FCSTD DOCUMENT  (FreeCAD 1.0R39109 (Git))
Label: solar-strandbeest-v9
License: All rights reserved
LicenseURL: http://en.wikipedia.org/wiki/All_rights_reserved
objects: Sketcher::SketchObject×26, Spreadsheet::Sheet×2, PartDesign::Body×1, App::DocumentObjectGroup×1
note: 53 computed .brp shape members not serialized (recipe doc carries the construction recipe); baked Part::Feature solids carry a one-line shape summary decoded from their .brp

FEATURE [Sketcher::SketchObject] Sketch063  label="construction"
  ArcFitTolerance = 1e-06
  AttachmentSupport = -> [XY_Plane005]
  FullyConstrained = true
  MakeInternals = false
  MapMode = 5
  expr: Constraints[110] = <<v8-Dimensions>>.aGearDistance
  expr: Constraints[115] = <<v8-Dimensions>>.tabHeight
  expr: Constraints[118] = <<v8-Dimensions>>.tabDistanceCut
  expr: Constraints[121] = <<v8-Dimensions>>.solarPanelDepthCut
  expr: Constraints[13] = <<v8-Dimensions>>.aLowerSupportDrop
  expr: Constraints[155] = <<v8-Dimensions>>.aMotorShaftDiameter
  expr: Constraints[186] = <<v8-Dimensions>>.tabWidthCut
  expr: Constraints[187] = <<v8-Dimensions>>.tabHeightCut
  expr: Constraints[189] = <<v8-Dimensions>>.solarPanelWidthCut
  expr: Constraints[18] = 8 mm
  expr: Constraints[198] = <<v8-Dimensions>>.solarSideWidthCut
  expr: Constraints[207] = <<v8-Dimensions>>.jBendPoint
  expr: Constraints[208] = <<v8-Dimensions>>.jBendPoint
  expr: Constraints[209] = <<v8-Dimensions>>.jBendWidth
  expr: Constraints[210] = <<v8-Dimensions>>.jBendOffset
  expr: Constraints[213] = <<v8-Dimensions>>.jBendOffset
  expr: Constraints[215] = <<v8-Dimensions>>.kBendPoint
  expr: Constraints[216] = <<v8-Dimensions>>.kBendWidth
  expr: Constraints[218] = <<v8-Dimensions>>.kBendPoint
  expr: Constraints[219] = <<v8-Dimensions>>.kBendOffset
  expr: Constraints[222] = <<v8-Dimensions>>.eBendWidth
  expr: Constraints[223] = <<v8-Dimensions>>.eBendOffset
  expr: Constraints[225] = <<v8-Dimensions>>.dBendWidth
  expr: Constraints[226] = <<v8-Dimensions>>.dBendOffset
  expr: Constraints[228] = <<v8-Dimensions>>.bBendWidth
  expr: Constraints[229] = <<v8-Dimensions>>.bBendOffset
  expr: Constraints[230] = <<v8-Dimensions>>.kBendOffset
  expr: Constraints[231] = <<v8-Dimensions>>.bdeJunctionEdge
  expr: Constraints[232] = <<v8-Dimensions>>.frame4mmCut
  expr: Constraints[233] = <<v8-Dimensions>>.frame4mmEdge
  expr: Constraints[239] = <<v8-Dimensions>>.fBendWidth
  expr: Constraints[240] = <<v8-Dimensions>>.fBendOffset
  expr: Constraints[241] = <<v8-Dimensions>>.cBendWidth
  expr: Constraints[242] = <<v8-Dimensions>>.cBendOffset
  expr: Constraints[243] = <<v8-Dimensions>>.gBendWidth
  expr: Constraints[244] = <<v8-Dimensions>>.gBendOffset
  expr: Constraints[245] = <<v8-Dimensions>>.hBendWidth
  expr: Constraints[246] = <<v8-Dimensions>>.hBendOffset
  expr: Constraints[247] = <<v8-Dimensions>>.iBendWidth
  expr: Constraints[248] = <<v8-Dimensions>>.iBendOffset
  expr: Constraints[249] = <<v8-Dimensions>>.aMotorToTabCenterDistance
  expr: Constraints[258] = <<v8-Dimensions>>.tabHeightCut
  expr: Constraints[259] = <<v8-Dimensions>>.tabWidthCut
  expr: Constraints[269] = <<v8-Dimensions>>.tabHeightCut
  expr: Constraints[270] = <<v8-Dimensions>>.tabWidthCut
  expr: Constraints[272] = <<v8-Dimensions>>.solarTabWidthCut
  expr: Constraints[95] = <<v8-Dimensions>>.ghiFootRadius
  sketch-geometry (114):
    g0: Circle CenterX=0 CenterY=0 CenterZ=0 NormalX=0 NormalY=0 NormalZ=1 AngleXU=0 Radius=5
    g1: Circle CenterX=0 CenterY=0 CenterZ=0 NormalX=0 NormalY=0 NormalZ=1 AngleXU=0 Radius=3
    g2: LineSegment StartX=0 StartY=0 StartZ=0 EndX=0 EndY=-15.6 EndZ=0
    g3: LineSegment StartX=0 StartY=-15.6 StartZ=0 EndX=-76 EndY=-15.6 EndZ=0
    g4: LineSegment StartX=0 StartY=-15.6 StartZ=0 EndX=76 EndY=-15.6 EndZ=0
    g5: LineSegment StartX=0 StartY=0 StartZ=0 EndX=0 EndY=-70 EndZ=0
    g6: Circle CenterX=-76 CenterY=-15.6 CenterZ=0 NormalX=0 NormalY=0 NormalZ=1 AngleXU=0 Radius=2
    g7: Circle CenterX=-76 CenterY=-15.6 CenterZ=0 NormalX=0 NormalY=0 NormalZ=1 AngleXU=0 Radius=4
    g8: Circle CenterX=76 CenterY=-15.6 CenterZ=0 NormalX=0 NormalY=0 NormalZ=1 AngleXU=0 Radius=2
    g9: Circle CenterX=76 CenterY=-15.6 CenterZ=0 NormalX=0 NormalY=0 NormalZ=1 AngleXU=0 Radius=4
    g10: Circle CenterX=0 CenterY=-70 CenterZ=0 NormalX=0 NormalY=0 NormalZ=1 AngleXU=0 Radius=2
    g11: Circle CenterX=0 CenterY=-70 CenterZ=0 NormalX=0 NormalY=0 NormalZ=1 AngleXU=0 Radius=1.92
    g12: LineSegment StartX=0 StartY=0 StartZ=0 EndX=-25.7172 EndY=15.4475 EndZ=0
    g13: Circle CenterX=-25.7172 CenterY=15.4475 CenterZ=0 NormalX=0 NormalY=0 NormalZ=1 AngleXU=0 Radius=3
    g14: Circle CenterX=-25.7172 CenterY=15.4475 CenterZ=0 NormalX=0 NormalY=0 NormalZ=1 AngleXU=0 Radius=5
    g15: LineSegment StartX=-25.7172 StartY=15.4475 StartZ=0 EndX=-83.9611 EndY=-93.7958 EndZ=0
    g16: LineSegment StartX=-83.9611 StartY=-93.7958 StartZ=0 EndX=-23.6866 EndY=-171.068 EndZ=0
    g17: LineSegment StartX=-23.6866 StartY=-171.068 StartZ=0 EndX=-148.246 EndY=-129.223 EndZ=0
    g18: LineSegment StartX=-148.246 StartY=-129.223 StartZ=0 EndX=-83.9611 EndY=-93.7958 EndZ=0
    g19: LineSegment StartX=-148.246 StartY=-129.223 StartZ=0 EndX=-148.246 EndY=-50.4227 EndZ=0
    g20: LineSegment StartX=-148.246 StartY=-50.4227 StartZ=0 EndX=-76 EndY=-15.6 EndZ=0
    g21: LineSegment StartX=-76 StartY=-15.6 StartZ=0 EndX=-83.9611 EndY=-93.7958 EndZ=0
    g22: LineSegment StartX=-148.246 StartY=-50.4227 StartZ=0 EndX=-116.828 EndY=56.6638 EndZ=0
    g23: LineSegment StartX=-116.828 StartY=56.6638 StartZ=0 EndX=-76 EndY=-15.6 EndZ=0
    g24: LineSegment StartX=-116.828 StartY=56.6638 StartZ=0 EndX=-25.7172 EndY=15.4475 EndZ=0
    g25: LineSegment StartX=-25.7172 StartY=15.4475 StartZ=0 EndX=60.5893 EndY=65.9568 EndZ=0
    g26: LineSegment StartX=60.5893 StartY=65.9568 StartZ=0 EndX=76 EndY=-15.6 EndZ=0
    g27: LineSegment StartX=76 StartY=-15.6 StartZ=0 EndX=153.669 EndY=4.38827 EndZ=0
    g28: LineSegment StartX=153.669 StartY=4.38827 StartZ=0 EndX=60.5893 EndY=65.9568 EndZ=0
    g29: LineSegment StartX=153.669 StartY=4.38827 StartZ=0 EndX=112.83 EndY=-63.0032 EndZ=0
    g30: LineSegment StartX=76 StartY=-15.6 StartZ=0 EndX=43.5253 EndY=-87.1776 EndZ=0
    g31: LineSegment StartX=43.5253 StartY=-87.1776 StartZ=0 EndX=112.83 EndY=-63.0032 EndZ=0
    g32: LineSegment StartX=112.83 StartY=-63.0032 StartZ=0 EndX=60.7671 EndY=-183.649 EndZ=0
    g33: LineSegment StartX=60.7671 StartY=-183.649 StartZ=0 EndX=43.5253 EndY=-87.1776 EndZ=0
    g34: Circle CenterX=-116.828 CenterY=56.6638 CenterZ=0 NormalX=0 NormalY=0 NormalZ=1 AngleXU=0 Radius=1.5
    g35: Circle CenterX=-148.246 CenterY=-50.4227 CenterZ=0 NormalX=0 NormalY=0 NormalZ=1 AngleXU=0 Radius=1.1e-15
    g36: Circle CenterX=-148.246 CenterY=-50.4227 CenterZ=0 NormalX=0 NormalY=0 NormalZ=1 AngleXU=0 Radius=1.5
    g37: Circle CenterX=-148.246 CenterY=-129.223 CenterZ=0 NormalX=0 NormalY=0 NormalZ=1 AngleXU=0 Radius=1.6e-15
    g38: Circle CenterX=-148.246 CenterY=-129.223 CenterZ=0 NormalX=0 NormalY=0 NormalZ=1 AngleXU=0 Radius=1.5
    g39: Circle CenterX=-83.9611 CenterY=-93.7958 CenterZ=0 NormalX=0 NormalY=0 NormalZ=1 AngleXU=0 Radius=1.5
    g40: LineSegment StartX=-23.6866 StartY=-171.068 StartZ=0 EndX=-24.9107 EndY=-170.201 EndZ=0
    g41: Circle CenterX=-24.9107 CenterY=-170.201 CenterZ=0 NormalX=0 NormalY=0 NormalZ=1 AngleXU=0 Radius=1.5
    g42: LineSegment StartX=60.7671 StartY=-183.649 StartZ=0 EndX=60.9396 EndY=-182.159 EndZ=0
    g43: LineSegment StartX=-25.7172 StartY=15.4475 StartZ=0 EndX=43.5253 EndY=-87.1776 EndZ=0
    g44: Circle CenterX=60.5893 CenterY=65.9568 CenterZ=0 NormalX=0 NormalY=0 NormalZ=1 AngleXU=0 Radius=1.5
    g45: Circle CenterX=153.669 CenterY=4.38827 CenterZ=0 NormalX=0 NormalY=0 NormalZ=1 AngleXU=0 Radius=1.5
    g46: Circle CenterX=112.83 CenterY=-63.0032 CenterZ=0 NormalX=0 NormalY=0 NormalZ=1 AngleXU=0 Radius=7e-16
    g47: Circle CenterX=43.5253 CenterY=-87.1776 CenterZ=0 NormalX=0 NormalY=0 NormalZ=1 AngleXU=0 Radius=1.5
    g48: Circle CenterX=112.83 CenterY=-63.0032 CenterZ=0 NormalX=0 NormalY=0 NormalZ=1 AngleXU=0 Radius=1.5
    g49: Circle CenterX=60.9396 CenterY=-182.159 CenterZ=0 NormalX=0 NormalY=0 NormalZ=1 AngleXU=0 Radius=1.5
    g50: LineSegment StartX=0 StartY=0 StartZ=0 EndX=0 EndY=66 EndZ=0
    g51: LineSegment StartX=0 StartY=66 StartZ=0 EndX=0 EndY=75 EndZ=0
    g52: LineSegment StartX=0 StartY=75 StartZ=0 EndX=0 EndY=78 EndZ=0
    g53: LineSegment StartX=0 StartY=78 StartZ=0 EndX=0 EndY=82.16 EndZ=0
    g54: LineSegment StartX=0 StartY=82.16 StartZ=0 EndX=0 EndY=84.82 EndZ=0
    g55: Circle CenterX=-116.828 CenterY=56.6638 CenterZ=0 NormalX=0 NormalY=0 NormalZ=1 AngleXU=0 Radius=4
    g56: Circle CenterX=60.5893 CenterY=65.9568 CenterZ=0 NormalX=0 NormalY=0 NormalZ=1 AngleXU=0 Radius=4
    g57: Circle CenterX=153.669 CenterY=4.38827 CenterZ=0 NormalX=0 NormalY=0 NormalZ=1 AngleXU=0 Radius=4
    g58: Circle CenterX=112.83 CenterY=-63.0032 CenterZ=0 NormalX=0 NormalY=0 NormalZ=1 AngleXU=0 Radius=4
    g59: Circle CenterX=43.5253 CenterY=-87.1776 CenterZ=0 NormalX=0 NormalY=0 NormalZ=1 AngleXU=0 Radius=4
    g60: Circle CenterX=-148.246 CenterY=-50.4227 CenterZ=0 NormalX=0 NormalY=0 NormalZ=1 AngleXU=0 Radius=4
    g61: Circle CenterX=-83.9611 CenterY=-93.7958 CenterZ=0 NormalX=0 NormalY=0 NormalZ=1 AngleXU=0 Radius=4
    g62: Circle CenterX=-148.246 CenterY=-129.223 CenterZ=0 NormalX=0 NormalY=0 NormalZ=1 AngleXU=0 Radius=4
    g63: Circle CenterX=-25.7172 CenterY=15.4475 CenterZ=0 NormalX=0 NormalY=0 NormalZ=1 AngleXU=0 Radius=7.5
    g64: Circle CenterX=0 CenterY=0 CenterZ=0 NormalX=0 NormalY=0 NormalZ=1 AngleXU=0 Radius=7.5
    g65: Circle CenterX=-76 CenterY=-15.6 CenterZ=0 NormalX=0 NormalY=0 NormalZ=1 AngleXU=0 Radius=7.08
    g66: Circle CenterX=76 CenterY=-15.6 CenterZ=0 NormalX=0 NormalY=0 NormalZ=1 AngleXU=0 Radius=7.5
    g67: LineSegment StartX=-10.7989 StartY=11.1527 StartZ=0 EndX=-14.9183 EndY=4.29478 EndZ=0
    g68: Circle CenterX=0 CenterY=66 CenterZ=0 NormalX=0 NormalY=0 NormalZ=1 AngleXU=0 Radius=1.5
    g69: LineSegment StartX=-6 StartY=61 StartZ=0 EndX=6 EndY=61 EndZ=0
    g70: LineSegment StartX=6 StartY=61 StartZ=0 EndX=6 EndY=71 EndZ=0
    g71: LineSegment StartX=6 StartY=71 StartZ=0 EndX=-6 EndY=71 EndZ=0
    g72: LineSegment StartX=-6 StartY=71 StartZ=0 EndX=-6 EndY=61 EndZ=0
    g73: GeomPoint [constr] X=0 Y=66 Z=0
    g74: LineSegment StartX=20.6971 StartY=25.2307 StartZ=0 EndX=22.7175 EndY=21.7784 EndZ=0
    g75: Circle CenterX=0 CenterY=-70 CenterZ=0 NormalX=0 NormalY=0 NormalZ=1 AngleXU=0 Radius=4.08
    g76: ArcOfCircle CenterX=0 CenterY=66 CenterZ=0 NormalX=0 NormalY=0 NormalZ=1 AngleXU=0 Radius=6 StartAngle=2.15648 EndAngle=4.1267
    g77: ArcOfCircle CenterX=0 CenterY=66 CenterZ=0 NormalX=0 NormalY=0 NormalZ=1 AngleXU=0 Radius=6 StartAngle=5.29807 EndAngle=7.2683
    g78: LineSegment StartX=-2.92 StartY=75.08 StartZ=0 EndX=2.92 EndY=75.08 EndZ=0
    g79: LineSegment StartX=2.92 StartY=75.08 StartZ=0 EndX=2.92 EndY=77.92 EndZ=0
    g80: LineSegment StartX=2.92 StartY=77.92 StartZ=0 EndX=-2.92 EndY=77.92 EndZ=0
    g81: LineSegment StartX=-2.92 StartY=77.92 StartZ=0 EndX=-2.92 EndY=75.08 EndZ=0
    g82: GeomPoint X=0 Y=76.5 Z=0
    g83: LineSegment StartX=29.92 StartY=82.16 StartZ=0 EndX=-29.92 EndY=82.16 EndZ=0
    g84: LineSegment StartX=-29.92 StartY=82.16 StartZ=0 EndX=-29.92 EndY=84.66 EndZ=0
    g85: LineSegment StartX=29.92 StartY=82.16 StartZ=0 EndX=29.92 EndY=84.66 EndZ=0
    g86: LineSegment StartX=-29.92 StartY=84.66 StartZ=0 EndX=-34.08 EndY=84.66 EndZ=0
    g87: LineSegment StartX=29.92 StartY=84.66 StartZ=0 EndX=34.08 EndY=84.66 EndZ=0
    g88: LineSegment StartX=-72.8996 StartY=20.3282 StartZ=0 EndX=-74.5483 EndY=16.6837 EndZ=0
    g89: LineSegment StartX=-38.3567 StartY=-40.1425 StartZ=0 EndX=-34.827 EndY=-42.0244 EndZ=0
    g90: LineSegment StartX=17.4792 StartY=-21.7556 StartZ=0 EndX=14.1634 EndY=-23.9928 EndZ=0
    g91: LineSegment StartX=-124.86 StartY=0.868425 StartZ=0 EndX=-121.022 EndY=-0.257645 EndZ=0
    g92: LineSegment StartX=-120.373 StartY=-15.8958 StartZ=0 EndX=-118.202 EndY=-20.3999 EndZ=0
    g93: LineSegment StartX=-105.121 StartY=15.6128 StartZ=0 EndX=-109.474 EndY=13.1533 EndZ=0
    g94: LineSegment StartX=-140.246 StartY=-89.8227 StartZ=0 EndX=-135.246 EndY=-89.8227 EndZ=0
    g95: LineSegment StartX=-87.9394 StartY=-53.8876 StartZ=0 EndX=-92.9137 EndY=-53.3812 EndZ=0
    g96: LineSegment StartX=-112.242 StartY=-118.516 StartZ=0 EndX=-109.829 EndY=-122.895 EndZ=0
    g97: LineSegment StartX=-62.1774 StartY=-137.982 StartZ=0 EndX=-66.1336 EndY=-141.039 EndZ=0
    g98: LineSegment StartX=-83.4932 StartY=-140.427 StartZ=0 EndX=-81.9167 EndY=-135.682 EndZ=0
    g99: LineSegment StartX=19.08 StartY=77.92 StartZ=0 EndX=19.08 EndY=72.08 EndZ=0
    g100: LineSegment StartX=19.08 StartY=72.08 StartZ=0 EndX=21.92 EndY=72.08 EndZ=0
    g101: LineSegment StartX=21.92 StartY=72.08 StartZ=0 EndX=21.92 EndY=77.92 EndZ=0
    g102: LineSegment StartX=21.92 StartY=77.92 StartZ=0 EndX=19.08 EndY=77.92 EndZ=0
    g103: LineSegment StartX=-21.92 StartY=77.92 StartZ=0 EndX=-21.92 EndY=72.08 EndZ=0
    g104: LineSegment StartX=-21.92 StartY=72.08 StartZ=0 EndX=-19.08 EndY=72.08 EndZ=0
    g105: LineSegment StartX=-19.08 StartY=72.08 StartZ=0 EndX=-19.08 EndY=77.92 EndZ=0
    g106: LineSegment StartX=-19.08 StartY=77.92 StartZ=0 EndX=-21.92 EndY=77.92 EndZ=0
    g107: GeomPoint X=-20.5 Y=75 Z=0
    g108: GeomPoint X=20.5 Y=75 Z=0
    g109: GeomPoint X=0 Y=75 Z=0
    g110: GeomPoint X=0 Y=82.16 Z=0
    g111: GeomPoint X=58.84 Y=-15.6 Z=0
    g112: GeomPoint X=-58.84 Y=-15.6 Z=0
    g113: GeomPoint [constr] X=-58.84 Y=-15.6 Z=0
  constraints (283):
    c: Diameter(g0) = 10  'mDiameterCut'
    c: Coincident(g0,g-1)
    c: Diameter(g1) = 6
    c: Coincident(g1,g0)
    c: Distance(g2) = 15.6
    c: Coincident(g2,g0)
    c: PointOnObject(g2,g-2)
    c: Distance(g3) = 76
    c: Coincident(g3,g2)
    c: Horizontal(g3)
    c: Distance(g4) = 76
    c: Coincident(g4,g2)
    c: Horizontal(g4)
    c: Distance(g5) = 70
    c: Coincident(g5,g0)
    c: PointOnObject(g5,g-2)
    c: Diameter(g6) = 4
    c: Coincident(g6,g3)
    c: Diameter(g7) = 8
    c: Coincident(g7,g3)
    c: Coincident(g8,g4)
    c: Coincident(g9,g4)
    c: Equal(g7,g9)
    c: Equal(g8,g6)
    c: Coincident(g10,g5)
    c: Coincident(g11,g5)
    c: Equal(g6,g10)
    c: Distance(g12) = 30
    c: Coincident(g12,g0)
    c: Coincident(g13,g12)
    c: Coincident(g14,g12)
    c: Equal(g1,g13)
    c: Equal(g0,g14)
    c: Distance(g15) = 123.8
    c: Coincident(g15,g12)
    c: Distance(g16) = 98
    c: Coincident(g16,g15)
    c: Distance(g17) = 131.4
    c: Coincident(g17,g16)
    c: Coincident(g18,g17)
    c: Coincident(g18,g15)
    c: Distance(g18) = 73.4
    c: Distance(g19) = 78.8
    c: Coincident(g19,g17)
    c: Vertical(g19)
    c: Distance(g20) = 80.2
    c: Coincident(g20,g19)
    c: Distance(g21) = 78.6
    c: Coincident(g21,g20)
    c: Coincident(g21,g15)
    c: Distance(g22) = 111.6
    c: Coincident(g22,g19)
    c: Distance(g23) = 83
    c: Coincident(g23,g22)
    c: Coincident(g23,g20)
    c: Distance(g24) = 100
    c: Coincident(g24,g22)
    c: Coincident(g24,g12)
    c: Distance(g25) = 100
    c: Coincident(g25,g12)
    c: Distance(g26) = 83
    c: Coincident(g26,g25)
    c: Distance(g27) = 80.2
    c: Coincident(g27,g26)
    c: Distance(g28) = 111.6
    c: Coincident(g28,g27)
    c: Coincident(g28,g25)
    c: Distance(g29) = 78.8
    c: Coincident(g29,g27)
    c: Distance(g30) = 78.6
    c: Coincident(g30,g26)
    c: Distance(g31) = 73.4
    c: Coincident(g31,g29)
    c: Distance(g32) = 131.4
    c: Coincident(g32,g29)
    c: Distance(g33) = 98
    c: Coincident(g33,g32)
    c: Coincident(g20,g3)
    c: Coincident(g26,g4)
    c: Coincident(g33,g31)
    c: Coincident(g33,g30)
    c: Diameter(g34) = 3
    c: Coincident(g34,g22)
    c: Coincident(g35,g19)
    c: Tangent(g35,g20)
    c: Diameter(g36) = 3
    c: Coincident(g36,g19)
    c: Coincident(g37,g17)
    c: Tangent(g37,g17)
    c: Diameter(g38) = 3
    c: Coincident(g38,g17)
    c: Diameter(g39) = 3
    c: Coincident(g39,g15)
    c: Coincident(g40,g16)
    c: Angle(g16,g40) = 0.292124
    c: Distance(g40) = 1.5
    c: Coincident(g41,g40)
    c: PointOnObject(g16,g41)
    c: Coincident(g42,g32)
    c: Angle(g42,g33) = 0.292124
    c: Distance(g43) = 123.8
    c: Coincident(g43,g12)
    c: Coincident(g43,g30)
    c: Coincident(g44,g25)
    c: Coincident(g45,g27)
    c: Coincident(g46,g29)
    c: Tangent(g46,g29)
    c: Coincident(g47,g30)
    c: Coincident(g48,g29)
    c: Coincident(g49,g42)
    c: Distance(g50) = 66
    c: Coincident(g50,g0)
    c: PointOnObject(g50,g-2)
    c: Coincident(g51,g50)
    c: PointOnObject(g51,g-2)
    c: Distance(g52) = 3
    c: Coincident(g52,g51)
    c: PointOnObject(g52,g-2)
    c: Distance(g53) = 4.16
    c: Coincident(g53,g52)
    c: PointOnObject(g53,g-2)
    c: Distance(g54) = 2.66
    c: Coincident(g54,g53)
    c: PointOnObject(g54,g-2)
    c: Equal(g34,g44)
    c: Equal(g45,g36)
    c: Equal(g48,g36)
    c: Equal(g47,g39)
    c: Equal(g49,g41)
    c: Equal(g42,g40)
    c: Diameter(g55) = 8
    c: Coincident(g55,g22)
    c: Coincident(g56,g25)
    c: Equal(g56,g55)
    c: Coincident(g57,g27)
    c: Coincident(g58,g29)
    c: Coincident(g59,g30)
    c: Coincident(g60,g19)
    c: Coincident(g61,g15)
    c: Coincident(g62,g17)
    c: Equal(g55,g60)
    c: Equal(g55,g62)
    c: Equal(g55,g61)
    c: Equal(g57,g55)
    c: Equal(g58,g55)
    c: Equal(g59,g55)
    c: Diameter(g63) = 15  'mDiameterEdge'
    c: Coincident(g63,g12)
    c: Coincident(g64,g0)
    c: Equal(g63,g64)
    c: Coincident(g65,g3)
    c: Coincident(g66,g4)
    c: Equal(g66,g63)
    c: Symmetric(g67,g67,g12)
    c: Distance(g67,g67) = 8
    c: Diameter(g68) = 3
    c: Coincident(g68,g50)
    c: Coincident(g69,g70)
    c: Coincident(g70,g71)
    c: Coincident(g71,g72)
    c: Coincident(g72,g69)
    c: Horizontal(g69)
    c: Horizontal(g71)
    c: Vertical(g70)
    c: Vertical(g72)
    c: Symmetric(g71,g69,g73)
    c: Distance(g70,g72) = 12
    c: Distance(g69,g71) = 10
    c: Coincident(g73,g50)
    c: Coincident(g75,g5)
    c: Radius(g76) = 6
    c: Coincident(g76,g50)
    c: PointOnObject(g76,g71)
    c: PointOnObject(g76,g69)
    c: Coincident(g77,g50)
    c: PointOnObject(g77,g71)
    c: PointOnObject(g77,g69)
    c: Coincident(g78,g79)
    c: Coincident(g79,g80)
    c: Coincident(g80,g81)
    c: Coincident(g81,g78)
    c: Horizontal(g78)
    c: Horizontal(g80)
    c: Vertical(g79)
    c: Vertical(g81)
    c: Symmetric(g80,g78,g82)
    c: Distance(g79,g81) = 5.84
    c: Distance(g78,g80) = 2.84
    c: Symmetric(g52,g52,g82)
    c: Distance(g83) = 59.84
    c: Symmetric(g83,g83,g-2)
    c: PointOnObject(g53,g83)
    c: Distance(g84) = 2.5
    c: Coincident(g84,g83)
    c: Vertical(g84)
    c: Coincident(g85,g83)
    c: Vertical(g85)
    c: Equal(g85,g84)
    c: Distance(g86) = 4.16
    c: Coincident(g86,g84)
    c: Horizontal(g86)
    c: Coincident(g87,g85)
    c: Horizontal(g87)
    c: Equal(g87,g86)
    c: Perpendicular(g24,g88)
    c: Perpendicular(g25,g74)
    c: Equal(g74,g88)
    c: Distance(g12,g88) = 45
    c: Distance(g12,g74) = 45
    c: Distance(g88) = 4
    c: Distance(g74,g25) = 15
    c: Radius(g77) = 6
    c: Distance(g0,g67) = 15
    c: Distance(g88,g24) = 15
    c: Perpendicular(g15,g89)
    c: Distance(g12,g89) = 55
    c: Distance(g89) = 4
    c: Perpendicular(g43,g90)
    c: Distance(g12,g90) = 55
    c: Distance(g90,g43) = 15
    c: Equal(g89,g90)
    c: Symmetric(g22,g19,g91)
    c: Distance(g91) = 4
    c: Distance(g91,g22) = 8
    c: Symmetric(g19,g3,g92)
    c: Distance(g92) = 5
    c: Distance(g92,g20) = 14
    c: Symmetric(g22,g3,g93)
    c: Distance(g93) = 5
    c: Distance(g93,g23) = 10
    c: Distance(g89,g15) = 15
    c: Diameter(g65) = 14.16
    c: Diameter(g11) = 3.84
    c: Diameter(g75) = 8.16
    c: Symmetric(g19,g17,g94)
    c: Symmetric(g3,g15,g95)
    c: Symmetric(g15,g17,g96)
    c: Symmetric(g15,g40,g97)
    c: Symmetric(g17,g40,g98)
    c: Distance(g94) = 5
    c: Distance(g94,g19) = 8
    c: Distance(g95) = 5
    c: Distance(g95,g21) = 8
    c: Distance(g96) = 5
    c: Distance(g96,g18) = 8
    c: Distance(g98) = 5
    c: Distance(g98,g17) = 10
    c: Distance(g97) = 5
    c: Distance(g97,g16) = 10
    c: Distance(g82,g50) = 10.5
    c: Coincident(g99,g100)
    c: Coincident(g100,g101)
    c: Coincident(g101,g102)
    c: Coincident(g102,g99)
    c: Vertical(g99)
    c: Vertical(g101)
    c: Horizontal(g100)
    c: Horizontal(g102)
    c: Distance(g99,g101) = 2.84
    c: Distance(g100,g102) = 5.84
    c: Horizontal(g79,g99)
    c: Coincident(g103,g104)
    c: Coincident(g104,g105)
    c: Coincident(g105,g106)
    c: Coincident(g106,g103)
    c: Vertical(g103)
    c: Vertical(g105)
    c: Horizontal(g104)
    c: Horizontal(g106)
    c: Distance(g103,g105) = 2.84
    c: Distance(g104,g106) = 5.84
    c: Symmetric(g105,g99,g53)
    c: DistanceX(g105,g99) = 38.16
    c: Symmetric(g105,g103,g107)
    c: Symmetric(g101,g99,g108)
    c: PointOnObject(g109,g51)
    c: Horizontal(g107,g109)
    c: PointOnObject(g110,g54)
    c: PointOnObject(g110,g83)
    c: PointOnObject(g111,g4)
    c: Symmetric(g111,g112,g2)
    c: Distance(g3,g112) = 17.16
    c: Coincident(g113,g112)
FEATURE [Sketcher::SketchObject] Sketch064  label="v8-m"
  ArcFitTolerance = 1e-06
  AttachmentSupport = -> [XY_Plane005]
  ExternalGeometry = -> [Sketch063]
  FullyConstrained = true
  MakeInternals = false
  MapMode = 5
  expr: Constraints[1] = <<v8-Dimensions>>.mDiameterCut
  expr: Constraints[25] = <<v8-Dimensions>>.mMidWidth
  expr: Constraints[3] = <<v8-Dimensions>>.mDiameterCut
  expr: Constraints[5] = <<v8-Dimensions>>.mDiameterEdge
  expr: Constraints[7] = <<v8-Dimensions>>.mDiameterEdge
  sketch-geometry (16):
    g0: Circle CenterX=-25.7172 CenterY=15.4475 CenterZ=0 NormalX=0 NormalY=0 NormalZ=1 AngleXU=0 Radius=2.92
    g1: Circle CenterX=0 CenterY=0 CenterZ=0 NormalX=0 NormalY=0 NormalZ=1 AngleXU=0 Radius=2.92
    g2: ArcOfCircle CenterX=-25.7172 CenterY=15.4475 CenterZ=0 NormalX=0 NormalY=0 NormalZ=1 AngleXU=0 Radius=7.58 StartAngle=0.673216 EndAngle=4.52815
    g3: ArcOfCircle CenterX=0 CenterY=0 CenterZ=0 NormalX=0 NormalY=0 NormalZ=1 AngleXU=0 Radius=7.58 StartAngle=3.81481 EndAngle=7.66974
    g4: Circle [constr] CenterX=-19.791 CenterY=20.1736 CenterZ=0 NormalX=0 NormalY=0 NormalZ=1 AngleXU=0 Radius=1
    g5: Circle [constr] CenterX=-11.5713 CenterY=9.86684 CenterZ=0 NormalX=0 NormalY=0 NormalZ=1 AngleXU=0 Radius=1
    g6: Circle [constr] CenterX=1.38865 CenterY=7.45171 CenterZ=0 NormalX=0 NormalY=0 NormalZ=1 AngleXU=0 Radius=1
    g7: BSplineCurve PolesCount=3 KnotsCount=2 Degree=2 IsPeriodic=0
    g8: GeomPoint [constr] X=-19.791 Y=20.1736 Z=0
    g9: GeomPoint [constr] X=1.38865 Y=7.45171 Z=0
    g10: Circle [constr] CenterX=-27.1059 CenterY=7.99577 CenterZ=0 NormalX=0 NormalY=0 NormalZ=1 AngleXU=0 Radius=1
    g11: Circle [constr] CenterX=-14.1459 CenterY=5.58064 CenterZ=0 NormalX=0 NormalY=0 NormalZ=1 AngleXU=0 Radius=1
    g12: Circle [constr] CenterX=-5.9262 CenterY=-4.72616 CenterZ=0 NormalX=0 NormalY=0 NormalZ=1 AngleXU=0 Radius=1
    g13: BSplineCurve PolesCount=3 KnotsCount=2 Degree=2 IsPeriodic=0
    g14: GeomPoint [constr] X=-27.1059 Y=7.99577 Z=0
    g15: GeomPoint [constr] X=-5.9262 Y=-4.72616 Z=0
  constraints (31):
    c: Coincident(g0,g-12)
    c: Diameter(g0) = 5.84
    c: Coincident(g1,g-1)
    c: Diameter(g1) = 5.84
    c: Coincident(g2,g0)
    c: Diameter(g2) = 15.16
    c: Coincident(g3,g1)
    c: Diameter(g3) = 15.16
    c: Weight(g4) = 1
    c: Equal(g4,g5)
    c: Equal(g4,g6)
    c: InternalAlignment(g4,g7)
    c: InternalAlignment(g5,g7)
    c: InternalAlignment(g6,g7)
    c: InternalAlignment(g8,g7)
    c: InternalAlignment(g9,g7)
    c: PointOnObject(g5,g-8)
    c: Weight(g10) = 1
    c: Equal(g10,g11)
    c: Equal(g10,g12)
    c: InternalAlignment(g10,g13)
    c: InternalAlignment(g11,g13)
    c: InternalAlignment(g12,g13)
    c: InternalAlignment(g14,g13)
    c: InternalAlignment(g15,g13)
    c: Distance(g5,g11) = 5
    c: Tangent(g7,g2) = 1.5708
    c: Tangent(g13,g2) = -1.5708
    c: Tangent(g13,g3) = -1.5708
    c: Tangent(g7,g3) = 1.5708
    c: Symmetric(g5,g11,g-9)
FEATURE [Sketcher::SketchObject] Sketch065  label="v8-j"
  ArcFitTolerance = 1e-06
  AttachmentSupport = -> [XY_Plane005]
  ExternalGeometry = -> [Sketch063]
  FullyConstrained = true
  MakeInternals = false
  MapMode = 5
  expr: Constraints[1] = <<v8-Dimensions>>.jDiameterCut
  expr: Constraints[3] = <<v8-Dimensions>>.jBearingCut
  expr: Constraints[5] = <<v8-Dimensions>>.jDiameterEdge
  expr: Constraints[7] = <<v8-Dimensions>>.mDiameterEdge
  sketch-geometry (16):
    g0: Circle CenterX=-116.828 CenterY=56.6638 CenterZ=0 NormalX=0 NormalY=0 NormalZ=1 AngleXU=0 Radius=1.5
    g1: Circle CenterX=-25.7172 CenterY=15.4475 CenterZ=0 NormalX=0 NormalY=0 NormalZ=1 AngleXU=0 Radius=4.92
    g2: ArcOfCircle CenterX=-116.828 CenterY=56.6638 CenterZ=0 NormalX=0 NormalY=0 NormalZ=1 AngleXU=0 Radius=4.08 StartAngle=0.808088 EndAngle=4.02512
    g3: ArcOfCircle CenterX=-25.7172 CenterY=15.4475 CenterZ=0 NormalX=0 NormalY=0 NormalZ=1 AngleXU=0 Radius=7.58 StartAngle=4.53127 EndAngle=7.91139
    g4: Circle [constr] CenterX=-114.009 CenterY=59.6135 CenterZ=0 NormalX=0 NormalY=0 NormalZ=1 AngleXU=0 Radius=1
    g5: Circle [constr] CenterX=-72.8996 CenterY=20.3282 CenterZ=0 NormalX=0 NormalY=0 NormalZ=1 AngleXU=0 Radius=1
    g6: Circle [constr] CenterX=-26.1522 CenterY=23.015 CenterZ=0 NormalX=0 NormalY=0 NormalZ=1 AngleXU=0 Radius=1
    g7: BSplineCurve PolesCount=3 KnotsCount=2 Degree=2 IsPeriodic=0
    g8: GeomPoint [constr] X=-114.009 Y=59.6135 Z=0
    g9: GeomPoint [constr] X=-26.1522 Y=23.015 Z=0
    g10: Circle [constr] CenterX=-119.417 CenterY=53.51 CenterZ=0 NormalX=0 NormalY=0 NormalZ=1 AngleXU=0 Radius=1
    g11: Circle [constr] CenterX=-74.5483 CenterY=16.6837 CenterZ=0 NormalX=0 NormalY=0 NormalZ=1 AngleXU=0 Radius=1
    g12: Circle [constr] CenterX=-27.0826 CenterY=7.99148 CenterZ=0 NormalX=0 NormalY=0 NormalZ=1 AngleXU=0 Radius=1
    g13: BSplineCurve PolesCount=3 KnotsCount=2 Degree=2 IsPeriodic=0
    g14: GeomPoint [constr] X=-119.417 Y=53.51 Z=0
    g15: GeomPoint [constr] X=-27.0826 Y=7.99148 Z=0
  constraints (30):
    c: Coincident(g0,g-3)
    c: Diameter(g0) = 3
    c: Coincident(g1,g-4)
    c: Diameter(g1) = 9.84
    c: Coincident(g2,g0)
    c: Diameter(g2) = 8.16
    c: Coincident(g3,g1)
    c: Diameter(g3) = 15.16
    c: Weight(g4) = 1
    c: Equal(g4,g5)
    c: Equal(g4,g6)
    c: InternalAlignment(g4,g7)
    c: InternalAlignment(g5,g7)
    c: InternalAlignment(g6,g7)
    c: InternalAlignment(g8,g7)
    c: InternalAlignment(g9,g7)
    c: Coincident(g5,g-7)
    c: Weight(g10) = 1
    c: Equal(g10,g11)
    c: Equal(g10,g12)
    c: InternalAlignment(g10,g13)
    c: InternalAlignment(g11,g13)
    c: InternalAlignment(g12,g13)
    c: InternalAlignment(g14,g13)
    c: InternalAlignment(g15,g13)
    c: Coincident(g11,g-7)
    c: Tangent(g7,g2) = 1.5708
    c: Tangent(g13,g2) = -1.5708
    c: Tangent(g7,g3) = 1.5708
    c: Tangent(g13,g3) = -1.5708
FEATURE [Sketcher::SketchObject] Sketch066  label="v8-k"
  ArcFitTolerance = 1e-06
  AttachmentSupport = -> [XY_Plane005]
  ExternalGeometry = -> [Sketch063]
  FullyConstrained = true
  MakeInternals = false
  MapMode = 5
  expr: Constraints[1] = <<v8-Dimensions>>.jBearingCut
  expr: Constraints[27] = <<v8-Dimensions>>.kDiameterEdge
  expr: Constraints[29] = <<v8-Dimensions>>.kDiameterCut
  expr: Constraints[3] = <<v8-Dimensions>>.mDiameterEdge
  sketch-geometry (16):
    g0: Circle CenterX=-25.7172 CenterY=15.4475 CenterZ=0 NormalX=0 NormalY=0 NormalZ=1 AngleXU=0 Radius=4.92
    g1: ArcOfCircle CenterX=-25.7172 CenterY=15.4475 CenterZ=0 NormalX=0 NormalY=0 NormalZ=1 AngleXU=0 Radius=7.58 StartAngle=5.99535 EndAngle=9.33457
    g2: ArcOfCircle CenterX=-83.9611 CenterY=-93.7958 CenterZ=0 NormalX=0 NormalY=0 NormalZ=1 AngleXU=0 Radius=4.08 StartAngle=2.37913 EndAngle=5.58111
    g3: Circle [constr] CenterX=-33.2664 CenterY=16.1304 CenterZ=0 NormalX=0 NormalY=0 NormalZ=1 AngleXU=0 Radius=1
    g4: Circle [constr] CenterX=-38.3567 CenterY=-40.1425 CenterZ=0 NormalX=0 NormalY=0 NormalZ=1 AngleXU=0 Radius=1
    g5: Circle [constr] CenterX=-86.9115 CenterY=-90.9777 CenterZ=0 NormalX=0 NormalY=0 NormalZ=1 AngleXU=0 Radius=1
    g6: BSplineCurve PolesCount=3 KnotsCount=2 Degree=2 IsPeriodic=0
    g7: GeomPoint [constr] X=-33.2664 Y=16.1304 Z=0
    g8: GeomPoint [constr] X=-86.9115 Y=-90.9777 Z=0
    g9: Circle [constr] CenterX=-80.846 CenterY=-96.4307 CenterZ=0 NormalX=0 NormalY=0 NormalZ=1 AngleXU=0 Radius=1
    g10: Circle [constr] CenterX=-34.827 CenterY=-42.0244 CenterZ=0 NormalX=0 NormalY=0 NormalZ=1 AngleXU=0 Radius=1
    g11: Circle [constr] CenterX=-18.4491 CenterY=13.2957 CenterZ=0 NormalX=0 NormalY=0 NormalZ=1 AngleXU=0 Radius=1
    g12: BSplineCurve PolesCount=3 KnotsCount=2 Degree=2 IsPeriodic=0
    g13: GeomPoint [constr] X=-80.846 Y=-96.4307 Z=0
    g14: GeomPoint [constr] X=-18.4491 Y=13.2957 Z=0
    g15: Circle CenterX=-83.9611 CenterY=-93.7958 CenterZ=0 NormalX=0 NormalY=0 NormalZ=1 AngleXU=0 Radius=1.5
  constraints (30):
    c: Coincident(g0,g-3)
    c: Diameter(g0) = 9.84
    c: Coincident(g1,g0)
    c: Diameter(g1) = 15.16
    c: Coincident(g2,g-3)
    c: Weight(g3) = 1
    c: Equal(g3,g4)
    c: Equal(g3,g5)
    c: InternalAlignment(g3,g6)
    c: InternalAlignment(g4,g6)
    c: InternalAlignment(g5,g6)
    c: InternalAlignment(g7,g6)
    c: InternalAlignment(g8,g6)
    c: Coincident(g4,g-4)
    c: Weight(g9) = 1
    c: Equal(g9,g10)
    c: Equal(g9,g11)
    c: InternalAlignment(g9,g12)
    c: InternalAlignment(g10,g12)
    c: InternalAlignment(g11,g12)
    c: InternalAlignment(g13,g12)
    c: InternalAlignment(g14,g12)
    c: Coincident(g10,g-4)
    c: Tangent(g6,g1) = -1.5708
    c: Tangent(g12,g1) = -1.5708
    c: Tangent(g12,g2) = -1.5708
    c: Tangent(g6,g2) = -1.5708
    c: Diameter(g2) = 8.16
    c: Coincident(g15,g2)
    c: Diameter(g15) = 3
FEATURE [Sketcher::SketchObject] Sketch067  label="v8-bde"
  ArcFitTolerance = 1e-06
  AttachmentSupport = -> [XY_Plane005]
  ExternalGeometry = -> [Sketch063]
  FullyConstrained = true
  MakeInternals = false
  MapMode = 5
  expr: Constraints[106] = <<v8-Dimensions>>.bdeJunctionCut
  expr: Constraints[108] = <<v8-Dimensions>>.bdeDiameterCut
  expr: Constraints[110] = <<v8-Dimensions>>.bdeDiameterCut
  expr: Constraints[115] = <<v8-Dimensions>>.bdeJunctionEdge
  expr: Constraints[71] = <<v8-Dimensions>>.bdeDiameterEdge
  expr: Constraints[72] = <<v8-Dimensions>>.bdeDiameterEdge
  sketch-geometry (63):
    g0: Circle [constr] CenterX=-77.1762 CenterY=-8.61839 CenterZ=0 NormalX=0 NormalY=0 NormalZ=1 AngleXU=0 Radius=1
    g1: Circle [constr] CenterX=-120.373 CenterY=-15.8958 CenterZ=0 NormalX=0 NormalY=0 NormalZ=1 AngleXU=0 Radius=1
    g2: Circle [constr] CenterX=-151.119 CenterY=-47.6398 CenterZ=0 NormalX=0 NormalY=0 NormalZ=1 AngleXU=0 Radius=1
    g3: BSplineCurve [constr] PolesCount=3 KnotsCount=2 Degree=2 IsPeriodic=0
    g4: GeomPoint [constr] X=-77.1762 Y=-8.61839 Z=0
    g5: GeomPoint [constr] X=-151.119 Y=-47.6398 Z=0
    g6: Circle [constr] CenterX=-144.605 CenterY=-52.0795 CenterZ=0 NormalX=0 NormalY=0 NormalZ=1 AngleXU=0 Radius=1
    g7: Circle [constr] CenterX=-121.022 CenterY=-0.257645 CenterZ=0 NormalX=0 NormalY=0 NormalZ=1 AngleXU=0 Radius=1
    g8: Circle [constr] CenterX=-112.869 CenterY=56.091 CenterZ=0 NormalX=0 NormalY=0 NormalZ=1 AngleXU=0 Radius=1
    g9: BSplineCurve [constr] PolesCount=3 KnotsCount=2 Degree=2 IsPeriodic=0
    g10: GeomPoint [constr] X=-144.605 Y=-52.0795 Z=0
    g11: GeomPoint [constr] X=-112.869 Y=56.091 Z=0
    g12: Circle [constr] CenterX=-81.4152 CenterY=-20.1609 CenterZ=0 NormalX=0 NormalY=0 NormalZ=1 AngleXU=0 Radius=1
    g13: Circle [constr] CenterX=-109.474 CenterY=13.1533 CenterZ=0 NormalX=0 NormalY=0 NormalZ=1 AngleXU=0 Radius=1
    g14: Circle [constr] CenterX=-120.696 CenterY=55.6424 CenterZ=0 NormalX=0 NormalY=0 NormalZ=1 AngleXU=0 Radius=1
    g15: BSplineCurve [constr] PolesCount=3 KnotsCount=2 Degree=2 IsPeriodic=0
    g16: GeomPoint [constr] X=-81.4152 Y=-20.1609 Z=0
    g17: GeomPoint [constr] X=-120.696 Y=55.6424 Z=0
    g18: GeomPoint X=-137.362 Y=-35.1519 Z=0
    g19: GeomPoint X=-115.652 Y=39.3447 Z=0
    g20: GeomPoint X=-88.6537 Y=-11.0397 Z=0
    g21: ArcOfCircle CenterX=-116.828 CenterY=56.6638 CenterZ=0 NormalX=0 NormalY=0 NormalZ=1 AngleXU=0 Radius=4.08 StartAngle=0.182098 EndAngle=3.07106
    g22: ArcOfCircle CenterX=-148.246 CenterY=-50.4227 CenterZ=0 NormalX=0 NormalY=0 NormalZ=1 AngleXU=0 Radius=4.08 StartAngle=2.64138 EndAngle=5.59364
    g23: Circle [constr] CenterX=-120.898 CenterY=56.9513 CenterZ=0 NormalX=0 NormalY=0 NormalZ=1 AngleXU=0 Radius=1
    g24: Circle [constr] CenterX=-124.86 CenterY=0.868425 CenterZ=0 NormalX=0 NormalY=0 NormalZ=1 AngleXU=0 Radius=1
    g25: Circle [constr] CenterX=-151.826 CenterY=-48.4658 CenterZ=0 NormalX=0 NormalY=0 NormalZ=1 AngleXU=0 Radius=1
    g26: BSplineCurve PolesCount=3 KnotsCount=2 Degree=2 IsPeriodic=0
    g27: GeomPoint [constr] X=-120.898 Y=56.9513 Z=0
    g28: GeomPoint [constr] X=-151.826 Y=-48.4658 Z=0
    g29: Circle [constr] CenterX=-112.816 CenterY=57.4027 CenterZ=0 NormalX=0 NormalY=0 NormalZ=1 AngleXU=0 Radius=1
    g30: Circle [constr] CenterX=-105.121 CenterY=15.6128 CenterZ=0 NormalX=0 NormalY=0 NormalZ=1 AngleXU=0 Radius=1
    g31: Circle [constr] CenterX=-71.6959 CenterY=-9.97849 CenterZ=0 NormalX=0 NormalY=0 NormalZ=1 AngleXU=0 Radius=1
    g32: BSplineCurve PolesCount=3 KnotsCount=2 Degree=2 IsPeriodic=0
    g33: GeomPoint [constr] X=-112.816 Y=57.4027 Z=0
    g34: GeomPoint [constr] X=-71.6959 Y=-9.97849 Z=0
    g35: Circle [constr] CenterX=-76.3837 CenterY=-22.6696 CenterZ=0 NormalX=0 NormalY=0 NormalZ=1 AngleXU=0 Radius=1
    g36: Circle [constr] CenterX=-118.202 CenterY=-20.3999 CenterZ=0 NormalX=0 NormalY=0 NormalZ=1 AngleXU=0 Radius=1
    g37: Circle [constr] CenterX=-145.098 CenterY=-53.0183 CenterZ=0 NormalX=0 NormalY=0 NormalZ=1 AngleXU=0 Radius=1
    g38: BSplineCurve PolesCount=3 KnotsCount=2 Degree=2 IsPeriodic=0
    g39: GeomPoint [constr] X=-76.3837 Y=-22.6696 Z=0
    g40: GeomPoint [constr] X=-145.098 Y=-53.0183 Z=0
    g41: Circle [constr] CenterX=-115.652 CenterY=39.3447 CenterZ=0 NormalX=0 NormalY=0 NormalZ=1 AngleXU=0 Radius=1
    g42: Circle [constr] CenterX=-121.022 CenterY=-0.257645 CenterZ=0 NormalX=0 NormalY=0 NormalZ=1 AngleXU=0 Radius=1
    g43: Circle [constr] CenterX=-137.362 CenterY=-35.1519 CenterZ=0 NormalX=0 NormalY=0 NormalZ=1 AngleXU=0 Radius=1
    g44: BSplineCurve PolesCount=3 KnotsCount=2 Degree=2 IsPeriodic=0
    g45: GeomPoint [constr] X=-115.652 Y=39.3447 Z=0
    g46: GeomPoint [constr] X=-137.362 Y=-35.1519 Z=0
    g47: Circle [constr] CenterX=-137.362 CenterY=-35.1519 CenterZ=0 NormalX=0 NormalY=0 NormalZ=1 AngleXU=0 Radius=1
    g48: Circle [constr] CenterX=-120.373 CenterY=-15.8958 CenterZ=0 NormalX=0 NormalY=0 NormalZ=1 AngleXU=0 Radius=1
    g49: Circle [constr] CenterX=-88.6537 CenterY=-11.0397 CenterZ=0 NormalX=0 NormalY=0 NormalZ=1 AngleXU=0 Radius=1
    g50: BSplineCurve PolesCount=3 KnotsCount=2 Degree=2 IsPeriodic=0
    g51: GeomPoint [constr] X=-137.362 Y=-35.1519 Z=0
    g52: GeomPoint [constr] X=-88.6537 Y=-11.0397 Z=0
    g53: Circle [constr] CenterX=-88.6537 CenterY=-11.0397 CenterZ=0 NormalX=0 NormalY=0 NormalZ=1 AngleXU=0 Radius=1
    g54: Circle [constr] CenterX=-109.474 CenterY=13.1533 CenterZ=0 NormalX=0 NormalY=0 NormalZ=1 AngleXU=0 Radius=1
    g55: Circle [constr] CenterX=-115.652 CenterY=39.3447 CenterZ=0 NormalX=0 NormalY=0 NormalZ=1 AngleXU=0 Radius=1
    g56: BSplineCurve PolesCount=3 KnotsCount=2 Degree=2 IsPeriodic=0
    g57: GeomPoint [constr] X=-88.6537 Y=-11.0397 Z=0
    g58: GeomPoint [constr] X=-115.652 Y=39.3447 Z=0
    g59: Circle CenterX=-76 CenterY=-15.6 CenterZ=0 NormalX=0 NormalY=0 NormalZ=1 AngleXU=0 Radius=3.92
    g60: Circle CenterX=-116.828 CenterY=56.6638 CenterZ=0 NormalX=0 NormalY=0 NormalZ=1 AngleXU=0 Radius=1.5
    g61: Circle CenterX=-148.246 CenterY=-50.4227 CenterZ=0 NormalX=0 NormalY=0 NormalZ=1 AngleXU=0 Radius=1.5
    g62: ArcOfCircle CenterX=-76 CenterY=-15.6 CenterZ=0 NormalX=0 NormalY=0 NormalZ=1 AngleXU=0 Radius=7.08 StartAngle=4.65817 EndAngle=7.20054
  constraints (117):
    c: Weight(g0) = 1
    c: Equal(g0,g1)
    c: Equal(g0,g2)
    c: InternalAlignment(g0,g3)
    c: InternalAlignment(g1,g3)
    c: InternalAlignment(g2,g3)
    c: InternalAlignment(g4,g3)
    c: InternalAlignment(g5,g3)
    c: Coincident(g1,g-7)
    c: Weight(g6) = 1
    c: Equal(g6,g7)
    c: Equal(g6,g8)
    c: InternalAlignment(g6,g9)
    c: InternalAlignment(g7,g9)
    c: InternalAlignment(g8,g9)
    c: InternalAlignment(g10,g9)
    c: InternalAlignment(g11,g9)
    c: Coincident(g7,g-3)
    c: Weight(g12) = 1
    c: Equal(g12,g13)
    c: Equal(g12,g14)
    c: InternalAlignment(g12,g15)
    c: InternalAlignment(g13,g15)
    c: InternalAlignment(g14,g15)
    c: InternalAlignment(g16,g15)
    c: InternalAlignment(g17,g15)
    c: Coincident(g13,g-8)
    c: Tangent(g15,g-4) = 1.5708
    c: Tangent(g9,g-4) = -1.5708
    c: Tangent(g15,g-5) = 1.5708
    c: Tangent(g3,g-6) = -1.5708
    c: Tangent(g9,g-6) = -1.5708
    c: PointOnObject(g18,g9)
    c: PointOnObject(g18,g3)
    c: PointOnObject(g19,g9)
    c: PointOnObject(g19,g15)
    c: PointOnObject(g20,g15)
    c: PointOnObject(g20,g3)
    c: Coincident(g21,g-4)
    c: Coincident(g22,g-6)
    c: Weight(g23) = 1
    c: Equal(g23,g24)
    c: Equal(g23,g25)
    c: InternalAlignment(g23,g26)
    c: InternalAlignment(g24,g26)
    c: InternalAlignment(g25,g26)
    c: InternalAlignment(g27,g26)
    c: InternalAlignment(g28,g26)
    c: Coincident(g24,g-3)
    c: Tangent(g26,g22) = -1.5708
    c: Tangent(g26,g21) = -1.5708
    c: Weight(g29) = 1
    c: Equal(g29,g30)
    c: Equal(g29,g31)
    c: InternalAlignment(g29,g32)
    c: InternalAlignment(g30,g32)
    c: InternalAlignment(g31,g32)
    c: InternalAlignment(g33,g32)
    c: InternalAlignment(g34,g32)
    c: Coincident(g30,g-8)
    c: Weight(g35) = 1
    c: Equal(g35,g36)
    c: Equal(g35,g37)
    c: InternalAlignment(g35,g38)
    c: InternalAlignment(g36,g38)
    c: InternalAlignment(g37,g38)
    c: InternalAlignment(g39,g38)
    c: InternalAlignment(g40,g38)
    c: Coincident(g36,g-7)
    c: Tangent(g38,g22) = 1.5708
    c: Tangent(g32,g21) = 1.5708
    c: Diameter(g21) = 8.16
    c: Diameter(g22) = 8.16
    c: Weight(g41) = 1
    c: Equal(g41,g42)
    c: Equal(g41,g43)
    c: InternalAlignment(g41,g44)
    c: InternalAlignment(g42,g44)
    c: InternalAlignment(g43,g44)
    c: InternalAlignment(g45,g44)
    c: InternalAlignment(g46,g44)
    c: Coincident(g41,g19)
    c: Coincident(g43,g18)
    c: Coincident(g42,g7)
    c: Weight(g47) = 1
    c: Equal(g47,g48)
    c: Equal(g47,g49)
    c: InternalAlignment(g47,g50)
    c: InternalAlignment(g48,g50)
    c: InternalAlignment(g49,g50)
    c: InternalAlignment(g51,g50)
    c: InternalAlignment(g52,g50)
    c: Coincident(g47,g44)
    c: Coincident(g48,g1)
    c: Coincident(g49,g20)
    c: Weight(g53) = 1
    c: Equal(g53,g54)
    c: Equal(g53,g55)
    c: InternalAlignment(g53,g56)
    c: InternalAlignment(g54,g56)
    c: InternalAlignment(g55,g56)
    c: InternalAlignment(g57,g56)
    c: InternalAlignment(g58,g56)
    c: Coincident(g53,g50)
    c: Coincident(g54,g13)
    c: Coincident(g55,g44)
    c: Diameter(g59) = 7.84
    c: Coincident(g60,g21)
    c: Diameter(g60) = 3
    c: Coincident(g61,g22)
    c: Diameter(g61) = 3
    c: Coincident(g62,g59)
    c: Tangent(g38,g62) = 1.5708
    c: Coincident(g59,g-5)
    c: Tangent(g32,g62) = 1.5708
    c: Diameter(g62) = 14.16
    c: Tangent(g3,g-5) = -1.5708
FEATURE [Sketcher::SketchObject] Sketch068  label="v8-f"
  ArcFitTolerance = 1e-06
  AttachmentSupport = -> [XY_Plane005]
  ExternalGeometry = -> [Sketch063]
  FullyConstrained = true
  MakeInternals = false
  MapMode = 5
  expr: Constraints[4] = <<v8-Dimensions>>.joint3mmCut
  expr: Constraints[5] = <<v8-Dimensions>>.joint3mmEdge
  expr: Constraints[6] = <<v8-Dimensions>>.joint3mmCut
  expr: Constraints[7] = <<v8-Dimensions>>.joint3mmEdge
  sketch-geometry (16):
    g0: Circle CenterX=-148.246 CenterY=-50.4227 CenterZ=0 NormalX=0 NormalY=0 NormalZ=1 AngleXU=0 Radius=1.5
    g1: ArcOfCircle CenterX=-148.246 CenterY=-50.4227 CenterZ=0 NormalX=0 NormalY=0 NormalZ=1 AngleXU=0 Radius=4.08 StartAngle=0.220204 EndAngle=3.44357
    g2: ArcOfCircle CenterX=-148.246 CenterY=-129.223 CenterZ=0 NormalX=0 NormalY=0 NormalZ=1 AngleXU=0 Radius=4.08 StartAngle=2.83961 EndAngle=6.06298
    g3: Circle CenterX=-148.246 CenterY=-129.223 CenterZ=0 NormalX=0 NormalY=0 NormalZ=1 AngleXU=0 Radius=1.5
    g4: Circle [constr] CenterX=-144.264 CenterY=-49.5315 CenterZ=0 NormalX=0 NormalY=0 NormalZ=1 AngleXU=0 Radius=1
    g5: Circle [constr] CenterX=-135.246 CenterY=-89.8227 CenterZ=0 NormalX=0 NormalY=0 NormalZ=1 AngleXU=0 Radius=1
    g6: Circle [constr] CenterX=-144.264 CenterY=-130.114 CenterZ=0 NormalX=0 NormalY=0 NormalZ=1 AngleXU=0 Radius=1
    g7: BSplineCurve PolesCount=3 KnotsCount=2 Degree=2 IsPeriodic=0
    g8: GeomPoint [constr] X=-144.264 Y=-49.5315 Z=0
    g9: GeomPoint [constr] X=-144.264 Y=-130.114 Z=0
    g10: Circle [constr] CenterX=-152.141 CenterY=-128.009 CenterZ=0 NormalX=0 NormalY=0 NormalZ=1 AngleXU=0 Radius=1
    g11: Circle [constr] CenterX=-140.246 CenterY=-89.8227 CenterZ=0 NormalX=0 NormalY=0 NormalZ=1 AngleXU=0 Radius=1
    g12: Circle [constr] CenterX=-152.141 CenterY=-51.6361 CenterZ=0 NormalX=0 NormalY=0 NormalZ=1 AngleXU=0 Radius=1
    g13: BSplineCurve PolesCount=3 KnotsCount=2 Degree=2 IsPeriodic=0
    g14: GeomPoint [constr] X=-152.141 Y=-128.009 Z=0
    g15: GeomPoint [constr] X=-152.141 Y=-51.6361 Z=0
  constraints (30):
    c: Coincident(g0,g-3)
    c: Coincident(g1,g0)
    c: Coincident(g2,g-4)
    c: Coincident(g3,g2)
    c: Diameter(g3) = 3
    c: Diameter(g2) = 8.16
    c: Diameter(g0) = 3
    c: Diameter(g1) = 8.16
    c: Weight(g4) = 1
    c: Equal(g4,g5)
    c: Equal(g4,g6)
    c: InternalAlignment(g4,g7)
    c: InternalAlignment(g5,g7)
    c: InternalAlignment(g6,g7)
    c: InternalAlignment(g8,g7)
    c: InternalAlignment(g9,g7)
    c: Coincident(g5,g-5)
    c: Weight(g10) = 1
    c: Equal(g10,g11)
    c: Equal(g10,g12)
    c: InternalAlignment(g10,g13)
    c: InternalAlignment(g11,g13)
    c: InternalAlignment(g12,g13)
    c: InternalAlignment(g14,g13)
    c: InternalAlignment(g15,g13)
    c: Coincident(g11,g-5)
    c: Tangent(g13,g1) = 1.5708
    c: Tangent(g7,g1) = 1.5708
    c: Tangent(g13,g2) = 1.5708
    c: Tangent(g7,g2) = 1.5708
FEATURE [Sketcher::SketchObject] Sketch069  label="v8-c"
  ArcFitTolerance = 1e-06
  AttachmentSupport = -> [XY_Plane005]
  ExternalGeometry = -> [Sketch063]
  FullyConstrained = true
  MakeInternals = false
  MapMode = 5
  expr: Constraints[1] = <<v8-Dimensions>>.cJunctionCut
  expr: Constraints[28] = <<v8-Dimensions>>.cJunctionEdge
  expr: Constraints[29] = <<v8-Dimensions>>.joint3mmEdge
  expr: Constraints[2] = <<v8-Dimensions>>.joint3mmCut
  sketch-geometry (16):
    g0: Circle CenterX=-76 CenterY=-15.6 CenterZ=0 NormalX=0 NormalY=0 NormalZ=1 AngleXU=0 Radius=3.92
    g1: Circle CenterX=-83.9611 CenterY=-93.7958 CenterZ=0 NormalX=0 NormalY=0 NormalZ=1 AngleXU=0 Radius=1.5
    g2: ArcOfCircle CenterX=-76 CenterY=-15.6 CenterZ=0 NormalX=0 NormalY=0 NormalZ=1 AngleXU=0 Radius=7.08 StartAngle=5.80344 EndAngle=9.17574
    g3: ArcOfCircle CenterX=-83.9611 CenterY=-93.7958 CenterZ=0 NormalX=0 NormalY=0 NormalZ=1 AngleXU=0 Radius=4.08 StartAngle=3.26087 EndAngle=6.48445
    g4: Circle [constr] CenterX=-82.8616 CenterY=-13.855 CenterZ=0 NormalX=0 NormalY=0 NormalZ=1 AngleXU=0 Radius=1
    g5: Circle [constr] CenterX=-92.9137 CenterY=-53.3812 CenterZ=0 NormalX=0 NormalY=0 NormalZ=1 AngleXU=0 Radius=1
    g6: Circle [constr] CenterX=-88.0121 CenterY=-94.2813 CenterZ=0 NormalX=0 NormalY=0 NormalZ=1 AngleXU=0 Radius=1
    g7: BSplineCurve PolesCount=3 KnotsCount=2 Degree=2 IsPeriodic=0
    g8: GeomPoint [constr] X=-82.8616 Y=-13.855 Z=0
    g9: GeomPoint [constr] X=-88.0121 Y=-94.2813 Z=0
    g10: Circle [constr] CenterX=-79.9634 CenterY=-92.9802 CenterZ=0 NormalX=0 NormalY=0 NormalZ=1 AngleXU=0 Radius=1
    g11: Circle [constr] CenterX=-87.9394 CenterY=-53.8876 CenterZ=0 NormalX=0 NormalY=0 NormalZ=1 AngleXU=0 Radius=1
    g12: Circle [constr] CenterX=-69.7192 CenterY=-18.8678 CenterZ=0 NormalX=0 NormalY=0 NormalZ=1 AngleXU=0 Radius=1
    g13: BSplineCurve PolesCount=3 KnotsCount=2 Degree=2 IsPeriodic=0
    g14: GeomPoint [constr] X=-79.9634 Y=-92.9802 Z=0
    g15: GeomPoint [constr] X=-69.7192 Y=-18.8678 Z=0
  constraints (30):
    c: Coincident(g0,g-3)
    c: Diameter(g0) = 7.84
    c: Diameter(g1) = 3
    c: Coincident(g1,g-3)
    c: Coincident(g2,g0)
    c: Coincident(g3,g1)
    c: Weight(g4) = 1
    c: Equal(g4,g5)
    c: Equal(g4,g6)
    c: InternalAlignment(g4,g7)
    c: InternalAlignment(g5,g7)
    c: InternalAlignment(g6,g7)
    c: InternalAlignment(g8,g7)
    c: InternalAlignment(g9,g7)
    c: Coincident(g5,g-4)
    c: Weight(g10) = 1
    c: Equal(g10,g11)
    c: Equal(g10,g12)
    c: InternalAlignment(g10,g13)
    c: InternalAlignment(g11,g13)
    c: InternalAlignment(g12,g13)
    c: InternalAlignment(g14,g13)
    c: InternalAlignment(g15,g13)
    c: Coincident(g11,g-5)
    c: Tangent(g7,g2) = -1.5708
    c: Tangent(g13,g2) = -1.5708
    c: Tangent(g13,g3) = -1.5708
    c: Tangent(g7,g3) = -1.5708
    c: Diameter(g2) = 14.16
    c: Diameter(g3) = 8.16
FEATURE [Sketcher::SketchObject] Sketch070  label="v8-ghi"
  ArcFitTolerance = 1e-06
  AttachmentSupport = -> [XY_Plane005]
  ExternalGeometry = -> [Sketch063]
  FullyConstrained = true
  MakeInternals = false
  MapMode = 5
  expr: Constraints[0] = <<v8-Dimensions>>.joint3mmCut
  expr: Constraints[112] = <<v8-Dimensions>>.joint3mmEdge
  expr: Constraints[113] = <<v8-Dimensions>>.joint3mmEdge
  expr: Constraints[114] = <<v8-Dimensions>>.ghiFootRadius
  expr: Constraints[2] = <<v8-Dimensions>>.joint3mmCut
  sketch-geometry (62):
    g0: Circle CenterX=-83.9611 CenterY=-93.7958 CenterZ=0 NormalX=0 NormalY=0 NormalZ=1 AngleXU=0 Radius=1.5
    g1: Circle CenterX=-148.246 CenterY=-129.223 CenterZ=0 NormalX=0 NormalY=0 NormalZ=1 AngleXU=0 Radius=1.5
    g2: ArcOfCircle CenterX=-83.9611 CenterY=-93.7958 CenterZ=0 NormalX=0 NormalY=0 NormalZ=1 AngleXU=0 Radius=4.08 StartAngle=0.375119 EndAngle=2.39794
    g3: ArcOfCircle CenterX=-148.246 CenterY=-129.223 CenterZ=0 NormalX=0 NormalY=0 NormalZ=1 AngleXU=0 Radius=4.08 StartAngle=1.75102 EndAngle=4.60318
    g4: ArcOfCircle CenterX=-24.9107 CenterY=-170.201 CenterZ=0 NormalX=0 NormalY=0 NormalZ=1 AngleXU=0 Radius=1.5 StartAngle=4.21934 EndAngle=7.17154
    g5: Circle [constr] CenterX=-81.2604 CenterY=-96.7464 CenterZ=0 NormalX=0 NormalY=0 NormalZ=1 AngleXU=0 Radius=1
    g6: Circle [constr] CenterX=-109.829 CenterY=-122.895 CenterZ=0 NormalX=0 NormalY=0 NormalZ=1 AngleXU=0 Radius=1
    g7: Circle [constr] CenterX=-147.193 CenterY=-133.082 CenterZ=0 NormalX=0 NormalY=0 NormalZ=1 AngleXU=0 Radius=1
    g8: BSplineCurve [constr] PolesCount=3 KnotsCount=2 Degree=2 IsPeriodic=0
    g9: GeomPoint [constr] X=-81.2604 Y=-96.7464 Z=0
    g10: GeomPoint [constr] X=-147.193 Y=-133.082 Z=0
    g11: Circle [constr] CenterX=-87.5799 CenterY=-95.5 CenterZ=0 NormalX=0 NormalY=0 NormalZ=1 AngleXU=0 Radius=1
    g12: Circle [constr] CenterX=-66.1336 CenterY=-141.039 CenterZ=0 NormalX=0 NormalY=0 NormalZ=1 AngleXU=0 Radius=1
    g13: Circle [constr] CenterX=-25.813 CenterY=-171.399 CenterZ=0 NormalX=0 NormalY=0 NormalZ=1 AngleXU=0 Radius=1
    g14: BSplineCurve [constr] PolesCount=3 KnotsCount=2 Degree=2 IsPeriodic=0
    g15: GeomPoint [constr] X=-87.5799 Y=-95.5 Z=0
    g16: GeomPoint [constr] X=-25.813 Y=-171.399 Z=0
    g17: Circle [constr] CenterX=-24.1628 CenterY=-168.901 CenterZ=0 NormalX=0 NormalY=0 NormalZ=1 AngleXU=0 Radius=1
    g18: Circle [constr] CenterX=-81.9167 CenterY=-135.682 CenterZ=0 NormalX=0 NormalY=0 NormalZ=1 AngleXU=0 Radius=1
    g19: Circle [constr] CenterX=-147.62 CenterY=-125.272 CenterZ=0 NormalX=0 NormalY=0 NormalZ=1 AngleXU=0 Radius=1
    g20: BSplineCurve [constr] PolesCount=3 KnotsCount=2 Degree=2 IsPeriodic=0
    g21: GeomPoint [constr] X=-24.1628 Y=-168.901 Z=0
    g22: GeomPoint [constr] X=-147.62 Y=-125.272 Z=0
    g23: GeomPoint [constr] X=-38.4745 Y=-161.082 Z=0
    g24: GeomPoint [constr] X=-85.2528 Y=-100.286 Z=0
    g25: GeomPoint [constr] X=-131.914 Y=-128.109 Z=0
    g26: Circle [constr] CenterX=-25.6207 CenterY=-171.522 CenterZ=0 NormalX=0 NormalY=0 NormalZ=1 AngleXU=0 Radius=1
    g27: Circle [constr] CenterX=-83.4932 CenterY=-140.427 CenterZ=0 NormalX=0 NormalY=0 NormalZ=1 AngleXU=0 Radius=1
    g28: Circle [constr] CenterX=-148.69 CenterY=-133.278 CenterZ=0 NormalX=0 NormalY=0 NormalZ=1 AngleXU=0 Radius=1
    g29: BSplineCurve PolesCount=3 KnotsCount=2 Degree=2 IsPeriodic=0
    g30: GeomPoint [constr] X=-25.6207 Y=-171.522 Z=0
    g31: GeomPoint [constr] X=-148.69 Y=-133.278 Z=0
    g32: Circle [constr] CenterX=-148.977 CenterY=-125.209 CenterZ=0 NormalX=0 NormalY=0 NormalZ=1 AngleXU=0 Radius=1
    g33: Circle [constr] CenterX=-112.242 CenterY=-118.516 CenterZ=0 NormalX=0 NormalY=0 NormalZ=1 AngleXU=0 Radius=1
    g34: Circle [constr] CenterX=-86.964 CenterY=-91.0337 CenterZ=0 NormalX=0 NormalY=0 NormalZ=1 AngleXU=0 Radius=1
    g35: BSplineCurve PolesCount=3 KnotsCount=2 Degree=2 IsPeriodic=0
    g36: GeomPoint [constr] X=-148.977 Y=-125.209 Z=0
    g37: GeomPoint [constr] X=-86.964 Y=-91.0337 Z=0
    g38: Circle [constr] CenterX=-80.1648 CenterY=-92.3009 CenterZ=0 NormalX=0 NormalY=0 NormalZ=1 AngleXU=0 Radius=1
    g39: Circle [constr] CenterX=-62.1774 CenterY=-137.982 CenterZ=0 NormalX=0 NormalY=0 NormalZ=1 AngleXU=0 Radius=1
    g40: Circle [constr] CenterX=-23.9647 CenterY=-169.037 CenterZ=0 NormalX=0 NormalY=0 NormalZ=1 AngleXU=0 Radius=1
    g41: BSplineCurve PolesCount=3 KnotsCount=2 Degree=2 IsPeriodic=0
    g42: GeomPoint [constr] X=-80.1648 Y=-92.3009 Z=0
    g43: GeomPoint [constr] X=-23.9647 Y=-169.037 Z=0
    g44: Circle [constr] CenterX=-131.914 CenterY=-128.109 CenterZ=0 NormalX=0 NormalY=0 NormalZ=1 AngleXU=0 Radius=1
    g45: Circle [constr] CenterX=-109.829 CenterY=-122.895 CenterZ=0 NormalX=0 NormalY=0 NormalZ=1 AngleXU=0 Radius=1
    g46: Circle [constr] CenterX=-85.2528 CenterY=-100.286 CenterZ=0 NormalX=0 NormalY=0 NormalZ=1 AngleXU=0 Radius=1
    g47: BSplineCurve PolesCount=3 KnotsCount=2 Degree=2 IsPeriodic=0
    g48: GeomPoint [constr] X=-131.914 Y=-128.109 Z=0
    g49: GeomPoint [constr] X=-85.2528 Y=-100.286 Z=0
    g50: Circle [constr] CenterX=-85.2528 CenterY=-100.286 CenterZ=0 NormalX=0 NormalY=0 NormalZ=1 AngleXU=0 Radius=1
    g51: Circle [constr] CenterX=-66.1336 CenterY=-141.039 CenterZ=0 NormalX=0 NormalY=0 NormalZ=1 AngleXU=0 Radius=1
    g52: Circle [constr] CenterX=-38.4745 CenterY=-161.082 CenterZ=0 NormalX=0 NormalY=0 NormalZ=1 AngleXU=0 Radius=1
    g53: BSplineCurve PolesCount=3 KnotsCount=2 Degree=2 IsPeriodic=0
    g54: GeomPoint [constr] X=-85.2528 Y=-100.286 Z=0
    g55: GeomPoint [constr] X=-38.4745 Y=-161.082 Z=0
    g56: Circle [constr] CenterX=-38.4745 CenterY=-161.082 CenterZ=0 NormalX=0 NormalY=0 NormalZ=1 AngleXU=0 Radius=1
    g57: Circle [constr] CenterX=-81.9167 CenterY=-135.682 CenterZ=0 NormalX=0 NormalY=0 NormalZ=1 AngleXU=0 Radius=1
    g58: Circle [constr] CenterX=-131.914 CenterY=-128.109 CenterZ=0 NormalX=0 NormalY=0 NormalZ=1 AngleXU=0 Radius=1
    g59: BSplineCurve PolesCount=3 KnotsCount=2 Degree=2 IsPeriodic=0
    g60: GeomPoint [constr] X=-38.4745 Y=-161.082 Z=0
    g61: GeomPoint [constr] X=-131.914 Y=-128.109 Z=0
  constraints (115):
    c: Diameter(g0) = 3
    c: Coincident(g0,g-4)
    c: Diameter(g1) = 3
    c: Coincident(g1,g-3)
    c: Coincident(g2,g0)
    c: Coincident(g3,g1)
    c: Coincident(g4,g-6)
    c: Weight(g5) = 1
    c: Equal(g5,g6)
    c: Equal(g5,g7)
    c: InternalAlignment(g5,g8)
    c: InternalAlignment(g6,g8)
    c: InternalAlignment(g7,g8)
    c: InternalAlignment(g9,g8)
    c: InternalAlignment(g10,g8)
    c: Coincident(g6,g-7)
    c: Weight(g11) = 1
    c: Equal(g11,g12)
    c: Equal(g11,g13)
    c: InternalAlignment(g11,g14)
    c: InternalAlignment(g12,g14)
    c: InternalAlignment(g13,g14)
    c: InternalAlignment(g15,g14)
    c: InternalAlignment(g16,g14)
    c: Coincident(g12,g-9)
    c: Weight(g17) = 1
    c: Equal(g17,g18)
    c: Equal(g17,g19)
    c: InternalAlignment(g17,g20)
    c: InternalAlignment(g18,g20)
    c: InternalAlignment(g19,g20)
    c: InternalAlignment(g21,g20)
    c: InternalAlignment(g22,g20)
    c: Coincident(g18,g-8)
    c: Tangent(g20,g-12) = -1.5708
    c: Tangent(g8,g-12) = 1.5708
    c: Tangent(g14,g-11) = -1.5708
    c: Tangent(g8,g-11) = 1.5708
    c: Tangent(g20,g-10) = -1.5708
    c: Tangent(g14,g-10) = -1.5708
    c: PointOnObject(g23,g14)
    c: PointOnObject(g23,g20)
    c: PointOnObject(g24,g8)
    c: PointOnObject(g24,g14)
    c: PointOnObject(g25,g8)
    c: PointOnObject(g25,g20)
    c: Weight(g26) = 1
    c: Equal(g26,g27)
    c: Equal(g26,g28)
    c: InternalAlignment(g26,g29)
    c: InternalAlignment(g27,g29)
    c: InternalAlignment(g28,g29)
    c: InternalAlignment(g30,g29)
    c: InternalAlignment(g31,g29)
    c: Coincident(g27,g-8)
    c: Weight(g32) = 1
    c: Equal(g32,g33)
    c: Equal(g32,g34)
    c: InternalAlignment(g32,g35)
    c: InternalAlignment(g33,g35)
    c: InternalAlignment(g34,g35)
    c: InternalAlignment(g36,g35)
    c: InternalAlignment(g37,g35)
    c: Coincident(g33,g-7)
    c: Weight(g38) = 1
    c: Equal(g38,g39)
    c: Equal(g38,g40)
    c: InternalAlignment(g38,g41)
    c: InternalAlignment(g39,g41)
    c: InternalAlignment(g40,g41)
    c: InternalAlignment(g42,g41)
    c: InternalAlignment(g43,g41)
    c: Coincident(g39,g-9)
    c: Tangent(g41,g4) = 1.5708
    c: Tangent(g29,g4) = 1.5708
    c: Tangent(g29,g3) = 1.5708
    c: Tangent(g35,g3) = 1.5708
    c: Tangent(g35,g2) = 1.5708
    c: Tangent(g41,g2) = 1.5708
    c: Weight(g44) = 1
    c: Equal(g44,g45)
    c: Equal(g44,g46)
    c: InternalAlignment(g44,g47)
    c: InternalAlignment(g45,g47)
    c: InternalAlignment(g46,g47)
    c: InternalAlignment(g48,g47)
    c: InternalAlignment(g49,g47)
    c: Coincident(g44,g25)
    c: Coincident(g45,g6)
    c: Coincident(g46,g24)
    c: Weight(g50) = 1
    c: Equal(g50,g51)
    c: Equal(g50,g52)
    c: InternalAlignment(g50,g53)
    c: InternalAlignment(g51,g53)
    c: InternalAlignment(g52,g53)
    c: InternalAlignment(g54,g53)
    c: InternalAlignment(g55,g53)
    c: Coincident(g50,g47)
    c: Coincident(g51,g12)
    c: Coincident(g52,g23)
    c: Weight(g56) = 1
    c: Equal(g56,g57)
    c: Equal(g56,g58)
    c: InternalAlignment(g56,g59)
    c: InternalAlignment(g57,g59)
    c: InternalAlignment(g58,g59)
    c: InternalAlignment(g60,g59)
    c: InternalAlignment(g61,g59)
    c: Coincident(g56,g23)
    c: Coincident(g57,g18)
    c: Coincident(g58,g47)
    c: Diameter(g2) = 8.16
    c: Diameter(g3) = 8.16
    c: Radius(g4) = 1.5
FEATURE [Sketcher::SketchObject] Sketch071  label="v8-a1"
  ArcFitTolerance = 1e-06
  AttachmentSupport = -> [XY_Plane005]
  ExternalGeometry = -> [Sketch063]
  FullyConstrained = true
  MakeInternals = false
  MapMode = 5
  expr: Constraints[1] = <<v8-Dimensions>>.crankBearingCut
  expr: Constraints[2] = <<v8-Dimensions>>.aJunctionCut
  expr: Constraints[5] = <<v8-Dimensions>>.aMotorShaftDiameter
  expr: Constraints[73] = <<v8-Dimensions>>.aJunctionEdge
  expr: Constraints[74] = <<v8-Dimensions>>.aJunctionEdge
  expr: Constraints[76] = <<v8-Dimensions>>.aLowerSupportAnchorDrop
  expr: Constraints[77] = <<v8-Dimensions>>.aLowerSupportAnchors
  expr: Constraints[89] = <<v8-Dimensions>>.tabWidthCut
  expr: Constraints[8] = <<v8-Dimensions>>.aLowerSupportCut
  expr: Constraints[90] = <<v8-Dimensions>>.tabHeightCut
  sketch-geometry (44):
    g0: Circle CenterX=0 CenterY=0 CenterZ=0 NormalX=0 NormalY=0 NormalZ=1 AngleXU=0 Radius=4.92
    g1: Circle CenterX=-76 CenterY=-15.6 CenterZ=0 NormalX=0 NormalY=0 NormalZ=1 AngleXU=0 Radius=1.92
    g2: Circle CenterX=76 CenterY=-15.6 CenterZ=0 NormalX=0 NormalY=0 NormalZ=1 AngleXU=0 Radius=1.92
    g3: Circle CenterX=0 CenterY=66 CenterZ=0 NormalX=0 NormalY=0 NormalZ=1 AngleXU=0 Radius=1.5
    g4: Circle CenterX=0 CenterY=-70 CenterZ=0 NormalX=0 NormalY=0 NormalZ=1 AngleXU=0 Radius=1.92
    g5-g9: Circle [constr] x5 (B-spline internal-alignment scaffolding for g10; pole/knot coordinates omitted)
    g10: BSplineCurve PolesCount=5 KnotsCount=3 Degree=3 IsPeriodic=0
    g11: GeomPoint [constr] X=-34.08 Y=84.66 Z=0
    g12: GeomPoint [constr] X=-13.02 Y=53.25 Z=0
    g13: GeomPoint [constr] X=-76.751 Y=-10.5758 Z=0
    g14-g18: Circle [constr] x5 (B-spline internal-alignment scaffolding for g19; pole/knot coordinates omitted)
    g19: BSplineCurve PolesCount=5 KnotsCount=3 Degree=3 IsPeriodic=0
    g20: GeomPoint [constr] X=34.08 Y=84.66 Z=0
    g21: GeomPoint [constr] X=13.02 Y=53.25 Z=0
    g22: GeomPoint [constr] X=76.751 Y=-10.5758 Z=0
    g23: LineSegment StartX=-34.08 StartY=84.66 StartZ=0 EndX=34.08 EndY=84.66 EndZ=0
    g24-g29: Circle [constr] x6 (B-spline internal-alignment scaffolding for g30; pole/knot coordinates omitted)
    g30: BSplineCurve PolesCount=6 KnotsCount=4 Degree=3 IsPeriodic=0
    g31-g34: GeomPoint [constr] x4 (B-spline internal-alignment scaffolding for g30; pole/knot coordinates omitted)
    g35: ArcOfCircle CenterX=76 CenterY=-15.6 CenterZ=0 NormalX=0 NormalY=0 NormalZ=1 AngleXU=0 Radius=5.08 StartAngle=4.71239 EndAngle=7.7056
    g36: ArcOfCircle CenterX=-76 CenterY=-15.6 CenterZ=0 NormalX=0 NormalY=0 NormalZ=1 AngleXU=0 Radius=5.08 StartAngle=1.71918 EndAngle=4.71239
    g37: LineSegment StartX=-2.92 StartY=75.08 StartZ=0 EndX=2.92 EndY=75.08 EndZ=0
    g38: LineSegment StartX=2.92 StartY=75.08 StartZ=0 EndX=2.92 EndY=77.92 EndZ=0
    g39: LineSegment StartX=2.92 StartY=77.92 StartZ=0 EndX=-2.92 EndY=77.92 EndZ=0
    g40: LineSegment StartX=-2.92 StartY=77.92 StartZ=0 EndX=-2.92 EndY=75.08 EndZ=0
    g41: GeomPoint [constr] X=0 Y=76.5 Z=0
    g42: Circle [constr] CenterX=0 CenterY=0 CenterZ=0 NormalX=0 NormalY=0 NormalZ=1 AngleXU=0 Radius=56.6
    g43: Circle [constr] CenterX=0 CenterY=66 CenterZ=0 NormalX=0 NormalY=0 NormalZ=1 AngleXU=0 Radius=12.6
  constraints (70):
    c: Coincident(g0,g-1)
    c: Diameter(g0) = 9.84
    c: Diameter(g1) = 3.84
    c: Coincident(g1,g-19)
    c: Equal(g2,g1)
    c: Diameter(g3) = 3
    c: Coincident(g3,g-5)
    c: Coincident(g4,g-4)
    c: Diameter(g4) = 3.84
    c: Weight(g5) = 1
    c: Equal(g5, g6-g9) x4
    c: InternalAlignment(g5-g9 -> g10) x5
    c: InternalAlignment(g11,g10)
    c: InternalAlignment(g12,g10)
    c: InternalAlignment(g13,g10)
    c: Vertical(g10,g6)
    c: Horizontal(g6,g-22)
    c: Coincident(g10,g-7)
    c: Coincident(g7,g-22)
    c: PointOnObject(g8,g-1)
    c: Vertical(g8,g7)
    c: Weight(g14) = 1
    c: Equal(g14, g15-g18) x4
    c: InternalAlignment(g14-g18 -> g19) x5
    c: InternalAlignment(g20,g19)
    c: InternalAlignment(g21,g19)
    c: InternalAlignment(g22,g19)
    c: Coincident(g14,g-11)
    c: Coincident(g16,g-23)
    c: PointOnObject(g17,g-1)
    c: Vertical(g15,g19)
    c: Horizontal(g15,g16)
    c: Vertical(g16,g17)
    c: Coincident(g23,g10)
    c: Coincident(g23,g19)
    c: Weight(g24) = 1
    c: Equal(g24, g25-g29) x5
    c: InternalAlignment(g24-g29 -> g30) x6
    c: InternalAlignment(g31-g34 -> g30) x4
    c: Symmetric(g26,g27,g-2)
    c: Symmetric(g25,g28,g-2)
    c: Coincident(g36,g1)
    c: Tangent(g10,g36) = -1.5708
    c: Tangent(g30,g36) = -1.5708
    c: Tangent(g30,g35) = -1.5708
    c: Tangent(g19,g35) = 1.5708
    c: Horizontal(g28,g30)
    c: Diameter(g36) = 10.16
    c: Diameter(g35) = 10.16
    c: Vertical(g26,g25)
    c: DistanceY(g26,g4) = 8
    c: DistanceX(g26,g27) = 25
    c: Coincident(g2,g35)
    c: Coincident(g-17,g2)
    c: Coincident(g37,g38)
    c: Coincident(g38,g39)
    c: Coincident(g39,g40)
    c: Coincident(g40,g37)
    c: Horizontal(g37)
    c: Horizontal(g39)
    c: Vertical(g38)
    c: Vertical(g40)
    c: Symmetric(g39,g37,g41)
    c: Distance(g38,g40) = 5.84
    c: Distance(g37,g39) = 2.84
    c: Coincident(g41,g-20)
    c: Diameter(g42) = 113.2
    c: Coincident(g42,g0)
    c: Diameter(g43) = 25.2
    c: Coincident(g43,g3)
FEATURE [Spreadsheet::Sheet] Spreadsheet  label="v8-Dimensions"
  cells = A1='kerf; B1(kerf)=0.08; A2='mLength; B2(mLength)=30; A3='mDiameterCut; B3(mDiameterCut)==6 - 0.16; A4='mDiameterEdge; B4(mDiameterEdge)==15 + 2 * kerf; A5='mMidWidth; B5(mMidWidth)=5; A6='jLength; B6(jLength)=100; A7='jBearingCut; B7(jBearingCut)==10 - 0.16; A8='jDiameterCut; B8(jDiameterCut)=3; A9='jDiameterEdge; B9(jDiameterEdge)==8 + 0.16; A10='jBendPoint; B10(jBendPoint)=45; A11='jBendWidth; B11(jBendWidth)=4; A12='jBendOffset; B12(jBendOffset)=15; A13='kBearingCut; B13(kBearingCut)==jBearingCut; A14='kDiameterCut; B14(kDiameterCut)==jDiameterCut; A15='kDiameterEdge; B15(kDiameterEdge)==jDiameterEdge; A16='kBendPoint; B16(kBendPoint)=55; A17='kBendWidth; B17(kBendWidth)=4; A18='kBendOffset; B18(kBendOffset)=15; A19='bLength; B19(bLength)=83; A20='bBendWidth; B20(bBendWidth)=5; A21='bBendOffset; B21(bBendOffset)=10; A22='dLength; B22(dLength)=80.2; A23='dBendWidth; B23(dBendWidth)=5; A24='dBendOffset; B24(dBendOffset)=14; A25='eLength; B25(eLength)=111.6; A26='eBendWidth; B26(eBendWidth)=4; A27='eBendOffset; B27(eBendOffset)=8; A28='bdeDiameterCut; B28(bdeDiameterCut)==jDiameterCut; A29='bdeDiameterEdge; B29(bdeDiameterEdge)==jDiameterEdge; A30='bdeJunctionCut; B30(bdeJunctionCut)==8 - 0.16; A31='bdeJunctionEdge; B31(bdeJunctionEdge)==14 + kerf * 2; A32='frame4mmCut; B32(frame4mmCut)==4 - 0.16; A33='frame4mmEdge; B33(frame4mmEdge)==8 + 0.16; A34='fLength; B34(fLength)=78.8; A35='fBendWidth; B35(fBendWidth)=5; A36='fBendOffset; B36(fBendOffset)=8; A37='cLength; B37(cLength)=78.6; A38='cBendWidth; B38(cBendWidth)=5; A39='cBendOffset; B39(cBendOffset)=8; A40='cJunctionCut; B40(cJunctionCut)==bdeJunctionCut; A41='cJunctionEdge; B41(cJunctionEdge)==bdeJunctionEdge; A42='gLength; B42(gLength)=73.4; A43='gBendWidth; B43(gBendWidth)=5; A44='gBendOffset; B44(gBendOffset)=8; A45='hLength; B45(hLength)=131.4; A46='hBendWidth; B46(hBendWidth)=5; A47='hBendOffset; B47(hBendOffset)=10; A48='iLength; B48(iLength)=98; A49='iBendWidth; B49(iBendWidth)=5; A50='iBendOffset; B50(iBendOffset)=10; A51='ghiFootRadius; B51(ghiFootRadius)=1.5; A52='joint3mmCut; B52(joint3mmCut)=3; A53='joint3mmEdge; B53(joint3mmEdge)==8 + 0.16; A54='aLowerSupportDrop; B54(aLowerSupportDrop)=70; A55='aLowerSupportDiameter; B55(aLowerSupportDiameter)=4; A56='aLowerSupportCut; B56(aLowerSupportCut)==aLowerSupportDiameter - kerf * 2; A57='aLowerSupportEdge; B57(aLowerSupportEdge)==aLowerSupportDiameter + kerf * 2; A58='aLowerSupportAnchors; B58(aLowerSupportAnchors)=25; A59='aLowerSupportAnchorDrop; B59(aLowerSupportAnchorDrop)=8; A60='aGearDistance; B60(aGearDistance)=66; A61='aMotorShaftDiameter; B61(aMotorShaftDiameter)=3; A62='aMotorWidthDiameter; B62(aMotorWidthDiameter)=12; A63='aMotorWidthCut; B63(aMotorWidthCut)==aMotorWidthDiameter - kerf * 2; A64='aMotorHeight; B64(aMotorHeight)=10; A65='aMotorHeightCut; B65(aMotorHeightCut)==aMotorHeight - kerf * 2; A66='aMotorToTabCenterDistance; B66(aMotorToTabCenterDistance)==1.5 + 5 + 4; A67='aJunctionCut; B67(aJunctionCut)==4 - kerf * 2; A68='aJunctionEdge; B68(aJunctionEdge)==4 + 6 + kerf * 2; A69='crankBearingCut; B69(crankBearingCut)==10 - kerf * 2; A70='crankBearingEdge; B70(crankBearingEdge)==crankBearingCut + 5; A71='tabWidth; B71(tabWidth)=6; A72='tabWidthCut; B72(tabWidthCut)==tabWidth - kerf * 2; A73='tabHeight; B73(tabHeight)=3; A74='tabHeightCut; B74(tabHeightCut)==tabHeight - kerf * 2; A75='tabDistance; B75(tabDistance)=4; A76='tabDistanceCut; B76(tabDistanceCut)==tabDistance + kerf * 2; A77='solarTabWidth; B77(solarTabWidth)=38; A78='solarTabWidthCut; B78(solarTabWidthCut)==solarTabWidth + kerf * 2; A79='solarSideWidth; B79(solarSideWidth)=4; A80='solarSideWidthCut; B80(solarSideWidthCut)==solarSideWidth + kerf * 2; A81='solarPanelWidth; B81(solarPanelWidth)=60; A82='solarPanelWidthCut; B82(solarPanelWidthCut)==solarPanelWidth - kerf * 2; A83='solarPanelDepth; B83(solarPanelDepth)=2.5; A84='solarPanelDepthCut; B84(solarPanelDepthCut)==solarPanelDepth + kerf * 2; A85='wireHole; B85(wireHole)=6; A86='wireHoleCut; B86(wireHoleCut)==wireHole - kerf * 2; A87='largeGearOuterDiameter; B87(largeGearOuterDiameter)=113.354; A88='largeGearInnerDiameter; B88(largeGearInnerDiameter)==largeGearOuterDiameter - 30; A89='largeGearHubDiameter; B89(largeGearHubDiameter)=6; A90='largeGearSpokeWidth; B90(largeGearSpokeWidth)=7; A91='largeGearSpokeHub; B91(largeGearSpokeHub)=15; A92='smallGearOuterDiameter; B92(smallGearOuterDiameter)=25.3; A93='smallGearHubDiameter; B93(smallGearHubDiameter)=3
FEATURE [Sketcher::SketchObject] Sketch072  label="v8-a2"
  ArcFitTolerance = 1e-06
  AttachmentSupport = -> [XY_Plane005]
  ExternalGeometry = -> [Sketch063]
  FullyConstrained = true
  MakeInternals = false
  MapMode = 5
  expr: Constraints[100] = <<v8-Dimensions>>.aMotorWidthCut
  expr: Constraints[101] = <<v8-Dimensions>>.aMotorHeightCut
  expr: Constraints[1] = <<v8-Dimensions>>.crankBearingCut
  expr: Constraints[2] = <<v8-Dimensions>>.aJunctionCut
  expr: Constraints[69] = <<v8-Dimensions>>.aJunctionEdge
  expr: Constraints[6] = <<v8-Dimensions>>.aLowerSupportCut
  expr: Constraints[70] = <<v8-Dimensions>>.aJunctionEdge
  expr: Constraints[72] = <<v8-Dimensions>>.aLowerSupportAnchorDrop
  expr: Constraints[73] = <<v8-Dimensions>>.aLowerSupportAnchors
  expr: Constraints[85] = <<v8-Dimensions>>.tabWidthCut
  expr: Constraints[86] = <<v8-Dimensions>>.tabHeightCut
  sketch-geometry (52):
    g0: Circle CenterX=0 CenterY=0 CenterZ=0 NormalX=0 NormalY=0 NormalZ=1 AngleXU=0 Radius=4.92
    g1: Circle CenterX=-76 CenterY=-15.6 CenterZ=0 NormalX=0 NormalY=0 NormalZ=1 AngleXU=0 Radius=1.92
    g2: Circle CenterX=76 CenterY=-15.6 CenterZ=0 NormalX=0 NormalY=0 NormalZ=1 AngleXU=0 Radius=1.92
    g3: Circle CenterX=0 CenterY=-70 CenterZ=0 NormalX=0 NormalY=0 NormalZ=1 AngleXU=0 Radius=1.92
    g4-g8: Circle [constr] x5 (B-spline internal-alignment scaffolding for g9; pole/knot coordinates omitted)
    g9: BSplineCurve PolesCount=5 KnotsCount=3 Degree=3 IsPeriodic=0
    g10: GeomPoint [constr] X=-34.08 Y=84.66 Z=0
    g11: GeomPoint [constr] X=-13.02 Y=53.25 Z=0
    g12: GeomPoint [constr] X=-76.751 Y=-10.5758 Z=0
    g13-g17: Circle [constr] x5 (B-spline internal-alignment scaffolding for g18; pole/knot coordinates omitted)
    g18: BSplineCurve PolesCount=5 KnotsCount=3 Degree=3 IsPeriodic=0
    g19: GeomPoint [constr] X=34.08 Y=84.66 Z=0
    g20: GeomPoint [constr] X=13.02 Y=53.25 Z=0
    g21: GeomPoint [constr] X=76.751 Y=-10.5758 Z=0
    g22-g27: Circle [constr] x6 (B-spline internal-alignment scaffolding for g28; pole/knot coordinates omitted)
    g28: BSplineCurve PolesCount=6 KnotsCount=4 Degree=3 IsPeriodic=0
    g29-g32: GeomPoint [constr] x4 (B-spline internal-alignment scaffolding for g28; pole/knot coordinates omitted)
    g33: ArcOfCircle CenterX=76 CenterY=-15.6 CenterZ=0 NormalX=0 NormalY=0 NormalZ=1 AngleXU=0 Radius=5.08 StartAngle=4.71239 EndAngle=7.7056
    g34: ArcOfCircle CenterX=-76 CenterY=-15.6 CenterZ=0 NormalX=0 NormalY=0 NormalZ=1 AngleXU=0 Radius=5.08 StartAngle=1.71918 EndAngle=4.71239
    g35: LineSegment StartX=-2.92 StartY=75.08 StartZ=0 EndX=2.92 EndY=75.08 EndZ=0
    g36: LineSegment StartX=2.92 StartY=75.08 StartZ=0 EndX=2.92 EndY=77.92 EndZ=0
    g37: LineSegment StartX=2.92 StartY=77.92 StartZ=0 EndX=-2.92 EndY=77.92 EndZ=0
    g38: LineSegment StartX=-2.92 StartY=77.92 StartZ=0 EndX=-2.92 EndY=75.08 EndZ=0
    g39: GeomPoint [constr] X=0 Y=76.5 Z=0
    g40: Circle [constr] CenterX=0 CenterY=0 CenterZ=0 NormalX=0 NormalY=0 NormalZ=1 AngleXU=0 Radius=56.6
    g41: Circle [constr] CenterX=0 CenterY=66 CenterZ=0 NormalX=0 NormalY=0 NormalZ=1 AngleXU=0 Radius=12.6
    g42: LineSegment StartX=-5.92 StartY=61.08 StartZ=0 EndX=5.92 EndY=61.08 EndZ=0
    g43: LineSegment StartX=5.92 StartY=61.08 StartZ=0 EndX=5.92 EndY=70.92 EndZ=0
    g44: LineSegment StartX=5.92 StartY=70.92 StartZ=0 EndX=-5.92 EndY=70.92 EndZ=0
    g45: LineSegment StartX=-5.92 StartY=70.92 StartZ=0 EndX=-5.92 EndY=61.08 EndZ=0
    g46: GeomPoint [constr] X=0 Y=66 Z=0
    g47: LineSegment StartX=-34.08 StartY=84.66 StartZ=0 EndX=-29.92 EndY=84.66 EndZ=0
    g48: LineSegment StartX=-29.92 StartY=84.66 StartZ=0 EndX=-29.92 EndY=82.16 EndZ=0
    g49: LineSegment StartX=-29.92 StartY=82.16 StartZ=0 EndX=29.92 EndY=82.16 EndZ=0
    g50: LineSegment StartX=29.92 StartY=82.16 StartZ=0 EndX=29.92 EndY=84.66 EndZ=0
    g51: LineSegment StartX=29.92 StartY=84.66 StartZ=0 EndX=34.08 EndY=84.66 EndZ=0
  constraints (88):
    c: Coincident(g0,g-1)
    c: Diameter(g0) = 9.84
    c: Diameter(g1) = 3.84
    c: Coincident(g1,g-19)
    c: Equal(g2,g1)
    c: Coincident(g3,g-4)
    c: Diameter(g3) = 3.84
    c: Weight(g4) = 1
    c: Equal(g4, g5-g8) x4
    c: InternalAlignment(g4-g8 -> g9) x5
    c: InternalAlignment(g10,g9)
    c: InternalAlignment(g11,g9)
    c: InternalAlignment(g12,g9)
    c: Vertical(g9,g5)
    c: Horizontal(g5,g-22)
    c: Coincident(g9,g-7)
    c: Coincident(g6,g-22)
    c: PointOnObject(g7,g-1)
    c: Vertical(g7,g6)
    c: Weight(g13) = 1
    c: Equal(g13, g14-g17) x4
    c: InternalAlignment(g13-g17 -> g18) x5
    c: InternalAlignment(g19,g18)
    c: InternalAlignment(g20,g18)
    c: InternalAlignment(g21,g18)
    c: Coincident(g13,g-11)
    c: Coincident(g15,g-23)
    c: PointOnObject(g16,g-1)
    c: Vertical(g14,g18)
    c: Horizontal(g14,g15)
    c: Vertical(g15,g16)
    c: Weight(g22) = 1
    c: Equal(g22, g23-g27) x5
    c: InternalAlignment(g22-g27 -> g28) x6
    c: InternalAlignment(g29-g32 -> g28) x4
    c: Symmetric(g24,g25,g-2)
    c: Symmetric(g23,g26,g-2)
    c: Coincident(g34,g1)
    c: Tangent(g9,g34) = -1.5708
    c: Tangent(g28,g34) = -1.5708
    c: Tangent(g28,g33) = -1.5708
    c: Tangent(g18,g33) = 1.5708
    c: Horizontal(g26,g28)
    c: Diameter(g34) = 10.16
    c: Diameter(g33) = 10.16
    c: Vertical(g24,g23)
    c: DistanceY(g24,g3) = 8
    c: DistanceX(g24,g25) = 25
    c: Coincident(g2,g33)
    c: Coincident(g-17,g2)
    c: Coincident(g35,g36)
    c: Coincident(g36,g37)
    c: Coincident(g37,g38)
    c: Coincident(g38,g35)
    c: Horizontal(g35)
    c: Horizontal(g37)
    c: Vertical(g36)
    c: Vertical(g38)
    c: Symmetric(g37,g35,g39)
    c: Distance(g36,g38) = 5.84
    c: Distance(g35,g37) = 2.84
    c: Coincident(g39,g-20)
    c: Diameter(g40) = 113.2
    c: Coincident(g40,g0)
    c: Diameter(g41) = 25.2
    c: Coincident(g42,g43)
    c: Coincident(g43,g44)
    c: Coincident(g44,g45)
    c: Coincident(g45,g42)
    c: Horizontal(g42)
    c: Horizontal(g44)
    c: Vertical(g43)
    c: Vertical(g45)
    c: Symmetric(g44,g42,g46)
    c: DistanceX(g44,g44) = 11.84
    c: DistanceY(g45,g45) = 9.84
    c: Coincident(g47,g9)
    c: Coincident(g47,g-6)
    c: Coincident(g48,g47)
    c: Coincident(g48,g-8)
    c: Coincident(g49,g48)
    c: Coincident(g49,g-9)
    c: Coincident(g50,g49)
    c: Coincident(g50,g-10)
    c: Coincident(g51,g50)
    c: Coincident(g51,g18)
    c: Coincident(g46,g41)
    c: Coincident(g41,g-5)
FEATURE [Sketcher::SketchObject] Sketch073  label="v8-a3"
  ArcFitTolerance = 1e-06
  AttachmentSupport = -> [XY_Plane005]
  ExternalGeometry = -> [Sketch063]
  FullyConstrained = true
  MakeInternals = false
  MapMode = 5
  expr: Constraints[103] = <<v8-Dimensions>>.wireHoleCut
  expr: Constraints[1] = <<v8-Dimensions>>.crankBearingCut
  expr: Constraints[2] = <<v8-Dimensions>>.aJunctionCut
  expr: Constraints[69] = <<v8-Dimensions>>.aJunctionEdge
  expr: Constraints[6] = <<v8-Dimensions>>.aLowerSupportCut
  expr: Constraints[70] = <<v8-Dimensions>>.aJunctionEdge
  expr: Constraints[72] = <<v8-Dimensions>>.aLowerSupportAnchorDrop
  expr: Constraints[73] = <<v8-Dimensions>>.aLowerSupportAnchors
  expr: Constraints[85] = <<v8-Dimensions>>.tabWidthCut
  expr: Constraints[86] = <<v8-Dimensions>>.tabHeightCut
  sketch-geometry (49):
    g0: Circle CenterX=0 CenterY=0 CenterZ=0 NormalX=0 NormalY=0 NormalZ=1 AngleXU=0 Radius=4.92
    g1: Circle CenterX=-76 CenterY=-15.6 CenterZ=0 NormalX=0 NormalY=0 NormalZ=1 AngleXU=0 Radius=1.92
    g2: Circle CenterX=76 CenterY=-15.6 CenterZ=0 NormalX=0 NormalY=0 NormalZ=1 AngleXU=0 Radius=1.92
    g3: Circle CenterX=0 CenterY=-70 CenterZ=0 NormalX=0 NormalY=0 NormalZ=1 AngleXU=0 Radius=1.92
    g4-g8: Circle [constr] x5 (B-spline internal-alignment scaffolding for g9; pole/knot coordinates omitted)
    g9: BSplineCurve PolesCount=5 KnotsCount=3 Degree=3 IsPeriodic=0
    g10: GeomPoint [constr] X=-34.08 Y=84.66 Z=0
    g11: GeomPoint [constr] X=-13.02 Y=53.25 Z=0
    g12: GeomPoint [constr] X=-76.751 Y=-10.5758 Z=0
    g13-g17: Circle [constr] x5 (B-spline internal-alignment scaffolding for g18; pole/knot coordinates omitted)
    g18: BSplineCurve PolesCount=5 KnotsCount=3 Degree=3 IsPeriodic=0
    g19: GeomPoint [constr] X=34.08 Y=84.66 Z=0
    g20: GeomPoint [constr] X=13.02 Y=53.25 Z=0
    g21: GeomPoint [constr] X=76.751 Y=-10.5758 Z=0
    g22-g27: Circle [constr] x6 (B-spline internal-alignment scaffolding for g28; pole/knot coordinates omitted)
    g28: BSplineCurve PolesCount=6 KnotsCount=4 Degree=3 IsPeriodic=0
    g29-g32: GeomPoint [constr] x4 (B-spline internal-alignment scaffolding for g28; pole/knot coordinates omitted)
    g33: ArcOfCircle CenterX=76 CenterY=-15.6 CenterZ=0 NormalX=0 NormalY=0 NormalZ=1 AngleXU=0 Radius=5.08 StartAngle=4.71239 EndAngle=7.7056
    g34: ArcOfCircle CenterX=-76 CenterY=-15.6 CenterZ=0 NormalX=0 NormalY=0 NormalZ=1 AngleXU=0 Radius=5.08 StartAngle=1.71918 EndAngle=4.71239
    g35: LineSegment StartX=-2.92 StartY=75.08 StartZ=0 EndX=2.92 EndY=75.08 EndZ=0
    g36: LineSegment StartX=2.92 StartY=75.08 StartZ=0 EndX=2.92 EndY=77.92 EndZ=0
    g37: LineSegment StartX=2.92 StartY=77.92 StartZ=0 EndX=-2.92 EndY=77.92 EndZ=0
    g38: LineSegment StartX=-2.92 StartY=77.92 StartZ=0 EndX=-2.92 EndY=75.08 EndZ=0
    g39: GeomPoint [constr] X=0 Y=76.5 Z=0
    g40: Circle [constr] CenterX=0 CenterY=0 CenterZ=0 NormalX=0 NormalY=0 NormalZ=1 AngleXU=0 Radius=56.6
    g41: Circle [constr] CenterX=0 CenterY=66 CenterZ=0 NormalX=0 NormalY=0 NormalZ=1 AngleXU=0 Radius=12.6
    g42: GeomPoint [constr] X=0 Y=66 Z=0
    g43: LineSegment StartX=-34.08 StartY=84.66 StartZ=0 EndX=-29.92 EndY=84.66 EndZ=0
    g44: LineSegment StartX=-29.92 StartY=84.66 StartZ=0 EndX=-29.92 EndY=82.16 EndZ=0
    g45: LineSegment StartX=-29.92 StartY=82.16 StartZ=0 EndX=29.92 EndY=82.16 EndZ=0
    g46: LineSegment StartX=29.92 StartY=82.16 StartZ=0 EndX=29.92 EndY=84.66 EndZ=0
    g47: LineSegment StartX=29.92 StartY=84.66 StartZ=0 EndX=34.08 EndY=84.66 EndZ=0
    g48: Circle CenterX=0 CenterY=66 CenterZ=0 NormalX=0 NormalY=0 NormalZ=1 AngleXU=0 Radius=2.92
  constraints (79):
    c: Coincident(g0,g-1)
    c: Diameter(g0) = 9.84
    c: Diameter(g1) = 3.84
    c: Coincident(g1,g-19)
    c: Equal(g2,g1)
    c: Coincident(g3,g-4)
    c: Diameter(g3) = 3.84
    c: Weight(g4) = 1
    c: Equal(g4, g5-g8) x4
    c: InternalAlignment(g4-g8 -> g9) x5
    c: InternalAlignment(g10,g9)
    c: InternalAlignment(g11,g9)
    c: InternalAlignment(g12,g9)
    c: Vertical(g9,g5)
    c: Horizontal(g5,g-22)
    c: Coincident(g9,g-7)
    c: Coincident(g6,g-22)
    c: PointOnObject(g7,g-1)
    c: Vertical(g7,g6)
    c: Weight(g13) = 1
    c: Equal(g13, g14-g17) x4
    c: InternalAlignment(g13-g17 -> g18) x5
    c: InternalAlignment(g19,g18)
    c: InternalAlignment(g20,g18)
    c: InternalAlignment(g21,g18)
    c: Coincident(g13,g-11)
    c: Coincident(g15,g-23)
    c: PointOnObject(g16,g-1)
    c: Vertical(g14,g18)
    c: Horizontal(g14,g15)
    c: Vertical(g15,g16)
    c: Weight(g22) = 1
    c: Equal(g22, g23-g27) x5
    c: InternalAlignment(g22-g27 -> g28) x6
    c: InternalAlignment(g29-g32 -> g28) x4
    c: Symmetric(g24,g25,g-2)
    c: Symmetric(g23,g26,g-2)
    c: Coincident(g34,g1)
    c: Tangent(g9,g34) = -1.5708
    c: Tangent(g28,g34) = -1.5708
    c: Tangent(g28,g33) = -1.5708
    c: Tangent(g18,g33) = 1.5708
    c: Horizontal(g26,g28)
    c: Diameter(g34) = 10.16
    c: Diameter(g33) = 10.16
    c: Vertical(g24,g23)
    c: DistanceY(g24,g3) = 8
    c: DistanceX(g24,g25) = 25
    c: Coincident(g2,g33)
    c: Coincident(g-17,g2)
    c: Coincident(g35,g36)
    c: Coincident(g36,g37)
    c: Coincident(g37,g38)
    c: Coincident(g38,g35)
    c: Horizontal(g35)
    c: Horizontal(g37)
    c: Vertical(g36)
    c: Vertical(g38)
    c: Symmetric(g37,g35,g39)
    c: Distance(g36,g38) = 5.84
    c: Distance(g35,g37) = 2.84
    c: Coincident(g39,g-20)
    c: Diameter(g40) = 113.2
    c: Coincident(g40,g0)
    c: Diameter(g41) = 25.2
    c: Coincident(g43,g9)
    c: Coincident(g43,g-6)
    c: Coincident(g44,g43)
    c: Coincident(g44,g-8)
    c: Coincident(g45,g44)
    c: Coincident(g45,g-9)
    c: Coincident(g46,g45)
    c: Coincident(g46,g-10)
    c: Coincident(g47,g46)
    c: Coincident(g47,g18)
    c: Coincident(g42,g41)
    c: Coincident(g41,g-5)
    c: Diameter(g48) = 5.84
    c: Coincident(g48,g41)
FEATURE [Sketcher::SketchObject] Sketch074  label="v8-a4"
  ArcFitTolerance = 1e-06
  AttachmentSupport = -> [XY_Plane005]
  ExternalGeometry = -> [Sketch063]
  FullyConstrained = true
  MakeInternals = false
  MapMode = 5
  expr: Constraints[1] = <<v8-Dimensions>>.crankBearingCut
  expr: Constraints[2] = <<v8-Dimensions>>.aJunctionCut
  expr: Constraints[69] = <<v8-Dimensions>>.aJunctionEdge
  expr: Constraints[6] = <<v8-Dimensions>>.aLowerSupportCut
  expr: Constraints[70] = <<v8-Dimensions>>.aJunctionEdge
  expr: Constraints[72] = <<v8-Dimensions>>.aLowerSupportAnchorDrop
  expr: Constraints[73] = <<v8-Dimensions>>.aLowerSupportAnchors
  sketch-geometry (44):
    g0: Circle CenterX=0 CenterY=0 CenterZ=0 NormalX=0 NormalY=0 NormalZ=1 AngleXU=0 Radius=4.92
    g1: Circle CenterX=-76 CenterY=-15.6 CenterZ=0 NormalX=0 NormalY=0 NormalZ=1 AngleXU=0 Radius=1.92
    g2: Circle CenterX=76 CenterY=-15.6 CenterZ=0 NormalX=0 NormalY=0 NormalZ=1 AngleXU=0 Radius=1.92
    g3: Circle CenterX=0 CenterY=-70 CenterZ=0 NormalX=0 NormalY=0 NormalZ=1 AngleXU=0 Radius=1.92
    g4-g8: Circle [constr] x5 (B-spline internal-alignment scaffolding for g9; pole/knot coordinates omitted)
    g9: BSplineCurve PolesCount=5 KnotsCount=3 Degree=3 IsPeriodic=0
    g10: GeomPoint [constr] X=-34.08 Y=84.66 Z=0
    g11: GeomPoint [constr] X=-13.02 Y=53.25 Z=0
    g12: GeomPoint [constr] X=-76.751 Y=-10.5758 Z=0
    g13-g17: Circle [constr] x5 (B-spline internal-alignment scaffolding for g18; pole/knot coordinates omitted)
    g18: BSplineCurve PolesCount=5 KnotsCount=3 Degree=3 IsPeriodic=0
    g19: GeomPoint [constr] X=34.08 Y=84.66 Z=0
    g20: GeomPoint [constr] X=13.02 Y=53.25 Z=0
    g21: GeomPoint [constr] X=76.751 Y=-10.5758 Z=0
    g22-g27: Circle [constr] x6 (B-spline internal-alignment scaffolding for g28; pole/knot coordinates omitted)
    g28: BSplineCurve PolesCount=6 KnotsCount=4 Degree=3 IsPeriodic=0
    g29-g32: GeomPoint [constr] x4 (B-spline internal-alignment scaffolding for g28; pole/knot coordinates omitted)
    g33: ArcOfCircle CenterX=76 CenterY=-15.6 CenterZ=0 NormalX=0 NormalY=0 NormalZ=1 AngleXU=0 Radius=5.08 StartAngle=4.71239 EndAngle=7.7056
    g34: ArcOfCircle CenterX=-76 CenterY=-15.6 CenterZ=0 NormalX=0 NormalY=0 NormalZ=1 AngleXU=0 Radius=5.08 StartAngle=1.71918 EndAngle=4.71239
    g35: GeomPoint [constr] X=0 Y=76.5 Z=0
    g36: Circle [constr] CenterX=0 CenterY=0 CenterZ=0 NormalX=0 NormalY=0 NormalZ=1 AngleXU=0 Radius=56.6
    g37: Circle [constr] CenterX=0 CenterY=66 CenterZ=0 NormalX=0 NormalY=0 NormalZ=1 AngleXU=0 Radius=12.6
    g38: GeomPoint [constr] X=0 Y=66 Z=0
    g39: LineSegment StartX=-34.08 StartY=84.66 StartZ=0 EndX=-29.92 EndY=84.66 EndZ=0
    g40: LineSegment StartX=-29.92 StartY=84.66 StartZ=0 EndX=-29.92 EndY=82.16 EndZ=0
    g41: LineSegment StartX=-29.92 StartY=82.16 StartZ=0 EndX=29.92 EndY=82.16 EndZ=0
    g42: LineSegment StartX=29.92 StartY=82.16 StartZ=0 EndX=29.92 EndY=84.66 EndZ=0
    g43: LineSegment StartX=29.92 StartY=84.66 StartZ=0 EndX=34.08 EndY=84.66 EndZ=0
  constraints (66):
    c: Coincident(g0,g-1)
    c: Diameter(g0) = 9.84
    c: Diameter(g1) = 3.84
    c: Coincident(g1,g-19)
    c: Equal(g2,g1)
    c: Coincident(g3,g-4)
    c: Diameter(g3) = 3.84
    c: Weight(g4) = 1
    c: Equal(g4, g5-g8) x4
    c: InternalAlignment(g4-g8 -> g9) x5
    c: InternalAlignment(g10,g9)
    c: InternalAlignment(g11,g9)
    c: InternalAlignment(g12,g9)
    c: Vertical(g9,g5)
    c: Horizontal(g5,g-22)
    c: Coincident(g9,g-7)
    c: Coincident(g6,g-22)
    c: PointOnObject(g7,g-1)
    c: Vertical(g7,g6)
    c: Weight(g13) = 1
    c: Equal(g13, g14-g17) x4
    c: InternalAlignment(g13-g17 -> g18) x5
    c: InternalAlignment(g19,g18)
    c: InternalAlignment(g20,g18)
    c: InternalAlignment(g21,g18)
    c: Coincident(g13,g-11)
    c: Coincident(g15,g-23)
    c: PointOnObject(g16,g-1)
    c: Vertical(g14,g18)
    c: Horizontal(g14,g15)
    c: Vertical(g15,g16)
    c: Weight(g22) = 1
    c: Equal(g22, g23-g27) x5
    c: InternalAlignment(g22-g27 -> g28) x6
    c: InternalAlignment(g29-g32 -> g28) x4
    c: Symmetric(g24,g25,g-2)
    c: Symmetric(g23,g26,g-2)
    c: Coincident(g34,g1)
    c: Tangent(g9,g34) = -1.5708
    c: Tangent(g28,g34) = -1.5708
    c: Tangent(g28,g33) = -1.5708
    c: Tangent(g18,g33) = 1.5708
    c: Horizontal(g26,g28)
    c: Diameter(g34) = 10.16
    c: Diameter(g33) = 10.16
    c: Vertical(g24,g23)
    c: DistanceY(g24,g3) = 8
    c: DistanceX(g24,g25) = 25
    c: Coincident(g2,g33)
    c: Coincident(g-17,g2)
    c: Coincident(g35,g-20)
    c: Diameter(g36) = 113.2
    c: Coincident(g36,g0)
    c: Diameter(g37) = 25.2
    c: Coincident(g39,g9)
    c: Coincident(g39,g-6)
    c: Coincident(g40,g39)
    c: Coincident(g40,g-8)
    c: Coincident(g41,g40)
    c: Coincident(g41,g-9)
    c: Coincident(g42,g41)
    c: Coincident(g42,g-10)
    c: Coincident(g43,g42)
    c: Coincident(g43,g18)
    c: Coincident(g38,g37)
    c: Coincident(g37,g-5)
FEATURE [Sketcher::SketchObject] Sketch075  label="v8-a5"
  ArcFitTolerance = 1e-06
  AttachmentSupport = -> [XY_Plane005]
  ExternalGeometry = -> [Sketch063]
  FullyConstrained = true
  MakeInternals = false
  MapMode = 5
  expr: Constraints[109] = <<v8-Dimensions>>.tabHeightCut
  expr: Constraints[110] = <<v8-Dimensions>>.tabHeightCut
  expr: Constraints[112] = <<v8-Dimensions>>.tabWidthCut
  expr: Constraints[113] = <<v8-Dimensions>>.tabWidthCut
  expr: Constraints[1] = <<v8-Dimensions>>.crankBearingCut
  expr: Constraints[2] = <<v8-Dimensions>>.aJunctionCut
  expr: Constraints[69] = <<v8-Dimensions>>.aJunctionEdge
  expr: Constraints[6] = <<v8-Dimensions>>.aLowerSupportCut
  expr: Constraints[70] = <<v8-Dimensions>>.aJunctionEdge
  expr: Constraints[72] = <<v8-Dimensions>>.aLowerSupportAnchorDrop
  expr: Constraints[73] = <<v8-Dimensions>>.aLowerSupportAnchors
  sketch-geometry (52):
    g0: Circle CenterX=0 CenterY=0 CenterZ=0 NormalX=0 NormalY=0 NormalZ=1 AngleXU=0 Radius=4.92
    g1: Circle CenterX=-76 CenterY=-15.6 CenterZ=0 NormalX=0 NormalY=0 NormalZ=1 AngleXU=0 Radius=1.92
    g2: Circle CenterX=76 CenterY=-15.6 CenterZ=0 NormalX=0 NormalY=0 NormalZ=1 AngleXU=0 Radius=1.92
    g3: Circle CenterX=0 CenterY=-70 CenterZ=0 NormalX=0 NormalY=0 NormalZ=1 AngleXU=0 Radius=1.92
    g4-g8: Circle [constr] x5 (B-spline internal-alignment scaffolding for g9; pole/knot coordinates omitted)
    g9: BSplineCurve PolesCount=5 KnotsCount=3 Degree=3 IsPeriodic=0
    g10: GeomPoint [constr] X=-34.08 Y=84.66 Z=0
    g11: GeomPoint [constr] X=-13.02 Y=53.25 Z=0
    g12: GeomPoint [constr] X=-76.751 Y=-10.5758 Z=0
    g13-g17: Circle [constr] x5 (B-spline internal-alignment scaffolding for g18; pole/knot coordinates omitted)
    g18: BSplineCurve PolesCount=5 KnotsCount=3 Degree=3 IsPeriodic=0
    g19: GeomPoint [constr] X=34.08 Y=84.66 Z=0
    g20: GeomPoint [constr] X=13.02 Y=53.25 Z=0
    g21: GeomPoint [constr] X=76.751 Y=-10.5758 Z=0
    g22-g27: Circle [constr] x6 (B-spline internal-alignment scaffolding for g28; pole/knot coordinates omitted)
    g28: BSplineCurve PolesCount=6 KnotsCount=4 Degree=3 IsPeriodic=0
    g29-g32: GeomPoint [constr] x4 (B-spline internal-alignment scaffolding for g28; pole/knot coordinates omitted)
    g33: ArcOfCircle CenterX=76 CenterY=-15.6 CenterZ=0 NormalX=0 NormalY=0 NormalZ=1 AngleXU=0 Radius=5.08 StartAngle=4.71239 EndAngle=7.7056
    g34: ArcOfCircle CenterX=-76 CenterY=-15.6 CenterZ=0 NormalX=0 NormalY=0 NormalZ=1 AngleXU=0 Radius=5.08 StartAngle=1.71918 EndAngle=4.71239
    g35: GeomPoint [constr] X=0 Y=76.5 Z=0
    g36: Circle [constr] CenterX=0 CenterY=0 CenterZ=0 NormalX=0 NormalY=0 NormalZ=1 AngleXU=0 Radius=56.6
    g37: Circle [constr] CenterX=0 CenterY=66 CenterZ=0 NormalX=0 NormalY=0 NormalZ=1 AngleXU=0 Radius=12.6
    g38: GeomPoint [constr] X=0 Y=66 Z=0
    g39: LineSegment StartX=-34.08 StartY=84.66 StartZ=0 EndX=-29.92 EndY=84.66 EndZ=0
    g40: LineSegment StartX=-29.92 StartY=84.66 StartZ=0 EndX=-29.92 EndY=82.16 EndZ=0
    g41: LineSegment StartX=-29.92 StartY=82.16 StartZ=0 EndX=29.92 EndY=82.16 EndZ=0
    g42: LineSegment StartX=29.92 StartY=82.16 StartZ=0 EndX=29.92 EndY=84.66 EndZ=0
    g43: LineSegment StartX=29.92 StartY=84.66 StartZ=0 EndX=34.08 EndY=84.66 EndZ=0
    g44: LineSegment StartX=19.08 StartY=77.92 StartZ=0 EndX=19.08 EndY=72.08 EndZ=0
    g45: LineSegment StartX=19.08 StartY=72.08 StartZ=0 EndX=21.92 EndY=72.08 EndZ=0
    g46: LineSegment StartX=21.92 StartY=72.08 StartZ=0 EndX=21.92 EndY=77.92 EndZ=0
    g47: LineSegment StartX=21.92 StartY=77.92 StartZ=0 EndX=19.08 EndY=77.92 EndZ=0
    g48: LineSegment StartX=-21.92 StartY=77.92 StartZ=0 EndX=-21.92 EndY=72.08 EndZ=0
    g49: LineSegment StartX=-21.92 StartY=72.08 StartZ=0 EndX=-19.08 EndY=72.08 EndZ=0
    g50: LineSegment StartX=-19.08 StartY=72.08 StartZ=0 EndX=-19.08 EndY=77.92 EndZ=0
    g51: LineSegment StartX=-19.08 StartY=77.92 StartZ=0 EndX=-21.92 EndY=77.92 EndZ=0
  constraints (88):
    c: Coincident(g0,g-1)
    c: Diameter(g0) = 9.84
    c: Diameter(g1) = 3.84
    c: Coincident(g1,g-19)
    c: Equal(g2,g1)
    c: Coincident(g3,g-4)
    c: Diameter(g3) = 3.84
    c: Weight(g4) = 1
    c: Equal(g4, g5-g8) x4
    c: InternalAlignment(g4-g8 -> g9) x5
    c: InternalAlignment(g10,g9)
    c: InternalAlignment(g11,g9)
    c: InternalAlignment(g12,g9)
    c: Vertical(g9,g5)
    c: Horizontal(g5,g-22)
    c: Coincident(g9,g-7)
    c: Coincident(g6,g-22)
    c: PointOnObject(g7,g-1)
    c: Vertical(g7,g6)
    c: Weight(g13) = 1
    c: Equal(g13, g14-g17) x4
    c: InternalAlignment(g13-g17 -> g18) x5
    c: InternalAlignment(g19,g18)
    c: InternalAlignment(g20,g18)
    c: InternalAlignment(g21,g18)
    c: Coincident(g13,g-11)
    c: Coincident(g15,g-23)
    c: PointOnObject(g16,g-1)
    c: Vertical(g14,g18)
    c: Horizontal(g14,g15)
    c: Vertical(g15,g16)
    c: Weight(g22) = 1
    c: Equal(g22, g23-g27) x5
    c: InternalAlignment(g22-g27 -> g28) x6
    c: InternalAlignment(g29-g32 -> g28) x4
    c: Symmetric(g24,g25,g-2)
    c: Symmetric(g23,g26,g-2)
    c: Coincident(g34,g1)
    c: Tangent(g9,g34) = -1.5708
    c: Tangent(g28,g34) = -1.5708
    c: Tangent(g28,g33) = -1.5708
    c: Tangent(g18,g33) = 1.5708
    c: Horizontal(g26,g28)
    c: Diameter(g34) = 10.16
    c: Diameter(g33) = 10.16
    c: Vertical(g24,g23)
    c: DistanceY(g24,g3) = 8
    c: DistanceX(g24,g25) = 25
    c: Coincident(g2,g33)
    c: Coincident(g-17,g2)
    c: Coincident(g35,g-20)
    c: Diameter(g36) = 113.2
    c: Coincident(g36,g0)
    c: Diameter(g37) = 25.2
    c: Coincident(g39,g9)
    c: Coincident(g39,g-6)
    c: Coincident(g40,g39)
    c: Coincident(g40,g-8)
    c: Coincident(g41,g40)
    c: Coincident(g41,g-9)
    c: Coincident(g42,g41)
    c: Coincident(g42,g-10)
    c: Coincident(g43,g42)
    c: Coincident(g43,g18)
    c: Coincident(g38,g37)
    c: Coincident(g37,g-5)
    c: Coincident(g44,g45)
    c: Coincident(g45,g46)
    c: Coincident(g46,g47)
    c: Coincident(g47,g44)
    c: Vertical(g44)
    c: Vertical(g46)
    c: Horizontal(g45)
    c: Horizontal(g47)
    c: Coincident(g48,g49)
    c: Coincident(g49,g50)
    c: Coincident(g50,g51)
    c: Coincident(g51,g48)
    c: Vertical(g48)
    c: Vertical(g50)
    c: Horizontal(g49)
    c: Horizontal(g51)
    c: Coincident(g50,g-27)
    c: DistanceX(g51,g51) = 2.84
    c: DistanceX(g47,g47) = 2.84
    c: Coincident(g44,g-26)
    c: DistanceY(g48,g48) = 5.84
    c: DistanceY(g44,g44) = 5.84
FEATURE [Sketcher::SketchObject] Sketch076  label="v8-a6"
  ArcFitTolerance = 1e-06
  AttachmentSupport = -> [XY_Plane005]
  ExternalGeometry = -> [Sketch063]
  FullyConstrained = true
  MakeInternals = false
  MapMode = 5
  expr: Constraints[1] = <<v8-Dimensions>>.crankBearingCut
  expr: Constraints[29] = <<v8-Dimensions>>.aJunctionEdge
  expr: Constraints[2] = <<v8-Dimensions>>.aJunctionCut
  expr: Constraints[30] = <<v8-Dimensions>>.aJunctionEdge
  expr: Constraints[32] = <<v8-Dimensions>>.aLowerSupportAnchorDrop
  expr: Constraints[33] = <<v8-Dimensions>>.aLowerSupportAnchors
  expr: Constraints[6] = <<v8-Dimensions>>.aLowerSupportCut
  sketch-geometry (28):
    g0: Circle CenterX=0 CenterY=0 CenterZ=0 NormalX=0 NormalY=0 NormalZ=1 AngleXU=0 Radius=4.92
    g1: Circle CenterX=-76 CenterY=-15.6 CenterZ=0 NormalX=0 NormalY=0 NormalZ=1 AngleXU=0 Radius=1.92
    g2: Circle CenterX=76 CenterY=-15.6 CenterZ=0 NormalX=0 NormalY=0 NormalZ=1 AngleXU=0 Radius=1.92
    g3: Circle CenterX=0 CenterY=-70 CenterZ=0 NormalX=0 NormalY=0 NormalZ=1 AngleXU=0 Radius=1.92
    g4-g9: Circle [constr] x6 (B-spline internal-alignment scaffolding for g10; pole/knot coordinates omitted)
    g10: BSplineCurve PolesCount=6 KnotsCount=4 Degree=3 IsPeriodic=0
    g11-g14: GeomPoint [constr] x4 (B-spline internal-alignment scaffolding for g10; pole/knot coordinates omitted)
    g15: ArcOfCircle CenterX=76 CenterY=-15.6 CenterZ=0 NormalX=0 NormalY=0 NormalZ=1 AngleXU=0 Radius=5.08 StartAngle=4.71239 EndAngle=7.85398
    g16: ArcOfCircle CenterX=-76 CenterY=-15.6 CenterZ=0 NormalX=0 NormalY=0 NormalZ=1 AngleXU=0 Radius=5.08 StartAngle=1.5708 EndAngle=4.71239
    g17: Circle [constr] CenterX=0 CenterY=0 CenterZ=0 NormalX=0 NormalY=0 NormalZ=1 AngleXU=0 Radius=56.6
    g18-g22: Circle [constr] x5 (B-spline internal-alignment scaffolding for g23; pole/knot coordinates omitted)
    g23: BSplineCurve PolesCount=5 KnotsCount=3 Degree=3 IsPeriodic=0
    g24: GeomPoint [constr] X=76 Y=-10.52 Z=0
    g25: GeomPoint [constr] X=0 Y=8.74 Z=0
    g26: GeomPoint [constr] X=-76 Y=-10.52 Z=0
    g27: GeomPoint [constr] X=0 Y=4.92 Z=0
  constraints (41):
    c: Coincident(g0,g-1)
    c: Diameter(g0) = 9.84
    c: Diameter(g1) = 3.84
    c: Coincident(g1,g-8)
    c: Equal(g2,g1)
    c: Coincident(g3,g-4)
    c: Diameter(g3) = 3.84
    c: Weight(g4) = 1
    c: Equal(g4, g5-g9) x5
    c: InternalAlignment(g4-g9 -> g10) x6
    c: InternalAlignment(g11-g14 -> g10) x4
    c: Symmetric(g6,g7,g-2)
    c: Symmetric(g5,g8,g-2)
    c: Coincident(g16,g1)
    c: Tangent(g10,g16) = -1.5708
    c: Tangent(g10,g15) = -1.5708
    c: Horizontal(g8,g10)
    c: Diameter(g16) = 10.16
    c: Diameter(g15) = 10.16
    c: Vertical(g6,g5)
    c: DistanceY(g6,g3) = 8
    c: DistanceX(g6,g7) = 25
    c: Coincident(g2,g15)
    c: Coincident(g-6,g2)
    c: Diameter(g17) = 113.2
    c: Coincident(g17,g0)
    c: Weight(g18) = 1
    c: Equal(g18, g19-g22) x4
    c: InternalAlignment(g18-g22 -> g23) x5
    c: InternalAlignment(g24,g23)
    c: InternalAlignment(g25,g23)
    c: InternalAlignment(g26,g23)
    c: PointOnObject(g20,g-2)
    c: Horizontal(g19,g23)
    c: Symmetric(g21,g19,g-2)
    c: DistanceY(g0,g20) = 28
    c: DistanceX(g21,g19) = 72
    c: Tangent(g23,g15) = -1.5708
    c: Tangent(g23,g16) = -1.5708
    c: PointOnObject(g27,g0)
    c: PointOnObject(g27,g-2)
FEATURE [Sketcher::SketchObject] Sketch077  label="v8-motor-brace"
  ArcFitTolerance = 1e-06
  AttachmentSupport = -> [YZ_Plane005]
  ExternalGeometry = -> [Sketch063]
  FullyConstrained = true
  MakeInternals = false
  MapMode = 5
  Placement = pos=(0,0,0) rot=(0.57735,0.57735,0.57735;2.0944rad)
  expr: Constraints[0] = <<v8-Dimensions>>.tabWidth + <<v8-Dimensions>>.kerf * 2
  expr: Constraints[23] = <<v8-Dimensions>>.tabHeight + <<v8-Dimensions>>.kerf * 2
  expr: Constraints[25] = <<v8-Dimensions>>.tabWidth + <<v8-Dimensions>>.kerf * 2
  expr: Constraints[41] = <<v8-Dimensions>>.tabWidthCut
  expr: Constraints[42] = <<v8-Dimensions>>.tabHeightCut
  expr: Constraints[7] = <<v8-Dimensions>>.solarTabWidthCut
  sketch-geometry (22):
    g0: LineSegment StartX=71.76 StartY=0 StartZ=0 EndX=71.76 EndY=6.16 EndZ=0
    g1: LineSegment StartX=71.76 StartY=0 StartZ=0 EndX=77.92 EndY=0 EndZ=0
    g2: LineSegment StartX=77.92 StartY=0 StartZ=0 EndX=77.92 EndY=6.16 EndZ=0
    g3: LineSegment StartX=77.92 StartY=6.16 StartZ=0 EndX=81.08 EndY=6.16 EndZ=0
    g4: LineSegment StartX=81.08 StartY=6.16 StartZ=0 EndX=81.08 EndY=44.32 EndZ=0
    g5: LineSegment StartX=81.08 StartY=44.32 StartZ=0 EndX=77.92 EndY=44.32 EndZ=0
    g6: LineSegment StartX=77.92 StartY=44.32 StartZ=0 EndX=77.92 EndY=47.48 EndZ=0
    g7: LineSegment StartX=77.92 StartY=47.48 StartZ=0 EndX=71.76 EndY=47.48 EndZ=0
    g8: LineSegment StartX=71.76 StartY=47.48 StartZ=0 EndX=71.76 EndY=44.32 EndZ=0
    g9: LineSegment StartX=68.6 StartY=44.32 StartZ=0 EndX=68.6 EndY=6.16 EndZ=0
    g10: LineSegment StartX=68.6 StartY=6.16 StartZ=0 EndX=71.76 EndY=6.16 EndZ=0
    g11: LineSegment StartX=68.6 StartY=44.32 StartZ=0 EndX=71.76 EndY=44.32 EndZ=0
    g12: LineSegment StartX=71.76 StartY=13.48 StartZ=0 EndX=77.6 EndY=13.48 EndZ=0
    g13: LineSegment StartX=77.6 StartY=13.48 StartZ=0 EndX=77.6 EndY=16.32 EndZ=0
    g14: LineSegment StartX=77.6 StartY=16.32 StartZ=0 EndX=71.76 EndY=16.32 EndZ=0
    g15: LineSegment StartX=71.76 StartY=16.32 StartZ=0 EndX=71.76 EndY=13.48 EndZ=0
    g16: GeomPoint [constr] X=74.68 Y=14.9 Z=0
    g17: LineSegment StartX=71.76 StartY=26.32 StartZ=0 EndX=71.76 EndY=23.48 EndZ=0
    g18: LineSegment StartX=71.76 StartY=23.48 StartZ=0 EndX=77.6 EndY=23.48 EndZ=0
    g19: LineSegment StartX=77.6 StartY=23.48 StartZ=0 EndX=77.6 EndY=26.32 EndZ=0
    g20: LineSegment StartX=77.6 StartY=26.32 StartZ=0 EndX=71.76 EndY=26.32 EndZ=0
    g21: GeomPoint [constr] X=74.68 Y=24.9 Z=0
  constraints (61):
    c: Distance(g0) = 6.16
    c: Vertical(g0)
    c: Coincident(g1,g0)
    c: Coincident(g2,g1)
    c: Vertical(g2)
    c: Coincident(g3,g2)
    c: Horizontal(g3)
    c: Distance(g4) = 38.16
    c: Coincident(g4,g3)
    c: Vertical(g4)
    c: Coincident(g5,g4)
    c: Horizontal(g5)
    c: Distance(g6) = 3.16
    c: Coincident(g6,g5)
    c: Vertical(g6)
    c: Coincident(g7,g6)
    c: Horizontal(g7)
    c: Coincident(g8,g7)
    c: Vertical(g8)
    c: Vertical(g9)
    c: Coincident(g10,g0)
    c: Horizontal(g10)
    c: Equal(g0,g2)
    c: DistanceX(g10,g10) = 3.16
    c: Equal(g3,g10)
    c: DistanceX(g1,g1) = 6.16
    c: Equal(g9,g4)
    c: Coincident(g11,g9)
    c: Coincident(g11,g8)
    c: Horizontal(g11)
    c: Equal(g10,g11)
    c: Equal(g11,g5)
    c: Coincident(g12,g13)
    c: Coincident(g13,g14)
    c: Coincident(g14,g15)
    c: Coincident(g15,g12)
    c: Horizontal(g12)
    c: Horizontal(g14)
    c: Vertical(g13)
    c: Vertical(g15)
    c: Symmetric(g14,g12,g16)
    c: Distance(g13,g15) = 5.84
    c: Distance(g12,g14) = 2.84
    c: Vertical(g0,g12)
    c: Distance(g16,g1) = 14.9
    c: Coincident(g17,g18)
    c: Coincident(g18,g19)
    c: Coincident(g19,g20)
    c: Coincident(g20,g17)
    c: Vertical(g17)
    c: Vertical(g19)
    c: Horizontal(g18)
    c: Horizontal(g20)
    c: Symmetric(g19,g17,g21)
    c: Equal(g15,g17)
    c: Equal(g14,g18)
    c: Vertical(g17,g12)
    c: DistanceY(g16,g21) = 10
    c: Coincident(g9,g10)
    c: Horizontal(g1)
    c: Coincident(g-9,g1)
FEATURE [Sketcher::SketchObject] Sketch078  label="v8-motor-mount"
  ArcFitTolerance = 1e-06
  AttachmentSupport = -> [XY_Plane005]
  ExternalGeometry = -> [Sketch063]
  FullyConstrained = true
  MakeInternals = false
  MapMode = 5
  expr: Constraints[10] = <<v8-Dimensions>>.tabHeight + <<v8-Dimensions>>.kerf
  expr: Constraints[16] = <<v8-Dimensions>>.aMotorWidthDiameter
  expr: Constraints[1] = <<v8-Dimensions>>.tabWidth + <<v8-Dimensions>>.kerf * 2
  expr: Constraints[23] = <<v8-Dimensions>>.aMotorHeight / 2
  expr: Constraints[24] = <<v8-Dimensions>>.aMotorHeight / 2
  expr: Constraints[25] = <<v8-Dimensions>>.kerf * 2 + 2.5
  expr: Constraints[26] = 5 + 4 + <<v8-Dimensions>>.kerf
  expr: Constraints[4] = <<v8-Dimensions>>.tabHeight + <<v8-Dimensions>>.kerf
  sketch-geometry (12):
    g0: LineSegment StartX=-3.08 StartY=78.16 StartZ=0 EndX=3.08 EndY=78.16 EndZ=0
    g1: LineSegment StartX=-3.08 StartY=78.16 StartZ=0 EndX=-3.08 EndY=75.08 EndZ=0
    g2: LineSegment StartX=3.08 StartY=78.16 StartZ=0 EndX=3.08 EndY=75.08 EndZ=0
    g3: LineSegment StartX=-3.08 StartY=75.08 StartZ=0 EndX=-6.16 EndY=75.08 EndZ=0
    g4: LineSegment StartX=3.08 StartY=75.08 StartZ=0 EndX=6.16 EndY=75.08 EndZ=0
    g5: LineSegment StartX=-3.31662 StartY=71 StartZ=0 EndX=3.31662 EndY=71 EndZ=0
    g6: ArcOfCircle CenterX=0 CenterY=66 CenterZ=0 NormalX=0 NormalY=0 NormalZ=1 AngleXU=0 Radius=6 StartAngle=2.15648 EndAngle=4.1267
    g7: ArcOfCircle CenterX=0 CenterY=66 CenterZ=0 NormalX=0 NormalY=0 NormalZ=1 AngleXU=0 Radius=6 StartAngle=5.29807 EndAngle=7.2683
    g8: LineSegment StartX=-3.31662 StartY=61 StartZ=0 EndX=3.31662 EndY=61 EndZ=0
    g9: LineSegment StartX=-3.27804 StartY=58.34 StartZ=0 EndX=3.27804 EndY=58.34 EndZ=0
    g10: ArcOfCircle CenterX=0 CenterY=67.5224 CenterZ=0 NormalX=0 NormalY=0 NormalZ=1 AngleXU=0 Radius=9.75 StartAngle=2.25466 EndAngle=4.3695
    g11: ArcOfCircle CenterX=0 CenterY=67.5224 CenterZ=0 NormalX=0 NormalY=0 NormalZ=1 AngleXU=0 Radius=9.75 StartAngle=5.05528 EndAngle=7.17012
  constraints (35):
    c: Symmetric(g0,g0,g-2)
    c: DistanceX(g0,g0) = 6.16
    c: Coincident(g1,g0)
    c: Vertical(g1)
    c: DistanceY(g1,g1) = 3.08
    c: Coincident(g2,g0)
    c: Vertical(g2)
    c: Equal(g1,g2)
    c: Coincident(g3,g1)
    c: Horizontal(g3)
    c: DistanceX(g3,g3) = 3.08
    c: Coincident(g4,g2)
    c: Horizontal(g4)
    c: Equal(g3,g4)
    c: Symmetric(g5,g5,g-2)
    c: Coincident(g6,g5)
    c: Diameter(g6) = 12
    c: Coincident(g6,g-3)
    c: Coincident(g7,g6)
    c: Coincident(g7,g5)
    c: Coincident(g8,g6)
    c: Coincident(g8,g7)
    c: Horizontal(g8)
    c: DistanceY(g6,g5) = 5
    c: DistanceY(g6,g6) = 5
    c: DistanceY(g9,g6) = 2.66
    c: DistanceY(g6,g1) = 9.08
    c: Coincident(g10,g3)
    c: Coincident(g10,g9)
    c: PointOnObject(g10,g-2)
    c: Diameter(g10) = 19.5
    c: Coincident(g11,g4)
    c: Coincident(g11,g10)
    c: Coincident(g11,g9)
    c: Horizontal(g9)
FEATURE [Sketcher::SketchObject] Sketch079  label="v8-solar-brace"
  ArcFitTolerance = 1e-06
  AttachmentSupport = -> [YZ_Plane005]
  ExternalGeometry = -> [Sketch063]
  FullyConstrained = true
  MakeInternals = false
  MapMode = 5
  Placement = pos=(0,0,0) rot=(0.57735,0.57735,0.57735;2.0944rad)
  expr: Constraints[14] = 6 + <<v8-Dimensions>>.kerf * 2
  expr: Constraints[20] = <<v8-Dimensions>>.solarPanelDepth + <<v8-Dimensions>>.kerf * 2
  expr: Constraints[21] = <<v8-Dimensions>>.kerf * 2 + 4
  expr: Constraints[2] = <<v8-Dimensions>>.tabWidth + <<v8-Dimensions>>.kerf * 2
  expr: Constraints[5] = <<v8-Dimensions>>.tabHeight + <<v8-Dimensions>>.kerf * 2
  sketch-geometry (14):
    g0: LineSegment StartX=71.92 StartY=0 StartZ=0 EndX=78.08 EndY=0 EndZ=0
    g1: LineSegment StartX=71.92 StartY=0 StartZ=0 EndX=71.92 EndY=3.16 EndZ=0
    g2: LineSegment StartX=78.08 StartY=0 StartZ=0 EndX=78.08 EndY=3.16 EndZ=0
    g3: LineSegment StartX=78.08 StartY=3.16 StartZ=0 EndX=82.16 EndY=3.16 EndZ=0
    g4: LineSegment StartX=71.92 StartY=3.16 StartZ=0 EndX=65.76 EndY=3.16 EndZ=0
    g5: LineSegment StartX=82.16 StartY=3.16 StartZ=0 EndX=82.16 EndY=23.16 EndZ=0
    g6: LineSegment StartX=82.16 StartY=23.16 StartZ=0 EndX=84.82 EndY=23.16 EndZ=0
    g7: LineSegment StartX=84.82 StartY=23.16 StartZ=0 EndX=84.82 EndY=27.32 EndZ=0
    g8: Circle [constr] CenterX=84.82 CenterY=27.32 CenterZ=0 NormalX=0 NormalY=0 NormalZ=1 AngleXU=0 Radius=1
    g9: Circle [constr] CenterX=65.76 CenterY=27.32 CenterZ=0 NormalX=0 NormalY=0 NormalZ=1 AngleXU=0 Radius=1
    g10: Circle [constr] CenterX=65.76 CenterY=3.16 CenterZ=0 NormalX=0 NormalY=0 NormalZ=1 AngleXU=0 Radius=1
    g11: BSplineCurve PolesCount=3 KnotsCount=2 Degree=2 IsPeriodic=0
    g12: GeomPoint [constr] X=84.82 Y=27.32 Z=0
    g13: GeomPoint [constr] X=65.76 Y=3.16 Z=0
  constraints (36):
    c: Horizontal(g0)
    c: Symmetric(g0,g0,g-3)
    c: Distance(g0,g0) = 6.16
    c: Coincident(g1,g0)
    c: Vertical(g1)
    c: DistanceY(g1,g1) = 3.16
    c: Coincident(g2,g0)
    c: Vertical(g2)
    c: Equal(g1,g2)
    c: Coincident(g3,g2)
    c: Horizontal(g3)
    c: Vertical(g3,g-4)
    c: Coincident(g4,g1)
    c: Horizontal(g4)
    c: DistanceX(g4,g4) = 6.16
    c: Distance(g5) = 20
    c: Coincident(g5,g3)
    c: Vertical(g5)
    c: Coincident(g6,g5)
    c: Horizontal(g6)
    c: DistanceX(g6,g6) = 2.66
    c: Distance(g7) = 4.16
    c: Coincident(g7,g6)
    c: Vertical(g7)
    c: Weight(g8) = 1
    c: Equal(g8,g9)
    c: Equal(g8,g10)
    c: InternalAlignment(g8,g11)
    c: InternalAlignment(g9,g11)
    c: InternalAlignment(g10,g11)
    c: InternalAlignment(g12,g11)
    c: InternalAlignment(g13,g11)
    c: Coincident(g8,g7)
    c: Coincident(g10,g4)
    c: Horizontal(g9,g11)
    c: Vertical(g9,g11)
FEATURE [Sketcher::SketchObject] Sketch080  label="v8-large-gear-hub"
  ArcFitTolerance = 1e-06
  AttachmentSupport = -> [XY_Plane005]
  FullyConstrained = false
  MakeInternals = false
  MapMode = 5
  expr: Constraints[14] = <<v8-Dimensions>>.largeGearSpokeHub
  expr: Constraints[1] = <<v8-Dimensions>>.largeGearHubDiameter - <<v8-Dimensions>>.kerf * 2
  expr: Constraints[23] = <<v8-Dimensions>>.largeGearInnerDiameter
  expr: Constraints[25] = <<v8-Dimensions>>.largeGearOuterDiameter
  expr: Constraints[75] = <<v8-Dimensions>>.largeGearInnerDiameter
  sketch-geometry (184):
    g0: Circle CenterX=0 CenterY=0 CenterZ=0 NormalX=0 NormalY=0 NormalZ=1 AngleXU=0 Radius=2.92
    g1: Circle CenterX=0 CenterY=0 CenterZ=0 NormalX=0 NormalY=0 NormalZ=1 AngleXU=0 Radius=56.677
    g2: LineSegment [constr] StartX=0 StartY=0 StartZ=0 EndX=12.8789 EndY=39.6372 EndZ=0
    g3: LineSegment [constr] StartX=0 StartY=0 StartZ=0 EndX=-33.7174 EndY=24.4971 EndZ=0
    g4: LineSegment [constr] StartX=0 StartY=0 StartZ=0 EndX=-33.7174 EndY=-24.4971 EndZ=0
    g5: LineSegment [constr] StartX=0 StartY=0 StartZ=0 EndX=12.8789 EndY=-39.6372 EndZ=0
    g6: LineSegment [constr] StartX=0 StartY=0 StartZ=0 EndX=41.677 EndY=0 EndZ=0
    g7: Circle [constr] CenterX=0 CenterY=0 CenterZ=0 NormalX=0 NormalY=0 NormalZ=1 AngleXU=0 Radius=41.677
    g8: Circle [constr] CenterX=0 CenterY=0 CenterZ=0 NormalX=0 NormalY=0 NormalZ=1 AngleXU=0 Radius=7.5
    g9: LineSegment [constr] StartX=0 StartY=0 StartZ=0 EndX=45.8527 EndY=33.3139 EndZ=0
    g10: LineSegment [constr] StartX=0 StartY=0 StartZ=0 EndX=-17.5142 EndY=53.903 EndZ=0
    g11: LineSegment [constr] StartX=0 StartY=0 StartZ=0 EndX=-56.677 EndY=0 EndZ=0
    g12: LineSegment [constr] StartX=0 StartY=0 StartZ=0 EndX=-17.5141 EndY=-53.903 EndZ=0
    g13: LineSegment [constr] StartX=0 StartY=0 StartZ=0 EndX=45.8527 EndY=-33.3139 EndZ=0
    g14: LineSegment StartX=12.9076 StartY=28.3994 StartZ=0 EndX=8.27239 EndY=14.1336 EndZ=0
    g15: LineSegment StartX=15.9981 StartY=3.5 StartZ=0 EndX=30.9981 EndY=3.5 EndZ=0
    g16: LineSegment StartX=9.41431 StartY=7.45793 StartZ=0 EndX=10.0021 EndY=6.64891 EndZ=0
    g17: GeomPoint X=9.7082 Y=7.05342 Z=0
    g18: LineSegment [constr] StartX=8.27239 StartY=14.1336 StartZ=0 EndX=15.9981 EndY=3.5 EndZ=0
    g19: ArcOfCircle CenterX=0 CenterY=0 CenterZ=0 NormalX=0 NormalY=0 NormalZ=1 AngleXU=0 Radius=41.677 StartAngle=0.249319 EndAngle=1.00732
    g20: Circle [constr] CenterX=12.9076 CenterY=28.3994 CenterZ=0 NormalX=0 NormalY=0 NormalZ=1 AngleXU=0 Radius=1
    g21: Circle [constr] CenterX=16.3431 CenterY=38.9727 CenterZ=0 NormalX=0 NormalY=0 NormalZ=1 AngleXU=0 Radius=1
    g22: Circle [constr] CenterX=22.2609 CenterY=35.2338 CenterZ=0 NormalX=0 NormalY=0 NormalZ=1 AngleXU=0 Radius=1
    g23: BSplineCurve PolesCount=3 KnotsCount=2 Degree=2 IsPeriodic=0
    g24: GeomPoint [constr] X=12.9076 Y=28.3994 Z=0
    g25: GeomPoint [constr] X=22.2609 Y=35.2338 Z=0
    g26: Circle [constr] CenterX=30.9981 CenterY=3.5 CenterZ=0 NormalX=0 NormalY=0 NormalZ=1 AngleXU=0 Radius=1
    g27: Circle [constr] CenterX=42.1156 CenterY=3.5 CenterZ=0 NormalX=0 NormalY=0 NormalZ=1 AngleXU=0 Radius=1
    g28: Circle [constr] CenterX=40.3884 CenterY=10.2836 CenterZ=0 NormalX=0 NormalY=0 NormalZ=1 AngleXU=0 Radius=1
    g29: BSplineCurve PolesCount=3 KnotsCount=2 Degree=2 IsPeriodic=0
    g30: GeomPoint [constr] X=30.9981 Y=3.5 Z=0
    g31: GeomPoint [constr] X=40.3884 Y=10.2836 Z=0
    g32: Circle [constr] CenterX=8.27239 CenterY=14.1336 CenterZ=0 NormalX=0 NormalY=0 NormalZ=1 AngleXU=0 Radius=1
    g33: Circle [constr] CenterX=7.12649 CenterY=10.6068 CenterZ=0 NormalX=0 NormalY=0 NormalZ=1 AngleXU=0 Radius=1
    g34: Circle [constr] CenterX=9.41431 CenterY=7.45793 CenterZ=0 NormalX=0 NormalY=0 NormalZ=1 AngleXU=0 Radius=1
    g35: BSplineCurve PolesCount=3 KnotsCount=2 Degree=2 IsPeriodic=0
    g36: GeomPoint [constr] X=8.27239 Y=14.1336 Z=0
    g37: GeomPoint [constr] X=9.41431 Y=7.45793 Z=0
    g38: Circle [constr] CenterX=15.9981 CenterY=3.5 CenterZ=0 NormalX=0 NormalY=0 NormalZ=1 AngleXU=0 Radius=1
    g39: Circle [constr] CenterX=12.2899 CenterY=3.5 CenterZ=0 NormalX=0 NormalY=0 NormalZ=1 AngleXU=0 Radius=1
    g40: Circle [constr] CenterX=10.0021 CenterY=6.64891 CenterZ=0 NormalX=0 NormalY=0 NormalZ=1 AngleXU=0 Radius=1
    g41: BSplineCurve PolesCount=3 KnotsCount=2 Degree=2 IsPeriodic=0
    g42: GeomPoint [constr] X=15.9981 Y=3.5 Z=0
    g43: GeomPoint [constr] X=10.0021 Y=6.64891 Z=0
    g44: Circle CenterX=0 CenterY=0 CenterZ=0 NormalX=0 NormalY=0 NormalZ=1 AngleXU=0 Radius=2.92
    g45: Circle CenterX=0 CenterY=0 CenterZ=0 NormalX=0 NormalY=0 NormalZ=1 AngleXU=0 Radius=56.677
    g46: LineSegment [constr] StartX=0 StartY=0 StartZ=0 EndX=-33.7174 EndY=24.4971 EndZ=0
    g47: LineSegment [constr] StartX=0 StartY=0 StartZ=0 EndX=12.8789 EndY=39.6372 EndZ=0
    g48: LineSegment [constr] StartX=0 StartY=0 StartZ=0 EndX=-17.5142 EndY=53.903 EndZ=0
    g49: LineSegment StartX=-23.0208 StartY=21.0518 StartZ=0 EndX=-10.8855 EndY=12.235 EndZ=0
    g50: LineSegment StartX=1.615 StartY=16.2967 StartZ=0 EndX=6.25024 EndY=30.5625 EndZ=0
    g51: LineSegment StartX=-4.18374 StartY=11.2582 StartZ=0 EndX=-3.23268 EndY=11.5672 EndZ=0
    g52: GeomPoint X=-3.70821 Y=11.4127 Z=0
    g53: LineSegment [constr] StartX=-10.8855 StartY=12.235 StartZ=0 EndX=1.615 EndY=16.2967 EndZ=0
    g54: ArcOfCircle CenterX=0 CenterY=0 CenterZ=0 NormalX=0 NormalY=0 NormalZ=1 AngleXU=0 Radius=41.677 StartAngle=1.50596 EndAngle=2.26396
    g55: Circle [constr] CenterX=-23.0208 CenterY=21.0518 CenterZ=0 NormalX=0 NormalY=0 NormalZ=1 AngleXU=0 Radius=1
    g56: Circle [constr] CenterX=-32.015 CenterY=27.5864 CenterZ=0 NormalX=0 NormalY=0 NormalZ=1 AngleXU=0 Radius=1
    g57: Circle [constr] CenterX=-26.6304 CenterY=32.0592 CenterZ=0 NormalX=0 NormalY=0 NormalZ=1 AngleXU=0 Radius=1
    g58: BSplineCurve PolesCount=3 KnotsCount=2 Degree=2 IsPeriodic=0
    g59: GeomPoint [constr] X=-23.0208 Y=21.0518 Z=0
    g60: GeomPoint [constr] X=-26.6304 Y=32.0592 Z=0
    g61: Circle [constr] CenterX=6.25024 CenterY=30.5625 CenterZ=0 NormalX=0 NormalY=0 NormalZ=1 AngleXU=0 Radius=1
    g62: Circle [constr] CenterX=9.68574 CenterY=41.1359 CenterZ=0 NormalX=0 NormalY=0 NormalZ=1 AngleXU=0 Radius=1
    g63: Circle [constr] CenterX=2.70045 CenterY=41.5894 CenterZ=0 NormalX=0 NormalY=0 NormalZ=1 AngleXU=0 Radius=1
    g64: BSplineCurve PolesCount=3 KnotsCount=2 Degree=2 IsPeriodic=0
    g65: GeomPoint [constr] X=6.25024 Y=30.5625 Z=0
    g66: GeomPoint [constr] X=2.70045 Y=41.5894 Z=0
    g67: Circle [constr] CenterX=-10.8855 CenterY=12.235 CenterZ=0 NormalX=0 NormalY=0 NormalZ=1 AngleXU=0 Radius=1
    g68: Circle [constr] CenterX=-7.88551 CenterY=10.0554 CenterZ=0 NormalX=0 NormalY=0 NormalZ=1 AngleXU=0 Radius=1
    g69: Circle [constr] CenterX=-4.18374 CenterY=11.2582 CenterZ=0 NormalX=0 NormalY=0 NormalZ=1 AngleXU=0 Radius=1
    g70: BSplineCurve PolesCount=3 KnotsCount=2 Degree=2 IsPeriodic=0
    g71: GeomPoint [constr] X=-10.8855 Y=12.235 Z=0
    g72: GeomPoint [constr] X=-4.18374 Y=11.2582 Z=0
    g73: Circle [constr] CenterX=1.615 CenterY=16.2967 CenterZ=0 NormalX=0 NormalY=0 NormalZ=1 AngleXU=0 Radius=1
    g74: Circle [constr] CenterX=0.469097 CenterY=12.77 CenterZ=0 NormalX=0 NormalY=0 NormalZ=1 AngleXU=0 Radius=1
    g75: Circle [constr] CenterX=-3.23268 CenterY=11.5672 CenterZ=0 NormalX=0 NormalY=0 NormalZ=1 AngleXU=0 Radius=1
    g76: BSplineCurve PolesCount=3 KnotsCount=2 Degree=2 IsPeriodic=0
    g77: GeomPoint [constr] X=1.615 Y=16.2967 Z=0
    g78: GeomPoint [constr] X=-3.23268 Y=11.5672 Z=0
    g79: Circle CenterX=0 CenterY=0 CenterZ=0 NormalX=0 NormalY=0 NormalZ=1 AngleXU=0 Radius=2.92
    g80: Circle CenterX=0 CenterY=0 CenterZ=0 NormalX=0 NormalY=0 NormalZ=1 AngleXU=0 Radius=56.677
    g81: LineSegment [constr] StartX=0 StartY=0 StartZ=0 EndX=-33.7174 EndY=-24.4972 EndZ=0
    g82: LineSegment [constr] StartX=0 StartY=0 StartZ=0 EndX=-33.7174 EndY=24.4971 EndZ=0
    g83: LineSegment [constr] StartX=0 StartY=0 StartZ=0 EndX=-56.677 EndY=-7.63105e-05 EndZ=0
    g84: LineSegment StartX=-27.1352 StartY=-15.3887 StartZ=0 EndX=-15 EndY=-6.57193 EndZ=0
    g85: LineSegment StartX=-15 StartY=6.57189 StartZ=0 EndX=-27.1353 EndY=15.3887 EndZ=0
    g86: LineSegment StartX=-12 StartY=-0.500016 StartZ=0 EndX=-12 EndY=0.499984 EndZ=0
    g87: GeomPoint X=-12 Y=-1.61569e-05 Z=0
    g88: LineSegment [constr] StartX=-15 StartY=-6.57193 StartZ=0 EndX=-15 EndY=6.57189 EndZ=0
    g89: ArcOfCircle CenterX=0 CenterY=0 CenterZ=0 NormalX=0 NormalY=0 NormalZ=1 AngleXU=0 Radius=41.677 StartAngle=2.76259 EndAngle=3.52059
    g90: Circle [constr] CenterX=-27.1352 CenterY=-15.3887 CenterZ=0 NormalX=0 NormalY=0 NormalZ=1 AngleXU=0 Radius=1
    g91: Circle [constr] CenterX=-36.1294 CenterY=-21.9234 CenterZ=0 NormalX=0 NormalY=0 NormalZ=1 AngleXU=0 Radius=1
    g92: Circle [constr] CenterX=-38.7194 CenterY=-15.4202 CenterZ=0 NormalX=0 NormalY=0 NormalZ=1 AngleXU=0 Radius=1
    g93: BSplineCurve PolesCount=3 KnotsCount=2 Degree=2 IsPeriodic=0
    g94: GeomPoint [constr] X=-27.1352 Y=-15.3887 Z=0
    g95: GeomPoint [constr] X=-38.7194 Y=-15.4202 Z=0
    g96: Circle [constr] CenterX=-27.1353 CenterY=15.3887 CenterZ=0 NormalX=0 NormalY=0 NormalZ=1 AngleXU=0 Radius=1
    g97: Circle [constr] CenterX=-36.1295 CenterY=21.9233 CenterZ=0 NormalX=0 NormalY=0 NormalZ=1 AngleXU=0 Radius=1
    g98: Circle [constr] CenterX=-38.7194 CenterY=15.4201 CenterZ=0 NormalX=0 NormalY=0 NormalZ=1 AngleXU=0 Radius=1
    g99: BSplineCurve PolesCount=3 KnotsCount=2 Degree=2 IsPeriodic=0
    g100: GeomPoint [constr] X=-27.1353 Y=15.3887 Z=0
    g101: GeomPoint [constr] X=-38.7194 Y=15.4201 Z=0
    g102: Circle [constr] CenterX=-15 CenterY=-6.57193 CenterZ=0 NormalX=0 NormalY=0 NormalZ=1 AngleXU=0 Radius=1
    g103: Circle [constr] CenterX=-12 CenterY=-4.3923 CenterZ=0 NormalX=0 NormalY=0 NormalZ=1 AngleXU=0 Radius=1
    g104: Circle [constr] CenterX=-12 CenterY=-0.500016 CenterZ=0 NormalX=0 NormalY=0 NormalZ=1 AngleXU=0 Radius=1
    g105: BSplineCurve PolesCount=3 KnotsCount=2 Degree=2 IsPeriodic=0
    g106: GeomPoint [constr] X=-15 Y=-6.57193 Z=0
    g107: GeomPoint [constr] X=-12 Y=-0.500016 Z=0
    g108: Circle [constr] CenterX=-15 CenterY=6.57189 CenterZ=0 NormalX=0 NormalY=0 NormalZ=1 AngleXU=0 Radius=1
    g109: Circle [constr] CenterX=-12 CenterY=4.39226 CenterZ=0 NormalX=0 NormalY=0 NormalZ=1 AngleXU=0 Radius=1
    g110: Circle [constr] CenterX=-12 CenterY=0.499984 CenterZ=0 NormalX=0 NormalY=0 NormalZ=1 AngleXU=0 Radius=1
    g111: BSplineCurve PolesCount=3 KnotsCount=2 Degree=2 IsPeriodic=0
    g112: GeomPoint [constr] X=-15 Y=6.57189 Z=0
    g113: GeomPoint [constr] X=-12 Y=0.499984 Z=0
    g114: Circle CenterX=0 CenterY=0 CenterZ=0 NormalX=0 NormalY=0 NormalZ=1 AngleXU=0 Radius=2.92
    g115: Circle CenterX=0 CenterY=0 CenterZ=0 NormalX=0 NormalY=0 NormalZ=1 AngleXU=0 Radius=56.677
    g116: LineSegment [constr] StartX=0 StartY=0 StartZ=0 EndX=12.8787 EndY=-39.6372 EndZ=0
    g117: LineSegment [constr] StartX=0 StartY=0 StartZ=0 EndX=-33.7174 EndY=-24.4971 EndZ=0
    g118: LineSegment [constr] StartX=0 StartY=0 StartZ=0 EndX=-17.5141 EndY=-53.903 EndZ=0
    g119: LineSegment StartX=6.25012 StartY=-30.5625 StartZ=0 EndX=1.61492 EndY=-16.2966 EndZ=0
    g120: LineSegment StartX=-10.8854 StartY=-12.2351 StartZ=0 EndX=-23.0207 EndY=-21.0518 EndZ=0
    g121: LineSegment StartX=-3.23267 StartY=-11.5672 StartZ=0 EndX=-4.18373 EndY=-11.2582 EndZ=0
    g122: GeomPoint X=-3.7082 Y=-11.4127 Z=0
    g123: LineSegment [constr] StartX=1.61492 StartY=-16.2966 StartZ=0 EndX=-10.8854 EndY=-12.2351 EndZ=0
    g124: ArcOfCircle CenterX=0 CenterY=0 CenterZ=0 NormalX=0 NormalY=0 NormalZ=1 AngleXU=0 Radius=41.677 StartAngle=4.01923 EndAngle=4.77723
    g125: Circle [constr] CenterX=6.25012 CenterY=-30.5625 CenterZ=0 NormalX=0 NormalY=0 NormalZ=1 AngleXU=0 Radius=1
    g126: Circle [constr] CenterX=9.68558 CenterY=-41.1359 CenterZ=0 NormalX=0 NormalY=0 NormalZ=1 AngleXU=0 Radius=1
    g127: Circle [constr] CenterX=2.70028 CenterY=-41.5894 CenterZ=0 NormalX=0 NormalY=0 NormalZ=1 AngleXU=0 Radius=1
    g128: BSplineCurve PolesCount=3 KnotsCount=2 Degree=2 IsPeriodic=0
    g129: GeomPoint [constr] X=6.25012 Y=-30.5625 Z=0
    g130: GeomPoint [constr] X=2.70028 Y=-41.5894 Z=0
    g131: Circle [constr] CenterX=-23.0207 CenterY=-21.0518 CenterZ=0 NormalX=0 NormalY=0 NormalZ=1 AngleXU=0 Radius=1
    g132: Circle [constr] CenterX=-32.0149 CenterY=-27.5865 CenterZ=0 NormalX=0 NormalY=0 NormalZ=1 AngleXU=0 Radius=1
    g133: Circle [constr] CenterX=-26.6303 CenterY=-32.0593 CenterZ=0 NormalX=0 NormalY=0 NormalZ=1 AngleXU=0 Radius=1
    g134: BSplineCurve PolesCount=3 KnotsCount=2 Degree=2 IsPeriodic=0
    g135: GeomPoint [constr] X=-23.0207 Y=-21.0518 Z=0
    g136: GeomPoint [constr] X=-26.6303 Y=-32.0593 Z=0
    g137: Circle [constr] CenterX=1.61492 CenterY=-16.2966 CenterZ=0 NormalX=0 NormalY=0 NormalZ=1 AngleXU=0 Radius=1
    g138: Circle [constr] CenterX=0.469039 CenterY=-12.7699 CenterZ=0 NormalX=0 NormalY=0 NormalZ=1 AngleXU=0 Radius=1
    g139: Circle [constr] CenterX=-3.23267 CenterY=-11.5672 CenterZ=0 NormalX=0 NormalY=0 NormalZ=1 AngleXU=0 Radius=1
    g140: BSplineCurve PolesCount=3 KnotsCount=2 Degree=2 IsPeriodic=0
    g141: GeomPoint [constr] X=1.61492 Y=-16.2966 Z=0
    g142: GeomPoint [constr] X=-3.23267 Y=-11.5672 Z=0
    g143: Circle [constr] CenterX=-10.8854 CenterY=-12.2351 CenterZ=0 NormalX=0 NormalY=0 NormalZ=1 AngleXU=0 Radius=1
    g144: Circle [constr] CenterX=-7.88542 CenterY=-10.0554 CenterZ=0 NormalX=0 NormalY=0 NormalZ=1 AngleXU=0 Radius=1
    g145: Circle [constr] CenterX=-4.18373 CenterY=-11.2582 CenterZ=0 NormalX=0 NormalY=0 NormalZ=1 AngleXU=0 Radius=1
    g146: BSplineCurve PolesCount=3 KnotsCount=2 Degree=2 IsPeriodic=0
    g147: GeomPoint [constr] X=-10.8854 Y=-12.2351 Z=0
    g148: GeomPoint [constr] X=-4.18373 Y=-11.2582 Z=0
    g149: Circle CenterX=0 CenterY=0 CenterZ=0 NormalX=0 NormalY=0 NormalZ=1 AngleXU=0 Radius=2.92
    g150: Circle CenterX=0 CenterY=0 CenterZ=0 NormalX=0 NormalY=0 NormalZ=1 AngleXU=0 Radius=56.677
    g151: LineSegment [constr] StartX=0 StartY=0 StartZ=0 EndX=41.677 EndY=9.72624e-07 EndZ=0
    g152: LineSegment [constr] StartX=0 StartY=0 StartZ=0 EndX=12.8788 EndY=-39.6372 EndZ=0
    g153: LineSegment [constr] StartX=0 StartY=0 StartZ=0 EndX=45.8526 EndY=-33.314 EndZ=0
    g154: LineSegment StartX=30.9981 StartY=-3.5 StartZ=0 EndX=15.9981 EndY=-3.5 EndZ=0
    g155: LineSegment StartX=8.27232 StartY=-14.1336 StartZ=0 EndX=12.9075 EndY=-28.3995 EndZ=0
    g156: LineSegment StartX=10.0021 StartY=-6.64894 StartZ=0 EndX=9.41429 EndY=-7.45796 EndZ=0
    g157: GeomPoint X=9.70819 Y=-7.05345 Z=0
    g158: LineSegment [constr] StartX=15.9981 StartY=-3.5 StartZ=0 EndX=8.27232 EndY=-14.1336 EndZ=0
    g159: ArcOfCircle CenterX=0 CenterY=0 CenterZ=0 NormalX=0 NormalY=0 NormalZ=1 AngleXU=0 Radius=41.677 StartAngle=5.27586 EndAngle=6.03387
    g160: Circle [constr] CenterX=30.9981 CenterY=-3.5 CenterZ=0 NormalX=0 NormalY=0 NormalZ=1 AngleXU=0 Radius=1
    g161: Circle [constr] CenterX=42.1156 CenterY=-3.5 CenterZ=0 NormalX=0 NormalY=0 NormalZ=1 AngleXU=0 Radius=1
    g162: Circle [constr] CenterX=40.3884 CenterY=-10.2836 CenterZ=0 NormalX=0 NormalY=0 NormalZ=1 AngleXU=0 Radius=1
    g163: BSplineCurve PolesCount=3 KnotsCount=2 Degree=2 IsPeriodic=0
    g164: GeomPoint [constr] X=30.9981 Y=-3.5 Z=0
    g165: GeomPoint [constr] X=40.3884 Y=-10.2836 Z=0
    g166: Circle [constr] CenterX=12.9075 CenterY=-28.3995 CenterZ=0 NormalX=0 NormalY=0 NormalZ=1 AngleXU=0 Radius=1
    g167: Circle [constr] CenterX=16.343 CenterY=-38.9728 CenterZ=0 NormalX=0 NormalY=0 NormalZ=1 AngleXU=0 Radius=1
    g168: Circle [constr] CenterX=22.2608 CenterY=-35.2339 CenterZ=0 NormalX=0 NormalY=0 NormalZ=1 AngleXU=0 Radius=1
    g169: BSplineCurve PolesCount=3 KnotsCount=2 Degree=2 IsPeriodic=0
    g170: GeomPoint [constr] X=12.9075 Y=-28.3995 Z=0
    g171: GeomPoint [constr] X=22.2608 Y=-35.2339 Z=0
    g172: Circle [constr] CenterX=15.9981 CenterY=-3.5 CenterZ=0 NormalX=0 NormalY=0 NormalZ=1 AngleXU=0 Radius=1
    g173: Circle [constr] CenterX=12.2899 CenterY=-3.5 CenterZ=0 NormalX=0 NormalY=0 NormalZ=1 AngleXU=0 Radius=1
    g174: Circle [constr] CenterX=10.0021 CenterY=-6.64894 CenterZ=0 NormalX=0 NormalY=0 NormalZ=1 AngleXU=0 Radius=1
    g175: BSplineCurve PolesCount=3 KnotsCount=2 Degree=2 IsPeriodic=0
    g176: GeomPoint [constr] X=15.9981 Y=-3.5 Z=0
    g177: GeomPoint [constr] X=10.0021 Y=-6.64894 Z=0
    g178: Circle [constr] CenterX=8.27232 CenterY=-14.1336 CenterZ=0 NormalX=0 NormalY=0 NormalZ=1 AngleXU=0 Radius=1
    g179: Circle [constr] CenterX=7.12643 CenterY=-10.6069 CenterZ=0 NormalX=0 NormalY=0 NormalZ=1 AngleXU=0 Radius=1
    g180: Circle [constr] CenterX=9.41429 CenterY=-7.45796 CenterZ=0 NormalX=0 NormalY=0 NormalZ=1 AngleXU=0 Radius=1
    g181: BSplineCurve PolesCount=3 KnotsCount=2 Degree=2 IsPeriodic=0
    g182: GeomPoint [constr] X=8.27232 Y=-14.1336 Z=0
    g183: GeomPoint [constr] X=9.41429 Y=-7.45796 Z=0
  constraints (398):
    c: Coincident(g0,g-1)
    c: Diameter(g0) = 5.84
    c: Coincident(g1,g0)
    c: Angle(g-1,g2) = 1.25664
    c: Coincident(g2,g0)
    c: Angle(g-1,g3) = 2.51327
    c: Coincident(g3,g0)
    c: Angle(g-1,g4) = 3.76991
    c: Coincident(g4,g0)
    c: Angle(g-1,g5) = 5.02655
    c: Coincident(g5,g0)
    c: Coincident(g6,g0)
    c: PointOnObject(g6,g-1)
    c: Coincident(g7,g0)
    c: Diameter(g8) = 15
    c: Coincident(g8,g0)
    c: PointOnObject(g2,g7)
    c: PointOnObject(g6,g7)
    c: PointOnObject(g3,g7)
    c: PointOnObject(g4,g7)
    c: PointOnObject(g5,g7)
    c: Angle(g6,g9) = 0.628319
    c: Coincident(g9,g0)
    c: Diameter(g7) = 83.354
    c: PointOnObject(g9,g1)
    c: Diameter(g1) = 113.354
    c: Angle(g-1,g10) = 1.88496
    c: Coincident(g10,g0)
    c: PointOnObject(g10,g1)
    c: Coincident(g11,g0)
    c: PointOnObject(g11,g1)
    c: Horizontal(g11)
    c: Angle(g-1,g12) = 4.39823
    c: Coincident(g12,g0)
    c: PointOnObject(g12,g1)
    c: Angle(g-1,g13) = 5.65487
    c: Coincident(g13,g0)
    c: PointOnObject(g13,g1)
    c: Parallel(g6,g15)
    c: Parallel(g14,g2)
    c: Symmetric(g16,g16,g9)
    c: PointOnObject(g17,g9)
    c: PointOnObject(g17,g16)
    c: Distance(g16,g16) = 1
    c: Distance(g0,g16) = 12
    c: Equal(g14,g15)
    c: Distance(g14) = 15
    c: Symmetric(g14,g15,g9)
    c: Distance(g14,g2) = 3.5
    c: Coincident(g18,g14)
    c: Coincident(g18,g15)
    c: Distance(g0,g18) = 15
    c: Coincident(g19,g0)
    c: Weight(g20) = 1
    c: Equal(g20,g21)
    c: Equal(g20,g22)
    c: InternalAlignment(g20,g23)
    c: InternalAlignment(g21,g23)
    c: InternalAlignment(g22,g23)
    c: InternalAlignment(g24,g23)
    c: InternalAlignment(g25,g23)
    c: Coincident(g20,g14)
    c: PointOnObject(g21,g14)
    c: Tangent(g23,g19) = 1.5708
    c: Weight(g26) = 1
    c: Equal(g26,g27)
    c: Equal(g26,g28)
    c: InternalAlignment(g26,g29)
    c: InternalAlignment(g27,g29)
    c: InternalAlignment(g28,g29)
    c: InternalAlignment(g30,g29)
    c: InternalAlignment(g31,g29)
    c: Coincident(g26,g15)
    c: Tangent(g29,g19) = -1.5708
    c: PointOnObject(g27,g15)
    c: Diameter(g19) = 83.354
    c: Distance(g19,g27) = 7
    c: Distance(g21,g19) = 7
    c: Weight(g32) = 1
    c: Equal(g32,g33)
    c: Equal(g32,g34)
    c: InternalAlignment(g32,g35)
    c: InternalAlignment(g33,g35)
    c: InternalAlignment(g34,g35)
    c: InternalAlignment(g36,g35)
    c: InternalAlignment(g37,g35)
    c: Coincident(g32,g14)
    c: Coincident(g34,g16)
    c: Weight(g38) = 1
    c: Equal(g38,g39)
    c: Equal(g38,g40)
    c: InternalAlignment(g38,g41)
    c: InternalAlignment(g39,g41)
    c: InternalAlignment(g40,g41)
    c: InternalAlignment(g42,g41)
    c: InternalAlignment(g43,g41)
    c: Coincident(g38,g15)
    c: Coincident(g40,g16)
    c: PointOnObject(g33,g14)
    c: PointOnObject(g39,g15)
    c: PointOnObject(g33,g16)
    c: PointOnObject(g39,g16)
    c: Diameter(g44) = 5.84
    c: Diameter(g79) = 5.84
    c: Diameter(g114) = 5.84
    c: Diameter(g149) = 5.84
    c: Coincident(g45,g44)
    c: Coincident(g80,g79)
    c: Coincident(g115,g114)
    c: Coincident(g150,g149)
    c: Coincident(g46,g44)
    c: Coincident(g81,g79)
    c: Coincident(g116,g114)
    c: Coincident(g151,g149)
    c: Coincident(g47,g44)
    c: Coincident(g82,g79)
    c: Coincident(g117,g114)
    c: Coincident(g152,g149)
    c: Angle(g47,g48) = 0.628319
    c: Angle(g82,g83) = 0.628319
    c: Angle(g117,g118) = 0.628319
    c: Angle(g152,g153) = 0.628319
    c: Coincident(g48,g44)
    c: Coincident(g83,g79)
    c: Coincident(g118,g114)
    c: Coincident(g153,g149)
    c: PointOnObject(g48,g45)
    c: PointOnObject(g83,g80)
    c: PointOnObject(g118,g115)
    c: PointOnObject(g153,g150)
    c: Diameter(g45) = 113.354
    c: Diameter(g80) = 113.354
    c: Diameter(g115) = 113.354
    c: Diameter(g150) = 113.354
    c: Parallel(g47,g50)
    c: Parallel(g82,g85)
    c: Parallel(g117,g120)
    c: Parallel(g152,g155)
    c: Parallel(g49,g46)
    c: Parallel(g84,g81)
    c: Parallel(g119,g116)
    c: Parallel(g154,g151)
    c: Symmetric(g51,g51,g48)
    c: Symmetric(g86,g86,g83)
    c: Symmetric(g121,g121,g118)
    c: Symmetric(g156,g156,g153)
    c: PointOnObject(g52,g48)
    c: PointOnObject(g87,g83)
    c: PointOnObject(g122,g118)
    c: PointOnObject(g157,g153)
    c: PointOnObject(g52,g51)
    c: PointOnObject(g87,g86)
    c: PointOnObject(g122,g121)
    c: PointOnObject(g157,g156)
    c: Distance(g51,g51) = 1
    c: Distance(g86,g86) = 1
    c: Distance(g121,g121) = 1
    c: Distance(g156,g156) = 1
    c: Distance(g44,g51) = 12
    c: Distance(g79,g86) = 12
    c: Distance(g114,g121) = 12
    c: Distance(g149,g156) = 12
    c: Equal(g49,g50)
    c: Equal(g84,g85)
    c: Equal(g119,g120)
    c: Equal(g154,g155)
    c: Symmetric(g49,g50,g48)
    c: Symmetric(g84,g85,g83)
    c: Symmetric(g119,g120,g118)
    c: Symmetric(g154,g155,g153)
    c: Distance(g49,g46) = 3.5
    c: Distance(g84,g81) = 3.5
    c: Distance(g119,g116) = 3.5
    c: Distance(g154,g151) = 3.5
    c: Coincident(g53,g49)
    c: Coincident(g88,g84)
    c: Coincident(g123,g119)
    c: Coincident(g158,g154)
    c: Coincident(g53,g50)
    c: Coincident(g88,g85)
    c: Coincident(g123,g120)
    c: Coincident(g158,g155)
    c: Distance(g44,g53) = 15
    c: Distance(g79,g88) = 15
    c: Distance(g114,g123) = 15
    c: Distance(g149,g158) = 15
    c: Coincident(g54,g44)
    c: Coincident(g89,g79)
    c: Coincident(g124,g114)
    c: Coincident(g159,g149)
    c: Weight(g55) = 1
    c: Weight(g90) = 1
    c: Weight(g125) = 1
    c: Weight(g160) = 1
    c: Equal(g55,g56)
    c: Equal(g90,g91)
    c: Equal(g125,g126)
    c: Equal(g160,g161)
    c: Equal(g55,g57)
    c: Equal(g90,g92)
    c: Equal(g125,g127)
    c: Equal(g160,g162)
    c: InternalAlignment(g55,g58)
    c: InternalAlignment(g90,g93)
    c: InternalAlignment(g125,g128)
    c: InternalAlignment(g160,g163)
    c: InternalAlignment(g56,g58)
    c: InternalAlignment(g91,g93)
    c: InternalAlignment(g126,g128)
    c: InternalAlignment(g161,g163)
    c: InternalAlignment(g57,g58)
    c: InternalAlignment(g92,g93)
    c: InternalAlignment(g127,g128)
    c: InternalAlignment(g162,g163)
    c: InternalAlignment(g59,g58)
    c: InternalAlignment(g94,g93)
    c: InternalAlignment(g129,g128)
    c: InternalAlignment(g164,g163)
    c: InternalAlignment(g60,g58)
    c: InternalAlignment(g95,g93)
    c: InternalAlignment(g130,g128)
    c: InternalAlignment(g165,g163)
    c: Coincident(g55,g49)
    c: Coincident(g90,g84)
    c: Coincident(g125,g119)
    c: Coincident(g160,g154)
    c: PointOnObject(g56,g49)
    c: PointOnObject(g91,g84)
    c: PointOnObject(g126,g119)
    c: PointOnObject(g161,g154)
    c: Tangent(g58,g54) = 1.5708
    c: Tangent(g93,g89) = 1.5708
    c: Tangent(g128,g124) = 1.5708
    c: Tangent(g163,g159) = 1.5708
    c: Weight(g61) = 1
    c: Weight(g96) = 1
    c: Weight(g131) = 1
    c: Weight(g166) = 1
    c: Equal(g61,g62)
    c: Equal(g96,g97)
    c: Equal(g131,g132)
    c: Equal(g166,g167)
    c: Equal(g61,g63)
    c: Equal(g96,g98)
    c: Equal(g131,g133)
    c: Equal(g166,g168)
    c: InternalAlignment(g61,g64)
    c: InternalAlignment(g96,g99)
    c: InternalAlignment(g131,g134)
    c: InternalAlignment(g166,g169)
    c: InternalAlignment(g62,g64)
    c: InternalAlignment(g97,g99)
    c: InternalAlignment(g132,g134)
    c: InternalAlignment(g167,g169)
    c: InternalAlignment(g63,g64)
    c: InternalAlignment(g98,g99)
    c: InternalAlignment(g133,g134)
    c: InternalAlignment(g168,g169)
    c: InternalAlignment(g65,g64)
    c: InternalAlignment(g100,g99)
    c: InternalAlignment(g135,g134)
    c: InternalAlignment(g170,g169)
    c: InternalAlignment(g66,g64)
    c: InternalAlignment(g101,g99)
    c: InternalAlignment(g136,g134)
    c: InternalAlignment(g171,g169)
    c: Coincident(g61,g50)
    c: Coincident(g96,g85)
    c: Coincident(g131,g120)
    c: Coincident(g166,g155)
    c: Tangent(g64,g54) = -1.5708
    c: Tangent(g99,g89) = -1.5708
    c: Tangent(g134,g124) = -1.5708
    c: Tangent(g169,g159) = -1.5708
    c: PointOnObject(g62,g50)
    c: PointOnObject(g97,g85)
    c: PointOnObject(g132,g120)
    c: PointOnObject(g167,g155)
    c: Diameter(g54) = 83.354
    c: Diameter(g89) = 83.354
    c: Diameter(g124) = 83.354
    c: Diameter(g159) = 83.354
    c: Distance(g54,g62) = 7
    c: Distance(g89,g97) = 7
    c: Distance(g124,g132) = 7
    c: Distance(g159,g167) = 7
    c: Distance(g56,g54) = 7
    c: Distance(g91,g89) = 7
    c: Distance(g126,g124) = 7
    c: Distance(g161,g159) = 7
    c: Weight(g67) = 1
    c: Weight(g102) = 1
    c: Weight(g137) = 1
    c: Weight(g172) = 1
    c: Equal(g67,g68)
    c: Equal(g102,g103)
    c: Equal(g137,g138)
    c: Equal(g172,g173)
    c: Equal(g67,g69)
    c: Equal(g102,g104)
    c: Equal(g137,g139)
    c: Equal(g172,g174)
    c: InternalAlignment(g67,g70)
    c: InternalAlignment(g102,g105)
    c: InternalAlignment(g137,g140)
    c: InternalAlignment(g172,g175)
    c: InternalAlignment(g68,g70)
    c: InternalAlignment(g103,g105)
    c: InternalAlignment(g138,g140)
    c: InternalAlignment(g173,g175)
    c: InternalAlignment(g69,g70)
    c: InternalAlignment(g104,g105)
    c: InternalAlignment(g139,g140)
    c: InternalAlignment(g174,g175)
    c: InternalAlignment(g71,g70)
    c: InternalAlignment(g106,g105)
    c: InternalAlignment(g141,g140)
    c: InternalAlignment(g176,g175)
    c: InternalAlignment(g72,g70)
    c: InternalAlignment(g107,g105)
    c: InternalAlignment(g142,g140)
    c: InternalAlignment(g177,g175)
    c: Coincident(g67,g49)
    c: Coincident(g102,g84)
    c: Coincident(g137,g119)
    c: Coincident(g172,g154)
    c: Coincident(g69,g51)
    c: Coincident(g104,g86)
    c: Coincident(g139,g121)
    c: Coincident(g174,g156)
    c: Weight(g73) = 1
    c: Weight(g108) = 1
    c: Weight(g143) = 1
    c: Weight(g178) = 1
    c: Equal(g73,g74)
    c: Equal(g108,g109)
    c: Equal(g143,g144)
    c: Equal(g178,g179)
    c: Equal(g73,g75)
    c: Equal(g108,g110)
    c: Equal(g143,g145)
    c: Equal(g178,g180)
    c: InternalAlignment(g73,g76)
    c: InternalAlignment(g108,g111)
    c: InternalAlignment(g143,g146)
    c: InternalAlignment(g178,g181)
    c: InternalAlignment(g74,g76)
    c: InternalAlignment(g109,g111)
    c: InternalAlignment(g144,g146)
    c: InternalAlignment(g179,g181)
    c: InternalAlignment(g75,g76)
    c: InternalAlignment(g110,g111)
    c: InternalAlignment(g145,g146)
    c: InternalAlignment(g180,g181)
    c: InternalAlignment(g77,g76)
    c: InternalAlignment(g112,g111)
    c: InternalAlignment(g147,g146)
    c: InternalAlignment(g182,g181)
    c: InternalAlignment(g78,g76)
    c: InternalAlignment(g113,g111)
    c: InternalAlignment(g148,g146)
    c: InternalAlignment(g183,g181)
    c: Coincident(g73,g50)
    c: Coincident(g108,g85)
    c: Coincident(g143,g120)
    c: Coincident(g178,g155)
    c: Coincident(g75,g51)
    c: Coincident(g110,g86)
    c: Coincident(g145,g121)
    c: Coincident(g180,g156)
    c: PointOnObject(g68,g49)
    c: PointOnObject(g103,g84)
    c: PointOnObject(g138,g119)
    c: PointOnObject(g173,g154)
    c: PointOnObject(g74,g50)
    c: PointOnObject(g109,g85)
    c: PointOnObject(g144,g120)
    c: PointOnObject(g179,g155)
    c: PointOnObject(g68,g51)
    c: PointOnObject(g103,g86)
    c: PointOnObject(g138,g121)
    c: PointOnObject(g173,g156)
    c: PointOnObject(g74,g51)
    c: PointOnObject(g109,g86)
    c: PointOnObject(g144,g121)
    c: PointOnObject(g179,g156)
    c: Coincident(g0,g44)
    c: Coincident(g0,g79)
    c: Coincident(g0,g114)
    c: Coincident(g0,g149)
    c: Distance(g56,g97) = 7
    c: Distance(g91,g132) = 7
    c: Distance(g126,g167) = 7
    c: Distance(g27,g161) = 7
    c: Distance(g62,g21) = 7
    c: Parallel(g14,g50)
    c: Parallel(g49,g85)
    c: Parallel(g4,g120)
FEATURE [Sketcher::SketchObject] Sketch081  label="v8-jig"
  ArcFitTolerance = 1e-06
  AttachmentSupport = -> [XY_Plane005]
  ExternalGeometry = -> [Sketch064]
  FullyConstrained = true
  MakeInternals = false
  MapMode = 5
  expr: Constraints[22] = <<v8-Dimensions>>.mDiameterEdge - <<v8-Dimensions>>.kerf * 3
  expr: Constraints[23] = <<v8-Dimensions>>.mDiameterEdge - <<v8-Dimensions>>.kerf * 3
  expr: Constraints[28] = <<v8-Dimensions>>.mDiameterCut
  expr: Constraints[30] = <<v8-Dimensions>>.mDiameterCut
  expr: Constraints[31] = <<v8-Dimensions>>.mDiameterCut
  expr: Constraints[41] = 6.16
  sketch-geometry (30):
    g0: LineSegment [constr] StartX=0 StartY=0 StartZ=0 EndX=-25.7172 EndY=15.4475 EndZ=0
    g1: ArcOfCircle CenterX=0 CenterY=0 CenterZ=0 NormalX=0 NormalY=0 NormalZ=1 AngleXU=0 Radius=7.46 StartAngle=4.17148 EndAngle=5.74228
    g2: ArcOfCircle CenterX=-25.7172 CenterY=15.4475 CenterZ=0 NormalX=0 NormalY=0 NormalZ=1 AngleXU=0 Radius=7.46 StartAngle=2.60068 EndAngle=4.17148
    g3: LineSegment StartX=-29.5585 StartY=9.05247 StartZ=0 EndX=-3.84128 EndY=-6.39501 EndZ=0
    g4: ArcOfCircle CenterX=0 CenterY=0 CenterZ=0 NormalX=0 NormalY=0 NormalZ=1 AngleXU=0 Radius=13.62 StartAngle=4.17148 EndAngle=5.74228
    g5: ArcOfCircle CenterX=-25.7172 CenterY=15.4475 CenterZ=0 NormalX=0 NormalY=0 NormalZ=1 AngleXU=0 Radius=13.62 StartAngle=2.60068 EndAngle=4.17148
    g6: LineSegment [constr] StartX=-32.7304 StartY=3.77187 StartZ=0 EndX=-7.01316 EndY=-11.6756 EndZ=0
    g7: LineSegment StartX=-31.3256 StartY=0.595028 StartZ=0 EndX=-70.4593 EndY=-64.5553 EndZ=0
    g8: LineSegment StartX=-69.7746 StartY=-67.2996 StartZ=0 EndX=-51.7726 EndY=-78.1128 EndZ=0
    g9: LineSegment StartX=-49.0283 StartY=-77.4282 StartZ=0 EndX=-9.89463 EndY=-12.2779 EndZ=0
    g10: LineSegment StartX=-32.7304 StartY=3.77187 StartZ=0 EndX=-32.0103 EndY=3.33934 EndZ=0
    g11: LineSegment StartX=-7.15032 StartY=-11.5932 StartZ=0 EndX=-7.01316 EndY=-11.6756 EndZ=0
    g12: LineSegment [constr] StartX=-19.8718 StartY=-3.95187 StartZ=0 EndX=-60.7736 EndY=-72.7062 EndZ=0
    g13: Circle CenterX=-40.3227 CenterY=-38.329 CenterZ=0 NormalX=0 NormalY=0 NormalZ=1 AngleXU=0 Radius=2.92
    g14: Circle CenterX=-24.9845 CenterY=-12.5462 CenterZ=0 NormalX=0 NormalY=0 NormalZ=1 AngleXU=0 Radius=2.92
    g15: Circle CenterX=-55.6609 CenterY=-64.1119 CenterZ=0 NormalX=0 NormalY=0 NormalZ=1 AngleXU=0 Radius=2.92
    g16: LineSegment StartX=6.39501 StartY=-3.84128 StartZ=0 EndX=9.5669 EndY=1.43933 EndZ=0
    g17: LineSegment StartX=11.6756 StartY=-7.01316 StartZ=0 EndX=14.8475 EndY=-1.73256 EndZ=0
    g18: LineSegment StartX=14.8475 StartY=-1.73256 StartZ=0 EndX=9.5669 EndY=1.43933 EndZ=0
    g19: LineSegment StartX=-37.3928 StartY=22.4606 StartZ=0 EndX=-34.2209 EndY=27.7412 EndZ=0
    g20: LineSegment StartX=-32.1122 StartY=19.2888 StartZ=0 EndX=-28.9403 EndY=24.5694 EndZ=0
    g21: LineSegment StartX=-28.9403 StartY=24.5694 StartZ=0 EndX=-34.2209 EndY=27.7412 EndZ=0
    g22: ArcOfCircle CenterX=-8.18015 CenterY=-13.3077 CenterZ=0 NormalX=0 NormalY=0 NormalZ=1 AngleXU=0 Radius=2 StartAngle=1.02989 EndAngle=2.60068
    g23: GeomPoint [constr] X=-8.8648 Y=-10.5634 Z=0
    g24: ArcOfCircle CenterX=-33.0401 CenterY=1.62486 CenterZ=0 NormalX=0 NormalY=0 NormalZ=1 AngleXU=0 Radius=2 StartAngle=5.74228 EndAngle=7.31307
    g25: GeomPoint [constr] X=-30.2958 Y=2.30951 Z=0
    g26: ArcOfCircle CenterX=-68.7448 CenterY=-65.5851 CenterZ=0 NormalX=0 NormalY=0 NormalZ=1 AngleXU=0 Radius=2 StartAngle=2.60068 EndAngle=4.17148
    g27: GeomPoint [constr] X=-71.4891 Y=-66.2697 Z=0
    g28: ArcOfCircle CenterX=-50.7427 CenterY=-76.3983 CenterZ=0 NormalX=0 NormalY=0 NormalZ=1 AngleXU=0 Radius=2 StartAngle=4.17148 EndAngle=5.74228
    g29: GeomPoint [constr] X=-50.0581 Y=-79.1426 Z=0
  constraints (70):
    c: Coincident(g0,g-1)
    c: Coincident(g0,g-8)
    c: Coincident(g2,g0)
    c: Tangent(g3,g2) = -1.5708
    c: Tangent(g1,g3) = -1.5708
    c: PointOnObject(g2,g0)
    c: PointOnObject(g1,g0)
    c: Coincident(g4,g1)
    c: Coincident(g5,g0)
    c: Tangent(g5,g6) = -1.5708
    c: Tangent(g4,g6) = -1.5708
    c: Distance(g27,g25) = 80
    c: PointOnObject(g25,g6)
    c: Distance(g29,g27) = 25
    c: PointOnObject(g23,g6)
    c: Coincident(g10,g5)
    c: Coincident(g11,g4)
    c: Coincident(g1,g0)
    c: PointOnObject(g4,g0)
    c: PointOnObject(g5,g0)
    c: Perpendicular(g10,g7)
    c: Perpendicular(g9,g11)
    c: Diameter(g1) = 14.92
    c: Diameter(g2) = 14.92
    c: Perpendicular(g7,g8)
    c: Symmetric(g6,g6,g12)
    c: Symmetric(g27,g29,g12)
    c: Symmetric(g12,g12,g13)
    c: Diameter(g14) = 5.84
    c: PointOnObject(g14,g12)
    c: Diameter(g13) = 5.84
    c: Diameter(g15) = 5.84
    c: PointOnObject(g15,g12)
    c: Distance(g15,g8) = 10
    c: Distance(g14,g6) = 10
    c: Coincident(g18,g17)
    c: Coincident(g18,g16)
    c: Tangent(g16,g1) = -1.5708
    c: Tangent(g17,g4) = -1.5708
    c: Distance(g18) = 6.16
    c: Parallel(g0,g18)
    c: Distance(g17) = 6.16
    c: Coincident(g21,g20)
    c: Coincident(g21,g19)
    c: Tangent(g19,g5) = 1.5708
    c: Tangent(g2,g20) = 1.5708
    c: Parallel(g21,g0)
    c: Distance(g21) = 6.16
    c: Distance(g19) = 6.16
    c: PointOnObject(g23,g11)
    c: PointOnObject(g23,g9)
    c: Tangent(g11,g22) = 1.5708
    c: Tangent(g9,g22) = 1.5708
    c: PointOnObject(g25,g10)
    c: PointOnObject(g25,g7)
    c: Tangent(g10,g24) = 1.5708
    c: Tangent(g7,g24) = 1.5708
    c: Distance(g24,g10) = 2
    c: Distance(g22,g11) = 2
    c: Distance(g11) = 0.16
    c: PointOnObject(g27,g7)
    c: PointOnObject(g27,g8)
    c: Tangent(g7,g26) = -1.5708
    c: Tangent(g8,g26) = -1.5708
    c: PointOnObject(g29,g9)
    c: PointOnObject(g29,g8)
    c: Tangent(g9,g28) = -1.5708
    c: Tangent(g8,g28) = -1.5708
    c: Distance(g7,g26) = 2
    c: Distance(g28,g9) = 2
FEATURE [Sketcher::SketchObject] Sketch082  label="v8-spokes"
  ArcFitTolerance = 1e-06
  AttachmentSupport = -> [XY_Plane005]
  FullyConstrained = true
  MakeInternals = false
  MapMode = 5
  sketch-geometry (36):
    g0: LineSegment [constr] StartX=0 StartY=0 StartZ=0 EndX=2.78115 EndY=8.55951 EndZ=0
    g1: LineSegment StartX=0.0647979 StartY=4.79464 StartZ=0 EndX=2.7658 EndY=3.91703 EndZ=0
    g2: LineSegment StartX=0.0647979 StartY=4.79464 StartZ=0 EndX=1.32559 EndY=8.67495 EndZ=0
    g3: LineSegment StartX=2.7658 StartY=3.91703 StartZ=0 EndX=4.02659 EndY=7.79735 EndZ=0
    g4: LineSegment [constr] StartX=0 StartY=0 StartZ=0 EndX=-7.28115 EndY=5.29007 EndZ=0
    g5: LineSegment StartX=-4.53995 StartY=1.54325 StartZ=0 EndX=-2.87064 EndY=3.84086 EndZ=0
    g6: LineSegment StartX=-4.53995 StartY=1.54325 StartZ=0 EndX=-7.84074 EndY=3.94142 EndZ=0
    g7: LineSegment StartX=-2.87064 StartY=3.84086 StartZ=0 EndX=-6.17143 EndY=6.23902 EndZ=0
    g8: LineSegment [constr] StartX=0 StartY=0 StartZ=0 EndX=-7.28115 EndY=-5.29007 EndZ=0
    g9: LineSegment StartX=-2.87064 StartY=-3.84086 StartZ=0 EndX=-4.53995 EndY=-1.54325 EndZ=0
    g10: LineSegment StartX=-2.87064 StartY=-3.84086 StartZ=0 EndX=-6.17143 EndY=-6.23902 EndZ=0
    g11: LineSegment StartX=-4.53995 StartY=-1.54325 StartZ=0 EndX=-7.84074 EndY=-3.94142 EndZ=0
    g12: LineSegment [constr] StartX=0 StartY=0 StartZ=0 EndX=2.78115 EndY=-8.55951 EndZ=0
    g13: LineSegment StartX=2.7658 StartY=-3.91703 StartZ=0 EndX=0.0647973 EndY=-4.79464 EndZ=0
    g14: LineSegment StartX=2.7658 StartY=-3.91703 StartZ=0 EndX=4.02659 EndY=-7.79735 EndZ=0
    g15: LineSegment StartX=0.0647973 StartY=-4.79464 StartZ=0 EndX=1.32559 EndY=-8.67495 EndZ=0
    g16: LineSegment [constr] StartX=0 StartY=0 StartZ=0 EndX=9 EndY=-5.52923e-07 EndZ=0
    g17: LineSegment StartX=4.58 StartY=1.42 StartZ=0 EndX=4.58 EndY=-1.42 EndZ=0
    g18: LineSegment StartX=4.58 StartY=1.42 StartZ=0 EndX=8.66 EndY=1.42 EndZ=0
    g19: LineSegment StartX=4.58 StartY=-1.42 StartZ=0 EndX=8.66 EndY=-1.42 EndZ=0
    g20: ArcOfCircle CenterX=0 CenterY=0 CenterZ=0 NormalX=0 NormalY=0 NormalZ=1 AngleXU=0 Radius=8.77565 StartAngle=1.41916 EndAngle=2.35075
    g21: ArcOfCircle CenterX=0 CenterY=0 CenterZ=0 NormalX=0 NormalY=0 NormalZ=1 AngleXU=0 Radius=8.77565 StartAngle=2.6758 EndAngle=3.60739
    g22: ArcOfCircle CenterX=2e-16 CenterY=-1e-15 CenterZ=0 NormalX=0 NormalY=0 NormalZ=1 AngleXU=0 Radius=8.77565 StartAngle=3.93244 EndAngle=4.86402
    g23: ArcOfCircle CenterX=2e-16 CenterY=-1e-15 CenterZ=0 NormalX=0 NormalY=0 NormalZ=1 AngleXU=0 Radius=8.77565 StartAngle=5.18907 EndAngle=6.12066
    g24: ArcOfCircle CenterX=0 CenterY=0 CenterZ=0 NormalX=0 NormalY=0 NormalZ=1 AngleXU=0 Radius=8.77565 StartAngle=0.162526 EndAngle=1.09411
    g25: LineSegment StartX=35 StartY=0 StartZ=0 EndX=35 EndY=3.16 EndZ=0
    g26: LineSegment StartX=35 StartY=3.16 StartZ=0 EndX=39.08 EndY=3.16 EndZ=0
    g27: Circle [constr] CenterX=39.08 CenterY=3.16 CenterZ=0 NormalX=0 NormalY=0 NormalZ=1 AngleXU=0 Radius=1
    g28: Circle [constr] CenterX=42.58 CenterY=1.16 CenterZ=0 NormalX=0 NormalY=0 NormalZ=1 AngleXU=0 Radius=1
    g29: Circle [constr] CenterX=80.16 CenterY=1.16 CenterZ=0 NormalX=0 NormalY=0 NormalZ=1 AngleXU=0 Radius=1
    g30: BSplineCurve PolesCount=3 KnotsCount=2 Degree=2 IsPeriodic=0
    g31: GeomPoint [constr] X=39.08 Y=3.16 Z=0
    g32: GeomPoint [constr] X=80.16 Y=1.16 Z=0
    g33: LineSegment StartX=80.16 StartY=1.16 StartZ=0 EndX=80.16 EndY=0 EndZ=0
    g34: LineSegment StartX=80.16 StartY=0 StartZ=0 EndX=35 EndY=0 EndZ=0
    g35: Circle CenterX=0 CenterY=0 CenterZ=0 NormalX=0 NormalY=0 NormalZ=1 AngleXU=0 Radius=2.92
  constraints (94):
    c: Distance(g0) = 9
    c: Angle(g-1,g0) = 1.25664
    c: Coincident(g0,g-1)
    c: Distance(g1) = 2.84
    c: Symmetric(g1,g1,g0)
    c: Distance(g2) = 4.08
    c: Coincident(g2,g1)
    c: Coincident(g3,g1)
    c: Symmetric(g2,g3,g0)
    c: Distance(g2,g3) = 2.84
    c: Distance(g0,g1) = 4.58
    c: Symmetric(g5,g5,g4)
    c: Symmetric(g9,g9,g8)
    c: Symmetric(g13,g13,g12)
    c: Symmetric(g17,g17,g16)
    c: Coincident(g6,g5)
    c: Coincident(g10,g9)
    c: Coincident(g14,g13)
    c: Coincident(g18,g17)
    c: Coincident(g7,g5)
    c: Coincident(g11,g9)
    c: Coincident(g15,g13)
    c: Coincident(g19,g17)
    c: Symmetric(g6,g7,g4)
    c: Symmetric(g10,g11,g8)
    c: Symmetric(g14,g15,g12)
    c: Symmetric(g18,g19,g16)
    c: Distance(g6,g7) = 2.84
    c: Distance(g10,g11) = 2.84
    c: Distance(g14,g15) = 2.84
    c: Distance(g18,g19) = 2.84
    c: Distance(g4,g5) = 4.58
    c: Distance(g8,g9) = 4.58
    c: Distance(g12,g13) = 4.58
    c: Distance(g16,g17) = 4.58
    c: Angle(g0,g4) = 1.25664
    c: Angle(g4,g8) = 1.25664
    c: Angle(g12,g16) = 1.25664
    c: Angle(g8,g12) = 1.25664
    c: Coincident(g4,g0)
    c: Coincident(g8,g0)
    c: Coincident(g16,g0)
    c: Coincident(g12,g0)
    c: Parallel(g7,g6)
    c: Parallel(g11,g10)
    c: Parallel(g15,g14)
    c: Parallel(g18,g19)
    c: Equal(g2,g7)
    c: Equal(g10,g15)
    c: Equal(g4,g8)
    c: Equal(g8,g12)
    c: Equal(g12,g16)
    c: Equal(g0,g4)
    c: Coincident(g20,g0)
    c: Coincident(g20,g7)
    c: Coincident(g21,g0)
    c: Coincident(g21,g6)
    c: Coincident(g21,g11)
    c: Coincident(g23,g22)
    c: Coincident(g23,g14)
    c: Coincident(g23,g19)
    c: PointOnObject(g20,g2)
    c: Coincident(g3,g24)
    c: Distance(g25) = 3.16
    c: PointOnObject(g25,g-1)
    c: Vertical(g25)
    c: Distance(g26) = 4.08
    c: Coincident(g26,g25)
    c: Horizontal(g26)
    c: Weight(g27) = 1
    c: Equal(g27,g28)
    c: Equal(g27,g29)
    c: InternalAlignment(g27,g30)
    c: InternalAlignment(g28,g30)
    c: InternalAlignment(g29,g30)
    c: InternalAlignment(g31,g30)
    c: InternalAlignment(g32,g30)
    c: Coincident(g27,g26)
    c: Distance(g33) = 1.16
    c: Coincident(g33,g30)
    c: Coincident(g34,g33)
    c: Perpendicular(g-1,g33)
    c: Horizontal(g34)
    c: Coincident(g34,g25)
    c: DistanceX(g34,g34) = 45.16
    c: Diameter(g35) = 5.84
    c: Coincident(g35,g24)
    c: Coincident(g24,g18)
    c: Coincident(g24,g0)
    c: Coincident(g22,g15)
    c: Coincident(g22,g10)
    c: DistanceX(g0,g25) = 35
    c: DistanceX(g30,g28) = 3.5
    c: DistanceY(g25,g28) = 1.16
FEATURE [Sketcher::SketchObject] Sketch083  label="V8-a-distance-guide"
  ArcFitTolerance = 1e-06
  AttachmentSupport = -> [XY_Plane005]
  FullyConstrained = true
  MakeInternals = false
  MapMode = 5
  expr: Constraints[14] = <<v8-Dimensions>>.solarTabWidthCut
  expr: Constraints[26] = <<v8-Dimensions>>.solarTabWidthCut
  sketch-geometry (24):
    g0: LineSegment StartX=6.16 StartY=24.16 StartZ=0 EndX=94 EndY=24.16 EndZ=0
    g1: LineSegment StartX=100.16 StartY=18 StartZ=0 EndX=100.16 EndY=0 EndZ=0
    g2: LineSegment StartX=100.16 StartY=0 StartZ=0 EndX=94 EndY=0 EndZ=0
    g3: LineSegment StartX=94 StartY=0 StartZ=0 EndX=94 EndY=10.16 EndZ=0
    g4: LineSegment StartX=94 StartY=10.16 StartZ=0 EndX=91.16 EndY=10.16 EndZ=0
    g5: LineSegment StartX=91.16 StartY=10.16 StartZ=0 EndX=91.16 EndY=0 EndZ=0
    g6: LineSegment StartX=91.16 StartY=0 StartZ=0 EndX=53 EndY=0 EndZ=0
    g7: LineSegment StartX=53 StartY=0 StartZ=0 EndX=53 EndY=10.16 EndZ=0
    g8: LineSegment StartX=53 StartY=10.16 StartZ=0 EndX=50.16 EndY=10.16 EndZ=0
    g9: LineSegment StartX=50.16 StartY=10.16 StartZ=0 EndX=50.16 EndY=0 EndZ=0
    g10: LineSegment StartX=50.16 StartY=0 StartZ=0 EndX=12 EndY=0 EndZ=0
    g11: LineSegment StartX=12 StartY=0 StartZ=0 EndX=12 EndY=10.16 EndZ=0
    g12: LineSegment StartX=12 StartY=10.16 StartZ=0 EndX=6.16 EndY=10.16 EndZ=0
    g13: LineSegment StartX=6.16 StartY=10.16 StartZ=0 EndX=6.16 EndY=0 EndZ=0
    g14: LineSegment StartX=6.16 StartY=0 StartZ=0 EndX=0 EndY=0 EndZ=0
    g15: LineSegment StartX=0 StartY=0 StartZ=0 EndX=0 EndY=18 EndZ=0
    g16: ArcOfCircle CenterX=94 CenterY=18 CenterZ=0 NormalX=0 NormalY=0 NormalZ=1 AngleXU=0 Radius=6.16 StartAngle=0 EndAngle=1.5708
    g17: GeomPoint [constr] X=100.16 Y=24.16 Z=0
    g18: ArcOfCircle CenterX=6.16 CenterY=18 CenterZ=0 NormalX=0 NormalY=0 NormalZ=1 AngleXU=0 Radius=6.16 StartAngle=1.5708 EndAngle=3.14159
    g19: GeomPoint [constr] X=0 Y=24.16 Z=0
    g20: Circle CenterX=19.08 CenterY=6.08 CenterZ=0 NormalX=0 NormalY=0 NormalZ=1 AngleXU=0 Radius=1.96
    g21: Circle CenterX=43.08 CenterY=6.08 CenterZ=0 NormalX=0 NormalY=0 NormalZ=1 AngleXU=0 Radius=1.96
    g22: Circle CenterX=60.08 CenterY=6.08 CenterZ=0 NormalX=0 NormalY=0 NormalZ=1 AngleXU=0 Radius=1.96
    g23: Circle CenterX=84.08 CenterY=6.08 CenterZ=0 NormalX=0 NormalY=0 NormalZ=1 AngleXU=0 Radius=1.96
  constraints (68):
    c: Horizontal(g0)
    c: Vertical(g1)
    c: Distance(g2) = 6.16
    c: Coincident(g2,g1)
    c: Horizontal(g2)
    c: Distance(g3) = 10.16
    c: Coincident(g3,g2)
    c: Vertical(g3)
    c: PointOnObject(g1,g-1)
    c: Distance(g4) = 2.84
    c: Coincident(g4,g3)
    c: Horizontal(g4)
    c: PointOnObject(g5,g-1)
    c: Vertical(g5)
    c: Distance(g6) = 38.16
    c: Coincident(g6,g5)
    c: PointOnObject(g6,g-1)
    c: Distance(g7) = 10.16
    c: Coincident(g7,g6)
    c: Vertical(g7)
    c: Distance(g8) = 2.84
    c: Coincident(g8,g7)
    c: Horizontal(g8)
    c: Coincident(g9,g8)
    c: PointOnObject(g9,g-1)
    c: Vertical(g9)
    c: Distance(g10) = 38.16
    c: Coincident(g10,g9)
    c: PointOnObject(g10,g-1)
    c: Distance(g11) = 10.16
    c: Coincident(g11,g10)
    c: Vertical(g11)
    c: Distance(g12) = 5.84
    c: Coincident(g12,g11)
    c: Horizontal(g12)
    c: Coincident(g13,g12)
    c: PointOnObject(g13,g-1)
    c: Vertical(g13)
    c: Distance(g14) = 6.16
    c: Coincident(g14,g13)
    c: PointOnObject(g14,g-1)
    c: Coincident(g5,g4)
    c: Distance(g15,g19) = 24.16
    c: Coincident(g15,g14)
    c: Vertical(g15)
    c: PointOnObject(g19,g-2)
    c: PointOnObject(g17,g1)
    c: PointOnObject(g17,g0)
    c: Tangent(g1,g16) = 1.5708
    c: Tangent(g0,g16) = 1.5708
    c: PointOnObject(g19,g15)
    c: PointOnObject(g19,g0)
    c: Tangent(g15,g18) = 1.5708
    c: Tangent(g0,g18) = 1.5708
    c: DistanceX(g15,g18) = 6.16
    c: DistanceX(g0,g1) = 6.16
    c: Diameter(g20) = 3.92
    c: DistanceX(g11,g20) = 7.08
    c: DistanceY(g10,g20) = 6.08
    c: Diameter(g21) = 3.92
    c: Diameter(g22) = 3.92
    c: Diameter(g23) = 3.92
    c: DistanceY(g9,g21) = 6.08
    c: DistanceY(g6,g22) = 6.08
    c: DistanceY(g5,g23) = 6.08
    c: DistanceX(g21,g9) = 7.08
    c: DistanceX(g6,g22) = 7.08
    c: DistanceX(g23,g5) = 7.08
FEATURE [Sketcher::SketchObject] Sketch086  label="v8-angle-jig-geometry"
  ArcFitTolerance = 1e-06
  AttachmentSupport = -> [XY_Plane005]
  FullyConstrained = true
  MakeInternals = false
  MapMode = 5
  expr: Constraints[14] = <<v8-Dimensions>>.mDiameterEdge
  expr: Constraints[16] = <<v8-Dimensions>>.mDiameterEdge
  expr: Constraints[18] = <<v8-Dimensions>>.mDiameterEdge
  sketch-geometry (9):
    g0: LineSegment StartX=0 StartY=0 StartZ=0 EndX=9.27051 EndY=28.5317 EndZ=0
    g1: LineSegment StartX=9.27051 StartY=28.5317 StartZ=0 EndX=-20.7295 EndY=28.5317 EndZ=0
    g2: LineSegment StartX=-12.58 StartY=-95 StartZ=0 EndX=12.58 EndY=-95 EndZ=0
    g3: GeomPoint X=0 Y=-55 Z=0
    g4: GeomPoint X=0 Y=-85 Z=0
    g5: GeomPoint X=0 Y=-25 Z=0
    g6: Circle CenterX=9.27051 CenterY=28.5317 CenterZ=0 NormalX=0 NormalY=0 NormalZ=1 AngleXU=0 Radius=7.58
    g7: Circle CenterX=-20.7295 CenterY=28.5317 CenterZ=0 NormalX=0 NormalY=0 NormalZ=1 AngleXU=0 Radius=7.58
    g8: Circle CenterX=0 CenterY=0 CenterZ=0 NormalX=0 NormalY=0 NormalZ=1 AngleXU=0 Radius=7.58
  constraints (20):
    c: Distance(g0) = 30
    c: Angle(g-1,g0) = 1.25664
    c: Coincident(g0,g-1)
    c: Distance(g1) = 30
    c: Coincident(g1,g0)
    c: Horizontal(g1)
    c: Distance(g2) = 25.16
    c: Symmetric(g2,g2,g-2)
    c: DistanceY(g2,g0) = 95
    c: PointOnObject(g3,g-2)
    c: PointOnObject(g4,g-2)
    c: DistanceY(g2,g4) = 10
    c: DistanceY(g2,g5) = 70
    c: Symmetric(g5,g4,g3)
    c: Diameter(g6) = 15.16
    c: Coincident(g6,g0)
    c: Diameter(g7) = 15.16
    c: Coincident(g7,g1)
    c: Diameter(g8) = 15.16
    c: Coincident(g8,g0)
FEATURE [Sketcher::SketchObject] Sketch087  label="v8-angle-jig-1"
  ArcFitTolerance = 1e-06
  AttachmentSupport = -> [XY_Plane005]
  ExternalGeometry = -> [Sketch086]
  FullyConstrained = true
  MakeInternals = false
  MapMode = 5
  expr: Constraints[38] = <<v8-Dimensions>>.mDiameterEdge - 3 * <<v8-Dimensions>>.kerf
  sketch-geometry (24):
    g0: ArcOfCircle CenterX=9.27051 CenterY=28.5317 CenterZ=0 NormalX=0 NormalY=0 NormalZ=1 AngleXU=0 Radius=7.46 StartAngle=4.71239 EndAngle=6.28319
    g1: ArcOfCircle CenterX=-20.7295 CenterY=28.5317 CenterZ=0 NormalX=0 NormalY=0 NormalZ=1 AngleXU=0 Radius=7.46 StartAngle=3.14159 EndAngle=4.71239
    g2: LineSegment StartX=-8.58 StartY=-95 StartZ=0 EndX=8.58 EndY=-95 EndZ=0
    g3: LineSegment StartX=12.58 StartY=-91 StartZ=0 EndX=12.58 EndY=15.3199 EndZ=0
    g4: LineSegment StartX=-12.58 StartY=-91 StartZ=0 EndX=-12.58 EndY=8.91169 EndZ=0
    g5: LineSegment StartX=-28.1895 StartY=34.6917 StartZ=0 EndX=-28.1895 EndY=28.5317 EndZ=0
    g6: LineSegment StartX=-28.1895 StartY=34.6917 StartZ=0 EndX=-34.3495 EndY=34.6917 EndZ=0
    g7: LineSegment StartX=-34.3495 StartY=34.6917 StartZ=0 EndX=-34.3495 EndY=28.5317 EndZ=0
    g8: LineSegment StartX=16.7305 StartY=28.5317 StartZ=0 EndX=16.7305 EndY=34.6917 EndZ=0
    g9: LineSegment StartX=16.7305 StartY=34.6917 StartZ=0 EndX=22.8905 EndY=34.6917 EndZ=0
    g10: LineSegment StartX=22.8905 StartY=34.6917 StartZ=0 EndX=22.8905 EndY=28.5317 EndZ=0
    g11: LineSegment StartX=-20.7295 StartY=21.0717 StartZ=0 EndX=9.27051 EndY=21.0717 EndZ=0
    g12: ArcOfCircle CenterX=-20.7295 CenterY=28.5317 CenterZ=0 NormalX=0 NormalY=0 NormalZ=1 AngleXU=0 Radius=13.62 StartAngle=3.14159 EndAngle=4.71239
    g13: ArcOfCircle CenterX=9.27051 CenterY=28.5317 CenterZ=0 NormalX=0 NormalY=0 NormalZ=1 AngleXU=0 Radius=13.62 StartAngle=4.95783 EndAngle=6.28319
    g14: LineSegment StartX=-18.58 StartY=14.9117 StartZ=0 EndX=-20.7295 EndY=14.9117 EndZ=0
    g15: Circle CenterX=0 CenterY=-25 CenterZ=0 NormalX=0 NormalY=0 NormalZ=1 AngleXU=0 Radius=2.92
    g16: Circle CenterX=0 CenterY=-55 CenterZ=0 NormalX=0 NormalY=0 NormalZ=1 AngleXU=0 Radius=2.92
    g17: Circle CenterX=0 CenterY=-85 CenterZ=0 NormalX=0 NormalY=0 NormalZ=1 AngleXU=0 Radius=2.92
    g18: ArcOfCircle CenterX=-18.58 CenterY=8.91169 CenterZ=0 NormalX=0 NormalY=0 NormalZ=1 AngleXU=0 Radius=6 StartAngle=0 EndAngle=1.5708
    g19: GeomPoint [constr] X=-12.58 Y=14.9117 Z=0
    g20: ArcOfCircle CenterX=-8.58 CenterY=-91 CenterZ=0 NormalX=0 NormalY=0 NormalZ=1 AngleXU=0 Radius=4 StartAngle=3.14159 EndAngle=4.71239
    g21: GeomPoint [constr] X=-12.58 Y=-95 Z=0
    g22: ArcOfCircle CenterX=8.58 CenterY=-91 CenterZ=0 NormalX=0 NormalY=0 NormalZ=1 AngleXU=0 Radius=4 StartAngle=4.71239 EndAngle=6.28319
    g23: GeomPoint [constr] X=12.58 Y=-95 Z=0
  constraints (54):
    c: Coincident(g0,g-10)
    c: Coincident(g1,g-10)
    c: PointOnObject(g0,g-10)
    c: PointOnObject(g1,g-10)
    c: Coincident(g21,g-9)
    c: Coincident(g23,g-9)
    c: Vertical(g3)
    c: Vertical(g4)
    c: Distance(g5) = 6.16
    c: Coincident(g6,g5)
    c: Horizontal(g6)
    c: Coincident(g7,g6)
    c: Vertical(g7)
    c: Coincident(g9,g8)
    c: Horizontal(g9)
    c: Vertical(g10)
    c: Equal(g6,g5)
    c: Equal(g8,g5)
    c: Equal(g9,g5)
    c: Tangent(g1,g5) = -1.5708
    c: Tangent(g8,g0) = -1.5708
    c: Horizontal(g11)
    c: Tangent(g11,g1) = -1.5708
    c: Tangent(g11,g0) = -1.5708
    c: Coincident(g12,g1)
    c: Coincident(g13,g0)
    c: Tangent(g7,g12) = -1.5708
    c: Tangent(g10,g13) = 1.5708
    c: Coincident(g10,g9)
    c: Coincident(g13,g3)
    c: Horizontal(g14)
    c: Tangent(g14,g12) = 1.5708
    c: Diameter(g15) = 5.84
    c: Coincident(g15,g-6)
    c: Diameter(g16) = 5.84
    c: Coincident(g16,g-8)
    c: Diameter(g17) = 5.84
    c: Coincident(g17,g-7)
    c: Diameter(g1) = 14.92
    c: PointOnObject(g19,g14)
    c: PointOnObject(g19,g4)
    c: Tangent(g14,g18) = -1.5708
    c: Tangent(g4,g18) = -1.5708
    c: Distance(g4,g18) = 6
    c: PointOnObject(g21,g2)
    c: PointOnObject(g21,g4)
    c: Tangent(g2,g20) = -1.5708
    c: Tangent(g4,g20) = 1.5708
    c: PointOnObject(g23,g3)
    c: PointOnObject(g23,g2)
    c: Tangent(g3,g22) = -1.5708
    c: Tangent(g2,g22) = -1.5708
    c: Distance(g4,g20) = 4
    c: Distance(g3,g22) = 4
FEATURE [Sketcher::SketchObject] Sketch088  label="v8-angle-jig-2"
  ArcFitTolerance = 1e-06
  AttachmentSupport = -> [XY_Plane005]
  ExternalGeometry = -> [Sketch086]
  FullyConstrained = true
  MakeInternals = false
  MapMode = 5
  expr: Constraints[39] = <<v8-Dimensions>>.mDiameterEdge - 3 * <<v8-Dimensions>>.kerf
  expr: Constraints[40] = <<v8-Dimensions>>.mDiameterEdge - 3 * <<v8-Dimensions>>.kerf
  sketch-geometry (20):
    g0: LineSegment StartX=-8.58 StartY=-95 StartZ=0 EndX=8.58 EndY=-95 EndZ=0
    g1: LineSegment StartX=12.58 StartY=-91 StartZ=0 EndX=12.58 EndY=-18.7831 EndZ=0
    g2: LineSegment StartX=-12.58 StartY=-91 StartZ=0 EndX=-12.58 EndY=-18.7831 EndZ=0
    g3: LineSegment StartX=5.71727 StartY=37.5301 StartZ=0 EndX=7.62082 EndY=43.3886 EndZ=0
    g4: LineSegment StartX=7.62082 StartY=43.3886 StartZ=0 EndX=13.4793 EndY=41.4851 EndZ=0
    g5: ArcOfCircle CenterX=9.27051 CenterY=28.5317 CenterZ=0 NormalX=0 NormalY=0 NormalZ=1 AngleXU=0 Radius=13.62 StartAngle=6.06176 EndAngle=7.53982
    g6: Circle CenterX=0 CenterY=-25 CenterZ=0 NormalX=0 NormalY=0 NormalZ=1 AngleXU=0 Radius=2.92
    g7: Circle CenterX=0 CenterY=-55 CenterZ=0 NormalX=0 NormalY=0 NormalZ=1 AngleXU=0 Radius=2.92
    g8: Circle CenterX=0 CenterY=-85 CenterZ=0 NormalX=0 NormalY=0 NormalZ=1 AngleXU=0 Radius=2.92
    g9: ArcOfCircle CenterX=-8.58 CenterY=-91 CenterZ=0 NormalX=0 NormalY=0 NormalZ=1 AngleXU=0 Radius=4 StartAngle=3.14159 EndAngle=4.71239
    g10: GeomPoint [constr] X=-12.58 Y=-95 Z=0
    g11: ArcOfCircle CenterX=8.58 CenterY=-91 CenterZ=0 NormalX=0 NormalY=0 NormalZ=1 AngleXU=0 Radius=4 StartAngle=4.71239 EndAngle=6.28319
    g12: GeomPoint [constr] X=12.58 Y=-95 Z=0
    g13: ArcOfCircle CenterX=0 CenterY=0 CenterZ=0 NormalX=0 NormalY=0 NormalZ=1 AngleXU=0 Radius=7.46 StartAngle=4.39823 EndAngle=5.96903
    g14: LineSegment StartX=-8.16378 StartY=-5.19134 StartZ=0 EndX=-2.30527 EndY=-7.09488 EndZ=0
    g15: LineSegment StartX=-8.16378 StartY=-5.19134 StartZ=0 EndX=-12.58 EndY=-18.7831 EndZ=0
    g16: ArcOfCircle CenterX=9.27051 CenterY=28.5317 CenterZ=0 NormalX=0 NormalY=0 NormalZ=1 AngleXU=0 Radius=7.46 StartAngle=5.96903 EndAngle=7.53982
    g17: LineSegment StartX=5.71727 StartY=37.5301 StartZ=0 EndX=11.5758 EndY=35.6266 EndZ=0
    g18: LineSegment StartX=16.3654 StartY=26.2264 StartZ=0 EndX=7.09488 EndY=-2.30527 EndZ=0
    g19: LineSegment StartX=22.558 StartY=25.5405 StartZ=0 EndX=12.58 EndY=-18.7831 EndZ=0
  constraints (45):
    c: Coincident(g10,g-8)
    c: Coincident(g12,g-8)
    c: Vertical(g1)
    c: Vertical(g2)
    c: Tangent(g4,g5) = 1.5708
    c: Coincident(g4,g3)
    c: Diameter(g6) = 5.84
    c: Coincident(g6,g-5)
    c: Diameter(g7) = 5.84
    c: Coincident(g7,g-7)
    c: Diameter(g8) = 5.84
    c: Coincident(g8,g-6)
    c: PointOnObject(g10,g0)
    c: PointOnObject(g10,g2)
    c: Tangent(g0,g9) = -1.5708
    c: Tangent(g2,g9) = 1.5708
    c: PointOnObject(g12,g1)
    c: PointOnObject(g12,g0)
    c: Tangent(g1,g11) = -1.5708
    c: Tangent(g0,g11) = -1.5708
    c: Distance(g2,g9) = 4
    c: Distance(g1,g11) = 4
    c: PointOnObject(g4,g-4)
    c: Distance(g3) = 6.16
    c: Equal(g4,g3)
    c: Perpendicular(g3,g4)
    c: Coincident(g-9,g5)
    c: Coincident(g13,g-1)
    c: PointOnObject(g13,g-4)
    c: Distance(g14) = 6.16
    c: Tangent(g14,g13) = -1.5708
    c: Coincident(g15,g14)
    c: Perpendicular(g14,g15)
    c: Coincident(g16,g5)
    c: Coincident(g17,g3)
    c: Tangent(g17,g16) = 1.5708
    c: Parallel(g4,g17)
    c: Tangent(g18,g16) = 1.5708
    c: Tangent(g18,g13) = 1.5708
    c: Diameter(g16) = 14.92
    c: Diameter(g13) = 14.92
    c: Coincident(g15,g2)
    c: Equal(g2,g1)
    c: Coincident(g19,g1)
    c: Tangent(g19,g5) = 1.5708
FEATURE [Sketcher::SketchObject] Sketch089  label="v8-angle-jig-3"
  ArcFitTolerance = 1e-06
  AttachmentSupport = -> [XY_Plane005]
  ExternalGeometry = -> [Sketch086]
  FullyConstrained = true
  MakeInternals = false
  MapMode = 5
  sketch-geometry (11):
    g0: LineSegment StartX=-8.58 StartY=-95 StartZ=0 EndX=8.58 EndY=-95 EndZ=0
    g1: LineSegment StartX=12.58 StartY=-91 StartZ=0 EndX=12.58 EndY=-16.6202 EndZ=0
    g2: LineSegment StartX=-12.58 StartY=-91 StartZ=0 EndX=-12.58 EndY=-16.6202 EndZ=0
    g3: Circle CenterX=0 CenterY=-25 CenterZ=0 NormalX=0 NormalY=0 NormalZ=1 AngleXU=0 Radius=2.92
    g4: Circle CenterX=0 CenterY=-55 CenterZ=0 NormalX=0 NormalY=0 NormalZ=1 AngleXU=0 Radius=2.92
    g5: Circle CenterX=0 CenterY=-85 CenterZ=0 NormalX=0 NormalY=0 NormalZ=1 AngleXU=0 Radius=2.92
    g6: ArcOfCircle CenterX=-8.58 CenterY=-91 CenterZ=0 NormalX=0 NormalY=0 NormalZ=1 AngleXU=0 Radius=4 StartAngle=3.14159 EndAngle=4.71239
    g7: GeomPoint [constr] X=-12.58 Y=-95 Z=0
    g8: ArcOfCircle CenterX=8.58 CenterY=-91 CenterZ=0 NormalX=0 NormalY=0 NormalZ=1 AngleXU=0 Radius=4 StartAngle=4.71239 EndAngle=6.28319
    g9: GeomPoint [constr] X=12.58 Y=-95 Z=0
    g10: LineSegment StartX=-12.58 StartY=-16.6202 StartZ=0 EndX=12.58 EndY=-16.6202 EndZ=0
  constraints (24):
    c: Coincident(g7,g-7)
    c: Coincident(g9,g-7)
    c: Vertical(g1)
    c: Vertical(g2)
    c: Diameter(g3) = 5.84
    c: Coincident(g3,g-4)
    c: Diameter(g4) = 5.84
    c: Coincident(g4,g-6)
    c: Diameter(g5) = 5.84
    c: Coincident(g5,g-5)
    c: PointOnObject(g7,g0)
    c: PointOnObject(g7,g2)
    c: Tangent(g0,g6) = -1.5708
    c: Tangent(g2,g6) = 1.5708
    c: PointOnObject(g9,g1)
    c: PointOnObject(g9,g0)
    c: Tangent(g1,g8) = -1.5708
    c: Tangent(g0,g8) = -1.5708
    c: Distance(g2,g6) = 4
    c: Distance(g1,g8) = 4
    c: Equal(g2,g1)
    c: Coincident(g10,g1)
    c: Coincident(g10,g2)
    c: DistanceY(g1,g-1) = 16.6202
FEATURE [Sketcher::SketchObject] Sketch090  label="v8-solar-backstop"
  ArcFitTolerance = 1e-06
  AttachmentSupport = -> [XY_Plane005]
  ExternalGeometry = -> [Sketch063]
  FullyConstrained = true
  MakeInternals = false
  MapMode = 5
  sketch-geometry (16):
    g0: LineSegment StartX=-21.92 StartY=77.92 StartZ=0 EndX=-21.92 EndY=72.08 EndZ=0
    g1: LineSegment StartX=-21.92 StartY=72.08 StartZ=0 EndX=-24.92 EndY=72.08 EndZ=0
    g2: LineSegment StartX=-21.92 StartY=77.92 StartZ=0 EndX=-24.92 EndY=77.92 EndZ=0
    g3: LineSegment StartX=-24.92 StartY=82.16 StartZ=0 EndX=-49.92 EndY=82.16 EndZ=0
    g4: LineSegment StartX=-24.92 StartY=82.16 StartZ=0 EndX=-24.92 EndY=77.92 EndZ=0
    g5: LineSegment StartX=-49.92 StartY=82.16 StartZ=0 EndX=-49.92 EndY=84.66 EndZ=0
    g6: LineSegment StartX=-49.92 StartY=84.66 StartZ=0 EndX=-53.08 EndY=84.66 EndZ=0
    g7-g10: Circle [constr] x4 (B-spline internal-alignment scaffolding for g11; pole/knot coordinates omitted)
    g11: BSplineCurve PolesCount=4 KnotsCount=2 Degree=3 IsPeriodic=0
    g12: GeomPoint [constr] X=-53.08 Y=84.66 Z=0
    g13: GeomPoint [constr] X=-24.92 Y=72.08 Z=0
    g14: Circle CenterX=-34.92 CenterY=77.92 CenterZ=0 NormalX=0 NormalY=0 NormalZ=1 AngleXU=0 Radius=1.92
    g15: Circle CenterX=-44.92 CenterY=77.92 CenterZ=0 NormalX=0 NormalY=0 NormalZ=1 AngleXU=0 Radius=1.92
  constraints (39):
    c: Coincident(g0,g-7)
    c: Coincident(g0,g-8)
    c: Distance(g1) = 3
    c: Coincident(g1,g0)
    c: Coincident(g2,g0)
    c: Horizontal(g2)
    c: Horizontal(g1)
    c: Equal(g1,g2)
    c: Distance(g3) = 25
    c: Horizontal(g3)
    c: Coincident(g4,g3)
    c: Coincident(g4,g2)
    c: Vertical(g4)
    c: PointOnObject(g3,g-9)
    c: Coincident(g5,g3)
    c: Vertical(g5)
    c: PointOnObject(g5,g-10)
    c: Distance(g6) = 3.16
    c: Coincident(g6,g5)
    c: Horizontal(g6)
    c: Weight(g7) = 1
    c: Equal(g7,g8)
    c: Equal(g7,g9)
    c: Equal(g7,g10)
    c: InternalAlignment(g7-g10 -> g11) x4
    c: InternalAlignment(g12,g11)
    c: InternalAlignment(g13,g11)
    c: Coincident(g7,g6)
    c: Coincident(g10,g1)
    c: PointOnObject(g8,g1)
    c: PointOnObject(g9,g1)
    c: PointOnObject(g9,g5)
    c: DistanceX(g8,g9) = 3.16
    c: Diameter(g14) = 3.84
    c: Diameter(g15) = 3.84
    c: PointOnObject(g14,g2)
    c: PointOnObject(g15,g2)
    c: DistanceX(g14,g2) = 10
    c: DistanceX(g15,g14) = 10
FEATURE [PartDesign::Body] Body005  label="v8"
  AllowCompound = false
  Group = -> [Sketch063,Sketch064,Sketch065,Sketch066,Sketch067,Sketch068,Sketch069,Sketch070,Sketch071,Sketch072,Sketch073,Sketch074,Sketch075,Sketch076,Sketch077,Sketch078,Sketch079,Sketch080,Sketch081,Sketch082,Sketch083,Sketch086,Sketch087,Sketch088,Sketch089,Sketch090]
  Origin = -> Origin005
FEATURE [Spreadsheet::Sheet] Spreadsheet001  label="v9-dimensions"
  cells = A1='kerf; B1(kerf)=0.08; A2='mLength; B2(mLength)=60; A3='mDiameterCut; B3(mDiameterCut)==6 - 0.16; A4='mDiameterEdge; B4(mDiameterEdge)==15 + 2 * kerf; A5='mMidWidth; B5(mMidWidth)=5; A6='jLength; B6(jLength)=100; A7='jBearingCut; B7(jBearingCut)==10 - 0.16; A8='jDiameterCut; B8(jDiameterCut)=3; A9='jDiameterEdge; B9(jDiameterEdge)==8 + 0.16; A10='jBendPoint; B10(jBendPoint)=45; A11='jBendWidth; B11(jBendWidth)=4; A12='jBendOffset; B12(jBendOffset)=15; A13='kBearingCut; B13(kBearingCut)==jBearingCut; A14='kDiameterCut; B14(kDiameterCut)==jDiameterCut; A15='kDiameterEdge; B15(kDiameterEdge)==jDiameterEdge; A16='kBendPoint; B16(kBendPoint)=55; A17='kBendWidth; B17(kBendWidth)=4; A18='kBendOffset; B18(kBendOffset)=15; A19='bLength; B19(bLength)=83; A20='bBendWidth; B20(bBendWidth)=5; A21='bBendOffset; B21(bBendOffset)=10; A22='dLength; B22(dLength)=80.2; A23='dBendWidth; B23(dBendWidth)=5; A24='dBendOffset; B24(dBendOffset)=14; A25='eLength; B25(eLength)=111.6; A26='eBendWidth; B26(eBendWidth)=4; A27='eBendOffset; B27(eBendOffset)=8; A28='bdeDiameterCut; B28(bdeDiameterCut)==jDiameterCut; A29='bdeDiameterEdge; B29(bdeDiameterEdge)==jDiameterEdge; A30='bdeJunctionCut; B30(bdeJunctionCut)==8 - 0.16; A31='bdeJunctionEdge; B31(bdeJunctionEdge)==14 + kerf * 2; A32='frame4mmCut; B32(frame4mmCut)==4 - 0.16; A33='frame4mmEdge; B33(frame4mmEdge)==8 + 0.16; A34='fLength; B34(fLength)=78.8; A35='fBendWidth; B35(fBendWidth)=5; A36='fBendOffset; B36(fBendOffset)=8; A37='cLength; B37(cLength)=78.6; A38='cBendWidth; B38(cBendWidth)=5; A39='cBendOffset; B39(cBendOffset)=8; A40='cJunctionCut; B40(cJunctionCut)==bdeJunctionCut; A41='cJunctionEdge; B41(cJunctionEdge)==bdeJunctionEdge; A42='gLength; B42(gLength)=73.4; A43='gBendWidth; B43(gBendWidth)=5; A44='gBendOffset; B44(gBendOffset)=8; A45='hLength; B45(hLength)=131.4; A46='hBendWidth; B46(hBendWidth)=5; A47='hBendOffset; B47(hBendOffset)=10; A48='iLength; B48(iLength)=98; A49='iBendWidth; B49(iBendWidth)=5; A50='iBendOffset; B50(iBendOffset)=10; A51='ghiFootRadius; B51(ghiFootRadius)=1.5; A52='joint3mmCut; B52(joint3mmCut)=3; A53='joint3mmEdge; B53(joint3mmEdge)==8 + 0.16; A54='aLowerSupportDrop; B54(aLowerSupportDrop)=70; A55='aLowerSupportDiameter; B55(aLowerSupportDiameter)=4; A56='aLowerSupportCut; B56(aLowerSupportCut)==aLowerSupportDiameter - kerf * 2; A57='aLowerSupportEdge; B57(aLowerSupportEdge)==aLowerSupportDiameter + kerf * 2; A58='aLowerSupportAnchors; B58(aLowerSupportAnchors)=25; A59='aLowerSupportAnchorDrop; B59(aLowerSupportAnchorDrop)=8; A60='aGearDistance; B60(aGearDistance)=66; A61='aMotorShaftDiameter; B61(aMotorShaftDiameter)=3; A62='aMotorWidthDiameter; B62(aMotorWidthDiameter)=12; A63='aMotorWidthCut; B63(aMotorWidthCut)==aMotorWidthDiameter - kerf * 2; A64='aMotorHeight; B64(aMotorHeight)=10; A65='aMotorHeightCut; B65(aMotorHeightCut)==aMotorHeight - kerf * 2; A66='aMotorToTabCenterDistance; B66(aMotorToTabCenterDistance)==1.5 + 5 + 4; A67='aJunctionCut; B67(aJunctionCut)==4 - kerf * 2; A68='aJunctionEdge; B68(aJunctionEdge)==4 + 6 + kerf * 2; A69='crankBearingCut; B69(crankBearingCut)==10 - kerf * 2; A70='crankBearingEdge; B70(crankBearingEdge)==crankBearingCut + 5; A71='tabWidth; B71(tabWidth)=6; A72='tabWidthCut; B72(tabWidthCut)==tabWidth - kerf * 2; A73='tabHeight; B73(tabHeight)=3; A74='tabHeightCut; B74(tabHeightCut)==tabHeight - kerf * 2; A75='tabDistance; B75(tabDistance)=4; A76='tabDistanceCut; B76(tabDistanceCut)==tabDistance + kerf * 2; A77='solarTabWidth; B77(solarTabWidth)=38; A78='solarTabWidthCut; B78(solarTabWidthCut)==solarTabWidth + kerf * 2; A79='solarSideWidth; B79(solarSideWidth)=4; A80='solarSideWidthCut; B80(solarSideWidthCut)==solarSideWidth + kerf * 2; A81='solarPanelWidth; B81(solarPanelWidth)=60; A82='solarPanelWidthCut; B82(solarPanelWidthCut)==solarPanelWidth - kerf * 2; A83='solarPanelDepth; B83(solarPanelDepth)=2.5; A84='solarPanelDepthCut; B84(solarPanelDepthCut)==solarPanelDepth + kerf * 2; A85='wireHole; B85(wireHole)=6; A86='wireHoleCut; B86(wireHoleCut)==wireHole - kerf * 2; A87='largeGearOuterDiameter; B87(largeGearOuterDiameter)=113.354; A88='largeGearInnerDiameter; B88(largeGearInnerDiameter)==largeGearOuterDiameter - 30; A89='largeGearHubDiameter; B89(largeGearHubDiameter)=6; A90='largeGearSpokeWidth; B90(largeGearSpokeWidth)=7; A91='largeGearSpokeHub; B91(largeGearSpokeHub)=15; A92='smallGearOuterDiameter; B92(smallGearOuterDiameter)=25.3; A93='smallGearHubDiameter; B93(smallGearHubDiameter)=3
FEATURE [App::DocumentObjectGroup] Group
